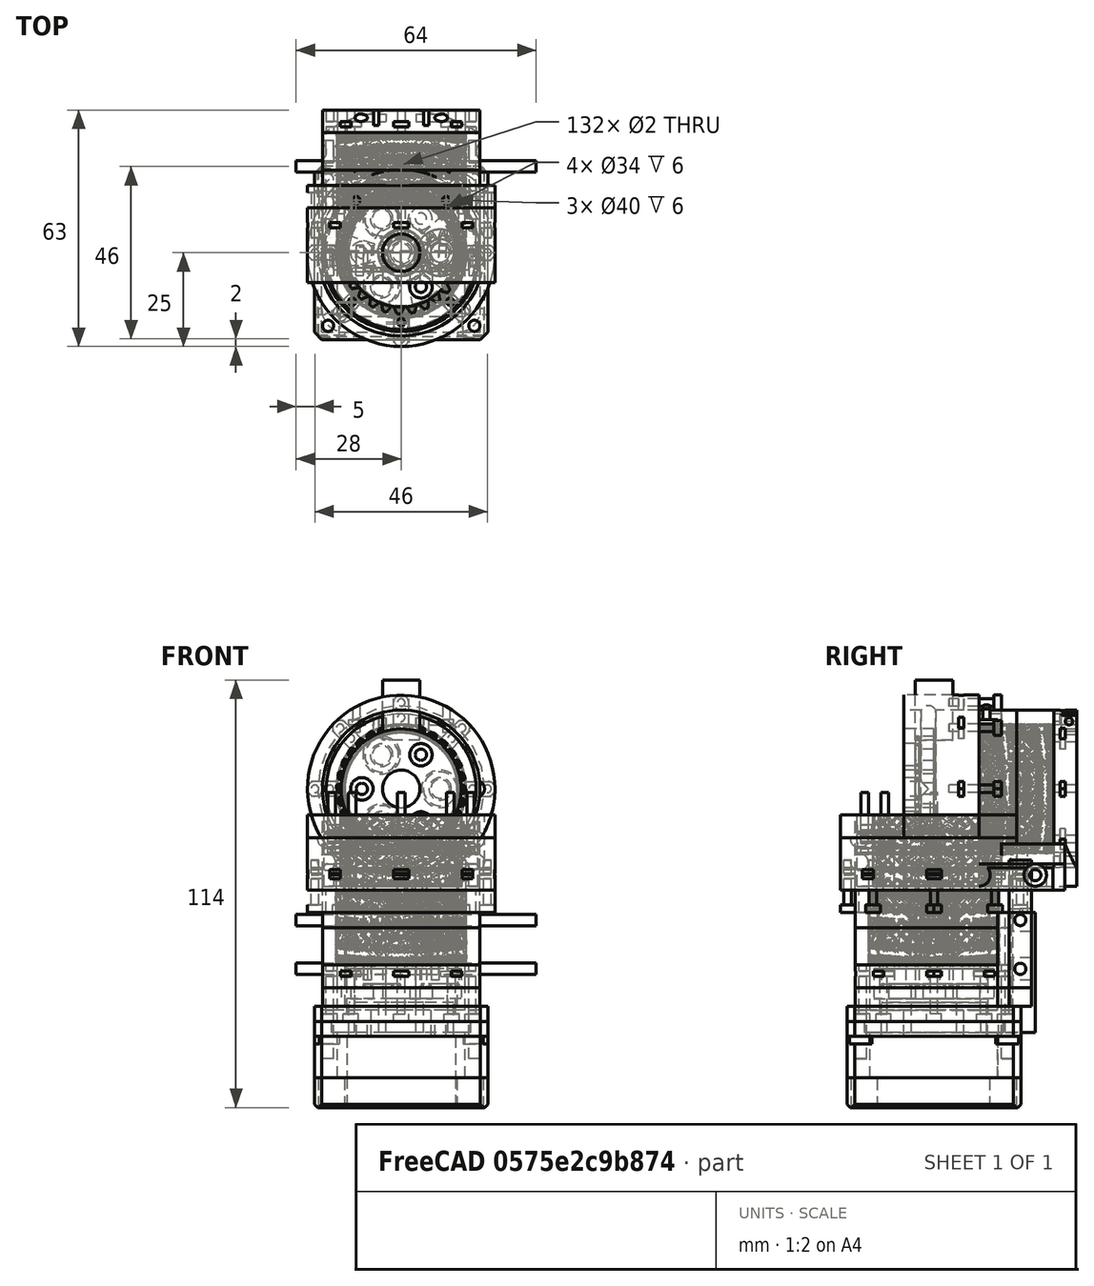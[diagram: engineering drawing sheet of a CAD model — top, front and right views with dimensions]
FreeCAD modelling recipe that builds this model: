
FCSTD DOCUMENT  (FreeCAD 0.19R24276 (Git))
Label: G-mini_gearbox_036
License: All rights reserved
LicenseURL: http://en.wikipedia.org/wiki/All_rights_reserved
objects: Part::Cylinder×349, Part::Box×234, Part::Cut×155, Part::Compound×130, Part::FeaturePython×71, Part::Common×20, Mesh::Feature×13, Part::Torus×6, Part::Chamfer×6
note: 971 computed .brp shape members not serialized (recipe doc carries the construction recipe); baked Part::Feature solids carry a one-line shape summary decoded from their .brp

FEATURE [Part::Torus] Torus003  label="Anuloid003"
  Angle1 = -180
  Angle2 = 180
  Angle3 = 360
  AttacherType = Attacher::AttachEngine3D
  Placement = pos=(0,0,23.5) rot=(0,0,1;0rad)
  Radius1 = 20
  Radius2 = 2.2
FEATURE [Part::Cylinder] Cylinder061  label="Válec061"
  Angle = 360
  AttacherType = Attacher::AttachEngine3D
  Height = 10
  Placement = pos=(20,0,23.5) rot=(0,0,1;0rad)
  Radius = 2.2
FEATURE [Part::Cylinder] Cylinder062  label="Válec062"
  Angle = 360
  AttacherType = Attacher::AttachEngine3D
  Height = 10
  Placement = pos=(0,23,8) rot=(0,0,1;0rad)
  Radius = 1
FEATURE [Part::Cylinder] Cylinder063  label="Válec063"
  Angle = 360
  AttacherType = Attacher::AttachEngine3D
  Height = 10
  Placement = pos=(-16.26,16.26,8) rot=(0,0,1;0.785398rad)
  Radius = 1
FEATURE [Part::Cylinder] Cylinder064  label="Válec064"
  Angle = 360
  AttacherType = Attacher::AttachEngine3D
  Height = 10
  Placement = pos=(-23,0,8) rot=(0,0,1;1.5708rad)
  Radius = 1
FEATURE [Part::Cylinder] Cylinder065  label="Válec065"
  Angle = 360
  AttacherType = Attacher::AttachEngine3D
  Height = 10
  Placement = pos=(-16.26,-16.26,8) rot=(0,0,1;2.35619rad)
  Radius = 1
FEATURE [Part::Cylinder] Cylinder066  label="Válec066"
  Angle = 360
  AttacherType = Attacher::AttachEngine3D
  Height = 10
  Placement = pos=(4e-15,-23,8) rot=(0,0,1;3.14159rad)
  Radius = 1
FEATURE [Part::Cylinder] Cylinder067  label="Válec067"
  Angle = 360
  AttacherType = Attacher::AttachEngine3D
  Height = 10
  Placement = pos=(16.26,-16.26,8) rot=(0,0,1;3.92699rad)
  Radius = 1
FEATURE [Part::Cylinder] Cylinder068  label="Válec068"
  Angle = 360
  AttacherType = Attacher::AttachEngine3D
  Height = 10
  Placement = pos=(23,1.1e-14,8) rot=(0,0,-1;1.5708rad)
  Radius = 1
FEATURE [Part::Cylinder] Cylinder069  label="Válec069"
  Angle = 360
  AttacherType = Attacher::AttachEngine3D
  Height = 10
  Placement = pos=(16.26,16.26,8) rot=(0,0,-1;0.785398rad)
  Radius = 1
FEATURE [Part::Compound] Compound019
  Links = -> [Cylinder062,Cylinder069,Cylinder068,Cylinder066,Cylinder067,Cylinder065,Cylinder063,Cylinder064]
FEATURE [Part::FeaturePython] Tube004  # WARN: FeaturePython — macro-defined, semantics opaque (R4)
  AttacherType = Attacher::AttachEngine3D
  Height = 20
  InnerRadius = 21
  OuterRadius = 25
  Placement = pos=(0,0,10) rot=(0,0,1;0rad)
FEATURE [Part::Cut] Cut018
  Base = -> Tube004
  Tool = -> Torus003
FEATURE [Part::Box] Box016  label="Krychle016"
  AttacherType = Attacher::AttachEngine3D
  Height = 1.4
  Length = 4
  Placement = pos=(-2,21,14) rot=(0,0,1;0rad)
  Width = 4
FEATURE [Part::Box] Box017  label="Krychle017"
  AttacherType = Attacher::AttachEngine3D
  Height = 1.4
  Length = 4
  Placement = pos=(-16.2635,13.435,14) rot=(0,0,1;0.785398rad)
  Width = 4
FEATURE [Part::Box] Box018  label="Krychle018"
  AttacherType = Attacher::AttachEngine3D
  Height = 1.4
  Length = 4
  Placement = pos=(-21,-2,14) rot=(0,0,1;1.5708rad)
  Width = 4
FEATURE [Part::Box] Box019  label="Krychle019"
  AttacherType = Attacher::AttachEngine3D
  Height = 1.4
  Length = 4
  Placement = pos=(-13.435,-16.2635,14) rot=(0,0,1;2.35619rad)
  Width = 4
FEATURE [Part::Box] Box020  label="Krychle020"
  AttacherType = Attacher::AttachEngine3D
  Height = 1.4
  Length = 4
  Placement = pos=(2,-21,14) rot=(0,0,1;3.14159rad)
  Width = 4
FEATURE [Part::Box] Box021  label="Krychle021"
  AttacherType = Attacher::AttachEngine3D
  Height = 1.4
  Length = 4
  Placement = pos=(16.2635,-13.435,14) rot=(0,0,1;3.92699rad)
  Width = 4
FEATURE [Part::Box] Box022  label="Krychle022"
  AttacherType = Attacher::AttachEngine3D
  Height = 1.4
  Length = 4
  Placement = pos=(21,2,14) rot=(0,0,-1;1.5708rad)
  Width = 4
FEATURE [Part::Box] Box023  label="Krychle023"
  AttacherType = Attacher::AttachEngine3D
  Height = 1.4
  Length = 4
  Placement = pos=(13.435,16.2635,14) rot=(0,0,-1;0.785398rad)
  Width = 4
FEATURE [Part::Compound] Compound020
  Links = -> [Box016,Box017,Box018,Box019,Box020,Box021,Box022,Box023]
FEATURE [Part::Cut] Cut019
  Base = -> Cut018
  Tool = -> Compound020
FEATURE [Part::Cut] Cut020
  Base = -> Cut019
  Tool = -> Compound019
FEATURE [Part::Cut] Cut021  label="G-mini_bearing-ring-old"
  Base = -> Cut020
  Placement = pos=(0,22,37) rot=(1,0,0;1.5708rad)
  Tool = -> Cylinder061
FEATURE [Part::Cylinder] Cylinder084  label="Válec084"
  Angle = 360
  AttacherType = Attacher::AttachEngine3D
  Height = 10
  Placement = pos=(0,23,4) rot=(0,0,1;0rad)
  Radius = 1
FEATURE [Part::Box] Box033  label="Krychle033"
  AttacherType = Attacher::AttachEngine3D
  Height = 6
  Length = 4
  Placement = pos=(10,17,5) rot=(0,0,1;0rad)
  Width = 1.4
FEATURE [Part::Box] Box034  label="Krychle034"
  AttacherType = Attacher::AttachEngine3D
  Height = 6
  Length = 4
  Placement = pos=(-14,17,5) rot=(0,0,1;0rad)
  Width = 1.4
FEATURE [Part::Cylinder] Cylinder077  label="Válec077"
  Angle = 360
  AttacherType = Attacher::AttachEngine3D
  Height = 10
  Placement = pos=(12,25,8) rot=(1,0,0;1.5708rad)
  Radius = 1
FEATURE [Part::Cylinder] Cylinder078  label="Válec078"
  Angle = 360
  AttacherType = Attacher::AttachEngine3D
  Height = 10
  Placement = pos=(-12,25,8) rot=(1,0,0;1.5708rad)
  Radius = 1
FEATURE [Part::Cylinder] Cylinder079  label="Válec079"
  Angle = 360
  AttacherType = Attacher::AttachEngine3D
  Height = 10
  Placement = pos=(16.2635,16.2635,4) rot=(0,0,-1;0.785398rad)
  Radius = 1
FEATURE [Part::Cylinder] Cylinder080  label="Válec080"
  Angle = 360
  AttacherType = Attacher::AttachEngine3D
  Height = 10
  Placement = pos=(16.2635,-16.2635,4) rot=(0,0,1;3.92699rad)
  Radius = 1
FEATURE [Part::Cylinder] Cylinder081  label="Válec081"
  Angle = 360
  AttacherType = Attacher::AttachEngine3D
  Height = 10
  Placement = pos=(-16.2635,16.2635,4) rot=(0,0,1;0.785398rad)
  Radius = 1
FEATURE [Part::Compound] Compound026
  Links = -> [Box033,Box034]
FEATURE [Part::FeaturePython] Tube005  # WARN: FeaturePython — macro-defined, semantics opaque (R4)
  AttacherType = Attacher::AttachEngine3D
  Height = 6
  InnerRadius = 20
  OuterRadius = 25
  Placement = pos=(0,0,4) rot=(0,0,1;0rad)
FEATURE [Part::FeaturePython] Tube006  # WARN: FeaturePython — macro-defined, semantics opaque (R4)
  AttacherType = Attacher::AttachEngine3D
  Height = 6
  InnerRadius = 17
  OuterRadius = 21
  Placement = pos=(0,0,-16) rot=(0,0,1;0rad)
FEATURE [Part::Cylinder] Cylinder082  label="Válec082"
  Angle = 360
  AttacherType = Attacher::AttachEngine3D
  Height = 2
  Placement = pos=(-16.2635,-16.2635,4) rot=(0,0,1;2.35619rad)
  Radius = 2
FEATURE [Part::Cylinder] Cylinder083  label="Válec083"
  Angle = 360
  AttacherType = Attacher::AttachEngine3D
  Height = 10
  Placement = pos=(-23,-1e-15,4) rot=(0,0,1;1.5708rad)
  Radius = 1
FEATURE [Part::Cylinder] Cylinder085  label="Válec085"
  Angle = 360
  AttacherType = Attacher::AttachEngine3D
  Height = 10
  Placement = pos=(-16.2635,-16.2635,4) rot=(0,0,1;2.35619rad)
  Radius = 1
FEATURE [Part::Cylinder] Cylinder086  label="Válec086"
  Angle = 360
  AttacherType = Attacher::AttachEngine3D
  Height = 2
  Placement = pos=(0,23,4) rot=(0,0,1;0rad)
  Radius = 2
FEATURE [Part::Cylinder] Cylinder087  label="Válec087"
  Angle = 360
  AttacherType = Attacher::AttachEngine3D
  Height = 10
  Placement = pos=(23,1.1e-14,4) rot=(0,0,-1;1.5708rad)
  Radius = 1
FEATURE [Part::Cylinder] Cylinder088  label="Válec088"
  Angle = 360
  AttacherType = Attacher::AttachEngine3D
  Height = 2
  Placement = pos=(-23,-1e-15,4) rot=(0,0,1;1.5708rad)
  Radius = 2
FEATURE [Part::Cylinder] Cylinder089  label="Válec089"
  Angle = 360
  AttacherType = Attacher::AttachEngine3D
  Height = 10
  Placement = pos=(4e-15,-23,4) rot=(0,0,1;3.14159rad)
  Radius = 1
FEATURE [Part::Compound] Compound027
  Links = -> [Cylinder084,Cylinder081,Cylinder083,Cylinder085,Cylinder089,Cylinder080,Cylinder087,Cylinder079]
FEATURE [Part::Cylinder] Cylinder090  label="Válec090"
  Angle = 360
  AttacherType = Attacher::AttachEngine3D
  Height = 2
  Placement = pos=(16.2635,-16.2635,4) rot=(0,0,1;3.92699rad)
  Radius = 2
FEATURE [Part::Cylinder] Cylinder091  label="Válec091"
  Angle = 360
  AttacherType = Attacher::AttachEngine3D
  Height = 2
  Placement = pos=(23,1.1e-14,4) rot=(0,0,-1;1.5708rad)
  Radius = 2
FEATURE [Part::Cylinder] Cylinder092  label="Válec092"
  Angle = 360
  AttacherType = Attacher::AttachEngine3D
  Height = 2
  Placement = pos=(16.2635,16.2635,4) rot=(0,0,-1;0.785398rad)
  Radius = 2
FEATURE [Part::Cylinder] Cylinder093  label="Válec093"
  Angle = 360
  AttacherType = Attacher::AttachEngine3D
  Height = 2
  Placement = pos=(-16.2635,16.2635,4) rot=(0,0,1;0.785398rad)
  Radius = 2
FEATURE [Part::Cylinder] Cylinder094  label="Válec094"
  Angle = 360
  AttacherType = Attacher::AttachEngine3D
  Height = 2
  Placement = pos=(4e-15,-23,4) rot=(0,0,1;3.14159rad)
  Radius = 2
FEATURE [Part::Compound] Compound028
  Links = -> [Cylinder086,Cylinder093,Cylinder088,Cylinder082,Cylinder094,Cylinder090,Cylinder091,Cylinder092]
FEATURE [Part::Cut] Cut026
  Base = -> Tube005
  Tool = -> Compound028
FEATURE [Part::Cut] Cut027
  Base = -> Cut026
  Tool = -> Compound027
FEATURE [Part::Cut] Cut032
  Base = -> Cut027
  Tool = -> Compound026
FEATURE [Part::Box] Box035  label="Krychle035"
  AttacherType = Attacher::AttachEngine3D
  Height = 1.4
  Length = 4
  Placement = pos=(-2,17,-13) rot=(0,0,1;0rad)
  Width = 4
FEATURE [Part::Box] Box036  label="Krychle036"
  AttacherType = Attacher::AttachEngine3D
  Height = 1.4
  Length = 4
  Placement = pos=(-13.435,10.6066,-13) rot=(0,0,1;0.785398rad)
  Width = 4
FEATURE [Part::Box] Box037  label="Krychle037"
  AttacherType = Attacher::AttachEngine3D
  Height = 1.4
  Length = 4
  Placement = pos=(-10.6066,-13.435,-13) rot=(0,0,1;2.35619rad)
  Width = 4
FEATURE [Part::Box] Box038  label="Krychle038"
  AttacherType = Attacher::AttachEngine3D
  Height = 1.4
  Length = 4
  Placement = pos=(2,-17,-13) rot=(0,0,1;3.14159rad)
  Width = 4
FEATURE [Part::Compound] Compound033
  Links = -> [Cylinder077,Cylinder078]
FEATURE [Part::Cylinder] Cylinder095  label="Válec095"
  Angle = 360
  AttacherType = Attacher::AttachEngine3D
  Height = 10
  Placement = pos=(0,19,-20) rot=(0,0,1;0rad)
  Radius = 1
FEATURE [Part::Box] Box039  label="Krychle039"
  AttacherType = Attacher::AttachEngine3D
  Height = 1.4
  Length = 4
  Placement = pos=(-17,-2,-13) rot=(0,0,1;1.5708rad)
  Width = 4
FEATURE [Part::Box] Box040  label="Krychle040"
  AttacherType = Attacher::AttachEngine3D
  Height = 1.4
  Length = 4
  Placement = pos=(13.435,-10.6066,-13) rot=(0,0,1;3.92699rad)
  Width = 4
FEATURE [Part::Box] Box041  label="Krychle041"
  AttacherType = Attacher::AttachEngine3D
  Height = 1.4
  Length = 4
  Placement = pos=(10.6066,13.435,-13) rot=(0,0,-1;0.785398rad)
  Width = 4
FEATURE [Part::Cylinder] Cylinder096  label="Válec096"
  Angle = 360
  AttacherType = Attacher::AttachEngine3D
  Height = 10
  Placement = pos=(-13.435,13.435,-20) rot=(0,0,1;0.785398rad)
  Radius = 1
FEATURE [Part::Cylinder] Cylinder097  label="Válec097"
  Angle = 360
  AttacherType = Attacher::AttachEngine3D
  Height = 10
  Placement = pos=(-19,-1e-15,-20) rot=(0,0,1;1.5708rad)
  Radius = 1
FEATURE [Part::Cylinder] Cylinder098  label="Válec098"
  Angle = 360
  AttacherType = Attacher::AttachEngine3D
  Height = 10
  Placement = pos=(-13.435,-13.435,-20) rot=(0,0,1;2.35619rad)
  Radius = 1
FEATURE [Part::Cylinder] Cylinder099  label="Válec099"
  Angle = 360
  AttacherType = Attacher::AttachEngine3D
  Height = 10
  Placement = pos=(6e-15,-19,-20) rot=(0,0,1;3.14159rad)
  Radius = 1
FEATURE [Part::Cylinder] Cylinder100  label="Válec100"
  Angle = 360
  AttacherType = Attacher::AttachEngine3D
  Height = 10
  Placement = pos=(13.435,-13.435,-20) rot=(0,0,1;3.92699rad)
  Radius = 1
FEATURE [Part::Box] Box042  label="Krychle042"
  AttacherType = Attacher::AttachEngine3D
  Height = 1.4
  Length = 4
  Placement = pos=(17,2,-13) rot=(0,0,-1;1.5708rad)
  Width = 4
FEATURE [Part::Compound] Compound029
  Links = -> [Box035,Box036,Box039,Box037,Box038,Box040,Box042,Box041]
FEATURE [Part::Cut] Cut028
  Base = -> Tube006
  Tool = -> Compound029
FEATURE [Part::Cylinder] Cylinder101  label="Válec101"
  Angle = 360
  AttacherType = Attacher::AttachEngine3D
  Height = 10
  Placement = pos=(19,8e-15,-20) rot=(0,0,-1;1.5708rad)
  Radius = 1
FEATURE [Part::Cylinder] Cylinder102  label="Válec102"
  Angle = 360
  AttacherType = Attacher::AttachEngine3D
  Height = 10
  Placement = pos=(13.435,13.435,-20) rot=(0,0,-1;0.785398rad)
  Radius = 1
FEATURE [Part::Compound] Compound030
  Links = -> [Cylinder095,Cylinder096,Cylinder097,Cylinder098,Cylinder099,Cylinder100,Cylinder101,Cylinder102]
FEATURE [Part::Cut] Cut029
  Base = -> Cut028
  Tool = -> Compound030
FEATURE [Part::Cylinder] Cylinder103  label="Válec103"
  Angle = 360
  AttacherType = Attacher::AttachEngine3D
  Height = 10
  Radius = 21
FEATURE [Part::Cylinder] Cylinder104  label="Válec104"
  Angle = 360
  AttacherType = Attacher::AttachEngine3D
  Height = 10
  Radius = 21
FEATURE [Part::Box] Box043  label="Krychle043"
  AttacherType = Attacher::AttachEngine3D
  Height = 6
  Length = 4
  Placement = pos=(10,17,5) rot=(0,0,1;0rad)
  Width = 1.4
FEATURE [Part::Box] Box044  label="Krychle044"
  AttacherType = Attacher::AttachEngine3D
  Height = 6
  Length = 4
  Placement = pos=(-14,17,5) rot=(0,0,1;0rad)
  Width = 1.4
FEATURE [Part::Compound] Compound032
  Links = -> [Box043,Box044]
FEATURE [Part::FeaturePython] wormgear040  # WARN: FeaturePython — macro-defined, semantics opaque (R4)
  AttacherType = Attacher::AttachEngine3D
  Placement = pos=(0,0,0) rot=(0,0,1;1.13446rad)
  beta = 36.4444
  clearance = 0.25
  diameter = 32.5
  head = 0
  height = 12
  module = 0.8
  pressure_angle = 20
  reverse_pitch = true
  teeth = 30
  version = 0.0.3
FEATURE [Part::Cut] Cut031
  Base = -> Cylinder103
  Tool = -> wormgear040
FEATURE [Part::Cylinder] Cylinder105  label="Válec105"
  Angle = 360
  AttacherType = Attacher::AttachEngine3D
  Height = 10
  Placement = pos=(-12,25,8) rot=(1,0,0;1.5708rad)
  Radius = 1
FEATURE [Part::Cylinder] Cylinder106  label="Válec106"
  Angle = 360
  AttacherType = Attacher::AttachEngine3D
  Height = 10
  Placement = pos=(12,25,8) rot=(1,0,0;1.5708rad)
  Radius = 1
FEATURE [Part::Compound] Compound034
  Links = -> [Cylinder106,Cylinder105]
FEATURE [Part::Cut] Cut035
  Base = -> Cut032
  Tool = -> Compound034
FEATURE [Part::Box] Box045  label="Krychle045"
  AttacherType = Attacher::AttachEngine3D
  Height = 4
  Length = 1.4
  Placement = pos=(-7.4,15,-16) rot=(0,0,1;0rad)
  Width = 6
FEATURE [Part::Cylinder] Cylinder107  label="Válec107"
  Angle = 360
  AttacherType = Attacher::AttachEngine3D
  Height = 16
  Placement = pos=(4,18,-14) rot=(0,1,0;1.5708rad)
  Radius = 1
FEATURE [Part::Cylinder] Cylinder108  label="Válec108"
  Angle = 360
  AttacherType = Attacher::AttachEngine3D
  Height = 16
  Placement = pos=(-20,18,-14) rot=(0,1,0;1.5708rad)
  Radius = 1
FEATURE [Part::Compound] Compound036
  Links = -> [Cylinder108,Cylinder107]
FEATURE [Part::Box] Box046  label="Krychle046"
  AttacherType = Attacher::AttachEngine3D
  Height = 4
  Length = 1.4
  Placement = pos=(6,15,-16) rot=(0,0,1;0rad)
  Width = 6
FEATURE [Part::Compound] Compound035
  Links = -> [Box045,Box046]
FEATURE [Part::Cut] Cut036
  Base = -> Cut029
  Tool = -> Compound035
FEATURE [Part::Cut] Cut037
  Base = -> Cut036
  Tool = -> Compound036
FEATURE [Part::FeaturePython] wormgear039  # WARN: FeaturePython — macro-defined, semantics opaque (R4)
  AttacherType = Attacher::AttachEngine3D
  Placement = pos=(0,0,0) rot=(0,0,1;1.13796rad)
  beta = 36.4444
  clearance = 0.25
  diameter = 32.5
  head = 0
  height = 12
  module = 0.8
  pressure_angle = 20
  reverse_pitch = false
  teeth = 30
  version = 0.0.3
FEATURE [Part::Cut] Cut030
  Base = -> Cylinder104
  Placement = pos=(0,0,-10) rot=(0,0,1;0rad)
  Tool = -> wormgear039
FEATURE [Part::Compound] Compound031  label="gearovina-mini_okruh001"
  Links = -> [Cut030,Cut031]
FEATURE [Part::Cut] Cut033
  Base = -> Compound031
  Tool = -> Compound032
FEATURE [Part::Cut] Cut034
  Base = -> Cut033
  Tool = -> Compound033
FEATURE [Part::Compound] Compound037  label="G-mini_monoblock-old"
  Links = -> [Cut035,Cut037,Cut034]
  Placement = pos=(0,22,37) rot=(1,0,0;1.5708rad)
FEATURE [Part::Cylinder] Cylinder109  label="Válec109"
  Angle = 360
  AttacherType = Attacher::AttachEngine3D
  Height = 10
  Radius = 21
FEATURE [Part::Cylinder] Cylinder110  label="Válec110"
  Angle = 360
  AttacherType = Attacher::AttachEngine3D
  Height = 10
  Radius = 21
FEATURE [Part::FeaturePython] wormgear041  # WARN: FeaturePython — macro-defined, semantics opaque (R4)
  AttacherType = Attacher::AttachEngine3D
  Placement = pos=(0,0,0) rot=(0,0,1;1.13446rad)
  beta = 42.7094
  clearance = 0.25
  diameter = 32.5
  head = 0
  height = 12
  module = 1
  pressure_angle = 20
  reverse_pitch = true
  teeth = 30
  version = 0.0.3
FEATURE [Part::Cut] Cut038
  Base = -> Cylinder109
  Tool = -> wormgear041
FEATURE [Part::FeaturePython] wormgear042  # WARN: FeaturePython — macro-defined, semantics opaque (R4)
  AttacherType = Attacher::AttachEngine3D
  Placement = pos=(0,0,0) rot=(0,0,1;1.09607rad)
  beta = 42.7094
  clearance = 0.25
  diameter = 32.5
  head = 0
  height = 12
  module = 1
  pressure_angle = 20
  reverse_pitch = false
  teeth = 30
  version = 0.0.3
FEATURE [Part::Cut] Cut039
  Base = -> Cylinder110
  Placement = pos=(0,0,-10) rot=(0,0,1;0rad)
  Tool = -> wormgear042
FEATURE [Part::Compound] Compound038  label="gearovina-mini_okruh002"
  Links = -> [Cut039,Cut038]
FEATURE [Part::FeaturePython] Tube007  # WARN: FeaturePython — macro-defined, semantics opaque (R4)
  AttacherType = Attacher::AttachEngine3D
  Height = 6
  InnerRadius = 17
  OuterRadius = 21
  Placement = pos=(0,0,-16) rot=(0,0,1;0rad)
FEATURE [Part::Box] Box047  label="Krychle047"
  AttacherType = Attacher::AttachEngine3D
  Height = 1.4
  Length = 4
  Placement = pos=(-2,17,-13) rot=(0,0,1;0rad)
  Width = 4
FEATURE [Part::Box] Box048  label="Krychle048"
  AttacherType = Attacher::AttachEngine3D
  Height = 1.4
  Length = 4
  Placement = pos=(-13.435,10.6066,-13) rot=(0,0,1;0.785398rad)
  Width = 4
FEATURE [Part::Box] Box049  label="Krychle049"
  AttacherType = Attacher::AttachEngine3D
  Height = 1.4
  Length = 4
  Placement = pos=(-10.6066,-13.435,-13) rot=(0,0,1;2.35619rad)
  Width = 4
FEATURE [Part::Box] Box050  label="Krychle050"
  AttacherType = Attacher::AttachEngine3D
  Height = 1.4
  Length = 4
  Placement = pos=(2,-17,-13) rot=(0,0,1;3.14159rad)
  Width = 4
FEATURE [Part::Cylinder] Cylinder111  label="Válec111"
  Angle = 360
  AttacherType = Attacher::AttachEngine3D
  Height = 10
  Placement = pos=(0,19,-20) rot=(0,0,1;0rad)
  Radius = 1
FEATURE [Part::Box] Box051  label="Krychle051"
  AttacherType = Attacher::AttachEngine3D
  Height = 1.4
  Length = 4
  Placement = pos=(-17,-2,-13) rot=(0,0,1;1.5708rad)
  Width = 4
FEATURE [Part::Box] Box052  label="Krychle052"
  AttacherType = Attacher::AttachEngine3D
  Height = 1.4
  Length = 4
  Placement = pos=(13.435,-10.6066,-13) rot=(0,0,1;3.92699rad)
  Width = 4
FEATURE [Part::Box] Box053  label="Krychle053"
  AttacherType = Attacher::AttachEngine3D
  Height = 1.4
  Length = 4
  Placement = pos=(10.6066,13.435,-13) rot=(0,0,-1;0.785398rad)
  Width = 4
FEATURE [Part::Cylinder] Cylinder112  label="Válec112"
  Angle = 360
  AttacherType = Attacher::AttachEngine3D
  Height = 10
  Placement = pos=(-13.435,13.435,-20) rot=(0,0,1;0.785398rad)
  Radius = 1
FEATURE [Part::Cylinder] Cylinder113  label="Válec113"
  Angle = 360
  AttacherType = Attacher::AttachEngine3D
  Height = 10
  Placement = pos=(-19,-1e-15,-20) rot=(0,0,1;1.5708rad)
  Radius = 1
FEATURE [Part::Cylinder] Cylinder114  label="Válec114"
  Angle = 360
  AttacherType = Attacher::AttachEngine3D
  Height = 10
  Placement = pos=(-13.435,-13.435,-20) rot=(0,0,1;2.35619rad)
  Radius = 1
FEATURE [Part::Cylinder] Cylinder115  label="Válec115"
  Angle = 360
  AttacherType = Attacher::AttachEngine3D
  Height = 10
  Placement = pos=(6e-15,-19,-20) rot=(0,0,1;3.14159rad)
  Radius = 1
FEATURE [Part::Cylinder] Cylinder116  label="Válec116"
  Angle = 360
  AttacherType = Attacher::AttachEngine3D
  Height = 10
  Placement = pos=(13.435,-13.435,-20) rot=(0,0,1;3.92699rad)
  Radius = 1
FEATURE [Part::Box] Box054  label="Krychle054"
  AttacherType = Attacher::AttachEngine3D
  Height = 1.4
  Length = 4
  Placement = pos=(17,2,-13) rot=(0,0,-1;1.5708rad)
  Width = 4
FEATURE [Part::Compound] Compound039
  Links = -> [Box047,Box048,Box051,Box049,Box050,Box052,Box054,Box053]
FEATURE [Part::Cut] Cut040
  Base = -> Tube007
  Tool = -> Compound039
FEATURE [Part::Cylinder] Cylinder117  label="Válec117"
  Angle = 360
  AttacherType = Attacher::AttachEngine3D
  Height = 10
  Placement = pos=(19,8e-15,-20) rot=(0,0,-1;1.5708rad)
  Radius = 1
FEATURE [Part::Cylinder] Cylinder118  label="Válec118"
  Angle = 360
  AttacherType = Attacher::AttachEngine3D
  Height = 10
  Placement = pos=(13.435,13.435,-20) rot=(0,0,-1;0.785398rad)
  Radius = 1
FEATURE [Part::Compound] Compound040
  Links = -> [Cylinder111,Cylinder112,Cylinder113,Cylinder114,Cylinder115,Cylinder116,Cylinder117,Cylinder118]
FEATURE [Part::Cut] Cut041
  Base = -> Cut040
  Tool = -> Compound040
FEATURE [Part::Cylinder] Cylinder119  label="Válec119"
  Angle = 360
  AttacherType = Attacher::AttachEngine3D
  Height = 10
  Placement = pos=(0,23,4) rot=(0,0,1;0rad)
  Radius = 1
FEATURE [Part::Cylinder] Cylinder120  label="Válec120"
  Angle = 360
  AttacherType = Attacher::AttachEngine3D
  Height = 10
  Placement = pos=(16.2635,16.2635,4) rot=(0,0,-1;0.785398rad)
  Radius = 1
FEATURE [Part::Cylinder] Cylinder121  label="Válec121"
  Angle = 360
  AttacherType = Attacher::AttachEngine3D
  Height = 10
  Placement = pos=(16.2635,-16.2635,4) rot=(0,0,1;3.92699rad)
  Radius = 1
FEATURE [Part::Cylinder] Cylinder122  label="Válec122"
  Angle = 360
  AttacherType = Attacher::AttachEngine3D
  Height = 10
  Placement = pos=(-16.2635,16.2635,4) rot=(0,0,1;0.785398rad)
  Radius = 1
FEATURE [Part::Cylinder] Cylinder123  label="Válec123"
  Angle = 360
  AttacherType = Attacher::AttachEngine3D
  Height = 2
  Placement = pos=(-16.2635,-16.2635,4) rot=(0,0,1;2.35619rad)
  Radius = 2
FEATURE [Part::FeaturePython] Tube008  # WARN: FeaturePython — macro-defined, semantics opaque (R4)
  AttacherType = Attacher::AttachEngine3D
  Height = 6
  InnerRadius = 20
  OuterRadius = 25
  Placement = pos=(0,0,4) rot=(0,0,1;0rad)
FEATURE [Part::Cylinder] Cylinder124  label="Válec124"
  Angle = 360
  AttacherType = Attacher::AttachEngine3D
  Height = 10
  Placement = pos=(-23,-1e-15,4) rot=(0,0,1;1.5708rad)
  Radius = 1
FEATURE [Part::Cylinder] Cylinder125  label="Válec125"
  Angle = 360
  AttacherType = Attacher::AttachEngine3D
  Height = 10
  Placement = pos=(-16.2635,-16.2635,4) rot=(0,0,1;2.35619rad)
  Radius = 1
FEATURE [Part::Cylinder] Cylinder126  label="Válec126"
  Angle = 360
  AttacherType = Attacher::AttachEngine3D
  Height = 2
  Placement = pos=(0,23,4) rot=(0,0,1;0rad)
  Radius = 2
FEATURE [Part::Cylinder] Cylinder127  label="Válec127"
  Angle = 360
  AttacherType = Attacher::AttachEngine3D
  Height = 10
  Placement = pos=(23,1.1e-14,4) rot=(0,0,-1;1.5708rad)
  Radius = 1
FEATURE [Part::Cylinder] Cylinder128  label="Válec128"
  Angle = 360
  AttacherType = Attacher::AttachEngine3D
  Height = 2
  Placement = pos=(-23,-1e-15,4) rot=(0,0,1;1.5708rad)
  Radius = 2
FEATURE [Part::Cylinder] Cylinder129  label="Válec129"
  Angle = 360
  AttacherType = Attacher::AttachEngine3D
  Height = 10
  Placement = pos=(4e-15,-23,4) rot=(0,0,1;3.14159rad)
  Radius = 1
FEATURE [Part::Compound] Compound041
  Links = -> [Cylinder119,Cylinder122,Cylinder124,Cylinder125,Cylinder129,Cylinder121,Cylinder127,Cylinder120]
FEATURE [Part::Cylinder] Cylinder130  label="Válec130"
  Angle = 360
  AttacherType = Attacher::AttachEngine3D
  Height = 2
  Placement = pos=(16.2635,-16.2635,4) rot=(0,0,1;3.92699rad)
  Radius = 2
FEATURE [Part::Cylinder] Cylinder131  label="Válec131"
  Angle = 360
  AttacherType = Attacher::AttachEngine3D
  Height = 2
  Placement = pos=(23,1.1e-14,4) rot=(0,0,-1;1.5708rad)
  Radius = 2
FEATURE [Part::Cylinder] Cylinder132  label="Válec132"
  Angle = 360
  AttacherType = Attacher::AttachEngine3D
  Height = 2
  Placement = pos=(16.2635,16.2635,4) rot=(0,0,-1;0.785398rad)
  Radius = 2
FEATURE [Part::Cylinder] Cylinder133  label="Válec133"
  Angle = 360
  AttacherType = Attacher::AttachEngine3D
  Height = 2
  Placement = pos=(-16.2635,16.2635,4) rot=(0,0,1;0.785398rad)
  Radius = 2
FEATURE [Part::Cylinder] Cylinder134  label="Válec134"
  Angle = 360
  AttacherType = Attacher::AttachEngine3D
  Height = 2
  Placement = pos=(4e-15,-23,4) rot=(0,0,1;3.14159rad)
  Radius = 2
FEATURE [Part::Compound] Compound042
  Links = -> [Cylinder126,Cylinder133,Cylinder128,Cylinder123,Cylinder134,Cylinder130,Cylinder131,Cylinder132]
FEATURE [Part::Cut] Cut043
  Base = -> Tube008
  Tool = -> Compound042
FEATURE [Part::Cut] Cut042
  Base = -> Cut043
  Tool = -> Compound041
FEATURE [Part::Box] Box887  label="Krychle886"
  AttacherType = Attacher::AttachEngine3D
  Height = 7
  Length = 6
  Placement = pos=(15,-8,10) rot=(0,0,1;0rad)
  Width = 44
FEATURE [Part::Box] Box888  label="Krychle887"
  AttacherType = Attacher::AttachEngine3D
  Height = 7
  Length = 6
  Placement = pos=(-21,-8,10) rot=(0,0,1;0rad)
  Width = 44
FEATURE [Part::Cylinder] Cylinder2648  label="Válec2618"
  Angle = 360
  AttacherType = Attacher::AttachEngine3D
  Height = 20
  Radius = 38
FEATURE [Part::Compound] Compound1171
  Links = -> [Box887,Box888]
FEATURE [Part::Common] Common006
  Base = -> Compound1171
  Tool = -> Cylinder2648
FEATURE [Part::Box] Box891  label="Krychle890"
  AttacherType = Attacher::AttachEngine3D
  Height = 18
  Length = 30
  Placement = pos=(-15,-8,11) rot=(0,0,1;0rad)
  Width = 50
FEATURE [Part::Box] Box892  label="Krychle891"
  AttacherType = Attacher::AttachEngine3D
  Height = 6
  Length = 2
  Placement = pos=(-12,-4,10) rot=(0,0,1;0rad)
  Width = 6
FEATURE [Part::FeaturePython] Tube123  # WARN: FeaturePython — macro-defined, semantics opaque (R4)
  AttacherType = Attacher::AttachEngine3D
  Height = 25
  InnerRadius = 2
  OuterRadius = 21
  Placement = pos=(0,43,37) rot=(1,0,0;1.5708rad)
FEATURE [Part::FeaturePython] Tube124  # WARN: FeaturePython — macro-defined, semantics opaque (R4)
  AttacherType = Attacher::AttachEngine3D
  Height = 26
  InnerRadius = 2
  OuterRadius = 25
  Placement = pos=(0,18,37) rot=(1,0,0;1.5708rad)
FEATURE [Part::Cut] Cut977
  Base = -> Box891
  Tool = -> Tube124
FEATURE [Part::Cut] Cut001
  Base = -> Cut977
  Tool = -> Tube123
FEATURE [Part::Compound] Compound
  Links = -> [Cut042,Cut041,Compound038]
  Placement = pos=(0,22,37) rot=(1,0,0;1.5708rad)
FEATURE [Part::Box] Box893  label="Krychle892"
  AttacherType = Attacher::AttachEngine3D
  Height = 6
  Length = 2
  Placement = pos=(10,-4,10) rot=(0,0,1;0rad)
  Width = 6
FEATURE [Part::Box] Box894  label="Krychle893"
  AttacherType = Attacher::AttachEngine3D
  Height = 6
  Length = 2
  Placement = pos=(-12,-4,10) rot=(0,0,1;0rad)
  Width = 6
FEATURE [Part::Box] Box895  label="Krychle894"
  AttacherType = Attacher::AttachEngine3D
  Height = 6
  Length = 2
  Placement = pos=(10,26,10) rot=(0,0,1;0rad)
  Width = 6
FEATURE [Part::Box] Box896  label="Krychle895"
  AttacherType = Attacher::AttachEngine3D
  Height = 6
  Length = 2
  Placement = pos=(-12,26,10) rot=(0,0,1;0rad)
  Width = 6
FEATURE [Part::Box] Box897  label="Krychle896"
  AttacherType = Attacher::AttachEngine3D
  Height = 6
  Length = 2
  Placement = pos=(10,12,10) rot=(0,0,1;0rad)
  Width = 6
FEATURE [Part::Box] Box898  label="Krychle897"
  AttacherType = Attacher::AttachEngine3D
  Height = 6
  Length = 2
  Placement = pos=(-12,12,10) rot=(0,0,1;0rad)
  Width = 6
FEATURE [Part::Compound] Compound1172
  Links = -> [Box893,Box894,Box895,Box896,Box897,Box898]
FEATURE [Part::Box] Box899  label="Krychle898"
  AttacherType = Attacher::AttachEngine3D
  Height = 6
  Length = 2
  Placement = pos=(10,-4,10) rot=(0,0,1;0rad)
  Width = 6
FEATURE [Part::Box] Box900  label="Krychle899"
  AttacherType = Attacher::AttachEngine3D
  Height = 6
  Length = 2
  Placement = pos=(-12,-4,10) rot=(0,0,1;0rad)
  Width = 6
FEATURE [Part::Box] Box901  label="Krychle900"
  AttacherType = Attacher::AttachEngine3D
  Height = 6
  Length = 2
  Placement = pos=(10,26,10) rot=(0,0,1;0rad)
  Width = 6
FEATURE [Part::Box] Box902  label="Krychle901"
  AttacherType = Attacher::AttachEngine3D
  Height = 6
  Length = 2
  Placement = pos=(-12,26,10) rot=(0,0,1;0rad)
  Width = 6
FEATURE [Part::Box] Box903  label="Krychle902"
  AttacherType = Attacher::AttachEngine3D
  Height = 6
  Length = 2
  Placement = pos=(10,11,10) rot=(0,0,1;0rad)
  Width = 6
FEATURE [Part::Box] Box904  label="Krychle903"
  AttacherType = Attacher::AttachEngine3D
  Height = 6
  Length = 2
  Placement = pos=(-12,11,10) rot=(0,0,1;0rad)
  Width = 6
FEATURE [Part::Compound] Compound1173
  Links = -> [Box899,Box900,Box901,Box902,Box903,Box904]
  Placement = pos=(0,-2,1) rot=(0,0,1;0rad)
FEATURE [Part::Cut] Cut
  Base = -> Cut001
  Tool = -> Compound1172
FEATURE [Part::FeaturePython] Tube025  # WARN: FeaturePython — macro-defined, semantics opaque (R4)
  AttacherType = Attacher::AttachEngine3D
  Height = 1
  InnerRadius = 2.5
  OuterRadius = 3
  Placement = pos=(-5.2,-9.00666,54) rot=(0,0,1;4.18879rad)
FEATURE [Part::Cylinder] Cylinder2649  label="Válec2619"
  Angle = 360
  AttacherType = Attacher::AttachEngine3D
  Height = 8
  Placement = pos=(0,0,50) rot=(0,0,1;0rad)
  Radius = 16
FEATURE [Part::Cylinder] Cylinder2650  label="Válec2620"
  Angle = 360
  AttacherType = Attacher::AttachEngine3D
  Height = 16
  Placement = pos=(0,0,50) rot=(0,0,1;0rad)
  Radius = 5
FEATURE [Part::Cylinder] Cylinder2651  label="Válec2621"
  Angle = 360
  AttacherType = Attacher::AttachEngine3D
  Height = 5
  Placement = pos=(10.4,0,50) rot=(0,0,1;0rad)
  Radius = 5
FEATURE [Part::Cylinder] Cylinder135  label="Válec135"
  Angle = 360
  AttacherType = Attacher::AttachEngine3D
  Height = 5
  Placement = pos=(-5.2,-9.00666,50) rot=(0,0,1;4.18879rad)
  Radius = 5
FEATURE [Part::Cylinder] Cylinder138  label="Válec138"
  Angle = 360
  AttacherType = Attacher::AttachEngine3D
  Height = 3
  Placement = pos=(-10.5,3e-15,55) rot=(0,0,1;3.14159rad)
  Radius = 3
FEATURE [Part::Cylinder] Cylinder142  label="Válec142"
  Angle = 360
  AttacherType = Attacher::AttachEngine3D
  Height = 5
  Placement = pos=(-5.2,9.00666,50) rot=(0,0,1;2.0944rad)
  Radius = 5
FEATURE [Part::Box] Box905  label="Krychle904"
  AttacherType = Attacher::AttachEngine3D
  Height = 60
  Length = 40
  Placement = pos=(-20,-20,0) rot=(0,0,1;0rad)
  Width = 20
FEATURE [Part::Box] Box906  label="Krychle905"
  AttacherType = Attacher::AttachEngine3D
  Height = 60
  Length = 20
  Placement = pos=(-19.32,-5.18,0) rot=(0,0,1;0.314159rad)
  Width = 20
FEATURE [Part::Cylinder] Cylinder143  label="Válec143"
  Angle = 360
  AttacherType = Attacher::AttachEngine3D
  Height = 60
  Placement = pos=(0,10.5,0) rot=(0,0,1;0rad)
  Radius = 1.5
FEATURE [Part::Box] Box907  label="Krychle906"
  AttacherType = Attacher::AttachEngine3D
  Height = 60
  Length = 20
  Placement = pos=(0,0,0) rot=(0,0,-1;0.314159rad)
  Width = 20
FEATURE [Part::Cylinder] Cylinder145  label="Válec145"
  Angle = 360
  AttacherType = Attacher::AttachEngine3D
  Height = 20
  Placement = pos=(-10.5,0.00186,40) rot=(0,0,1;3.14159rad)
  Radius = 1.5
FEATURE [Part::Cylinder] Cylinder146  label="Válec146"
  Angle = 360
  AttacherType = Attacher::AttachEngine3D
  Height = 3
  Placement = pos=(5.25,-9.09327,55) rot=(0,0,-1;1.0472rad)
  Radius = 3
FEATURE [Part::Cylinder] Cylinder147  label="Válec147"
  Angle = 360
  AttacherType = Attacher::AttachEngine3D
  Height = 3
  Placement = pos=(5.25,9.09327,55) rot=(0,0,1;1.0472rad)
  Radius = 3
FEATURE [Part::Cylinder] Cylinder148  label="Válec148"
  Angle = 360
  AttacherType = Attacher::AttachEngine3D
  Height = 20
  Placement = pos=(5.24839,-9.0942,40) rot=(0,0,-1;1.0472rad)
  Radius = 1.5
FEATURE [Part::Cylinder] Cylinder149  label="Válec149"
  Angle = 360
  AttacherType = Attacher::AttachEngine3D
  Height = 20
  Placement = pos=(5.25161,9.09234,40) rot=(0,0,1;1.0472rad)
  Radius = 1.5
FEATURE [Part::FeaturePython] Tube026  # WARN: FeaturePython — macro-defined, semantics opaque (R4)
  AttacherType = Attacher::AttachEngine3D
  Height = 1
  InnerRadius = 4.5
  OuterRadius = 5
  Placement = pos=(-5.2,9.00666,54) rot=(0,0,1;2.0944rad)
FEATURE [Part::FeaturePython] Tube027  # WARN: FeaturePython — macro-defined, semantics opaque (R4)
  AttacherType = Attacher::AttachEngine3D
  Height = 1
  InnerRadius = 2.5
  OuterRadius = 3
  Placement = pos=(10.4,0,54) rot=(0,0,1;0rad)
FEATURE [Part::FeaturePython] Tube028  # WARN: FeaturePython — macro-defined, semantics opaque (R4)
  AttacherType = Attacher::AttachEngine3D
  Height = 1
  InnerRadius = 4.5
  OuterRadius = 5
  Placement = pos=(-5.2,-9.00666,54) rot=(0,0,1;4.18879rad)
FEATURE [Part::FeaturePython] Tube029  # WARN: FeaturePython — macro-defined, semantics opaque (R4)
  AttacherType = Attacher::AttachEngine3D
  Height = 1
  InnerRadius = 2.5
  OuterRadius = 3
  Placement = pos=(-5.2,9.00666,54) rot=(0,0,1;2.0944rad)
FEATURE [Part::FeaturePython] Tube030  # WARN: FeaturePython — macro-defined, semantics opaque (R4)
  AttacherType = Attacher::AttachEngine3D
  Height = 1
  InnerRadius = 4.5
  OuterRadius = 5
  Placement = pos=(10.4,0,54) rot=(0,0,1;0rad)
FEATURE [Part::Compound] Compound049
  Links = -> [Tube030,Tube026,Tube028,Tube027,Tube029,Tube025]
FEATURE [Part::Compound] Compound051
  Links = -> [Cylinder2651,Cylinder135,Cylinder142,Cylinder2650]
FEATURE [Part::Cut] Cut050
  Base = -> Cylinder2649
  Tool = -> Compound051
FEATURE [Part::Compound] Compound054
  Links = -> [Cylinder138,Cylinder146,Cylinder147]
FEATURE [Part::Compound] Compound055
  Links = -> [Cylinder145,Cylinder148,Cylinder149]
FEATURE [Part::Cut] Cut057
  Base = -> Cut050
  Tool = -> Compound054
FEATURE [Part::Cut] Cut058
  Base = -> Cut057
  Tool = -> Compound055
FEATURE [Part::FeaturePython] Tube031  # WARN: FeaturePython — macro-defined, semantics opaque (R4)
  AttacherType = Attacher::AttachEngine3D
  Height = 22
  InnerRadius = 7.5
  OuterRadius = 14
  Placement = pos=(0,0,10) rot=(0,0,1;0rad)
FEATURE [Part::Cut] Cut051
  Base = -> Tube031
  Tool = -> Cylinder143
FEATURE [Part::Cut] Cut054
  Base = -> Cut051
  Tool = -> Box906
FEATURE [Part::Cut] Cut052
  Base = -> Cut054
  Tool = -> Box907
FEATURE [Part::Cut] Cut053  label="gearovina-mini_vzperovina001"
  Base = -> Cut052
  Placement = pos=(0,0,-2) rot=(0,0,-1;0.523599rad)
  Tool = -> Box905
FEATURE [Part::Cut] Cut055  label="gearovina-mini_vzperovina002"
  Base = -> Cut052
  Placement = pos=(0,0,-2) rot=(0,0,1;1.5708rad)
  Tool = -> Box905
FEATURE [Part::Cut] Cut056  label="gearovina-mini_vzperovina003"
  Base = -> Cut052
  Placement = pos=(0,0,-2) rot=(0,0,1;3.66519rad)
  Tool = -> Box905
FEATURE [Part::Compound] Compound053
  Links = -> [Cut053,Cut055,Cut056]
  Placement = pos=(0,0,-19) rot=(0,0,1;0rad)
FEATURE [Part::Compound] Compound056
  Links = -> [Cut058,Compound049]
  Placement = pos=(0,50,37) rot=(1,0,0;1.5708rad)
FEATURE [Part::Cylinder] Cylinder2652  label="Válec2622"
  Angle = 360
  AttacherType = Attacher::AttachEngine3D
  Height = 10
  Radius = 21
FEATURE [Part::Cylinder] Cylinder2653  label="Válec2623"
  Angle = 360
  AttacherType = Attacher::AttachEngine3D
  Height = 10
  Radius = 21
FEATURE [Part::Box] Box908  label="Krychle907"
  AttacherType = Attacher::AttachEngine3D
  Height = 1.4
  Length = 4
  Placement = pos=(-2,17,-13) rot=(0,0,1;0rad)
  Width = 4
FEATURE [Part::Box] Box909  label="Krychle908"
  AttacherType = Attacher::AttachEngine3D
  Height = 1.4
  Length = 4
  Placement = pos=(-13.435,10.6066,-13) rot=(0,0,1;0.785398rad)
  Width = 4
FEATURE [Part::FeaturePython] wormgear043  # WARN: FeaturePython — macro-defined, semantics opaque (R4)
  AttacherType = Attacher::AttachEngine3D
  Placement = pos=(0,0,0) rot=(0,0,1;1.13446rad)
  beta = 42.7094
  clearance = 0.25
  diameter = 32.5
  head = 0
  height = 12
  module = 1
  pressure_angle = 20
  reverse_pitch = true
  teeth = 30
  version = 0.0.3
FEATURE [Part::Cut] Cut978
  Base = -> Cylinder2652
  Tool = -> wormgear043
FEATURE [Part::Cylinder] Cylinder2654  label="Válec2624"
  Angle = 360
  AttacherType = Attacher::AttachEngine3D
  Height = 10
  Placement = pos=(-13.435,-13.435,-20) rot=(0,0,1;2.35619rad)
  Radius = 1
FEATURE [Part::Cylinder] Cylinder2655  label="Válec2625"
  Angle = 360
  AttacherType = Attacher::AttachEngine3D
  Height = 10
  Placement = pos=(6e-15,-19,-20) rot=(0,0,1;3.14159rad)
  Radius = 1
FEATURE [Part::Cylinder] Cylinder2656  label="Válec2626"
  Angle = 360
  AttacherType = Attacher::AttachEngine3D
  Height = 10
  Placement = pos=(13.435,-13.435,-20) rot=(0,0,1;3.92699rad)
  Radius = 1
FEATURE [Part::Box] Box910  label="Krychle909"
  AttacherType = Attacher::AttachEngine3D
  Height = 1.4
  Length = 4
  Placement = pos=(17,2,-13) rot=(0,0,-1;1.5708rad)
  Width = 4
FEATURE [Part::Cylinder] Cylinder2657  label="Válec2627"
  Angle = 360
  AttacherType = Attacher::AttachEngine3D
  Height = 10
  Placement = pos=(19,8e-15,-20) rot=(0,0,-1;1.5708rad)
  Radius = 1
FEATURE [Part::Cylinder] Cylinder2658  label="Válec2628"
  Angle = 360
  AttacherType = Attacher::AttachEngine3D
  Height = 10
  Placement = pos=(13.435,13.435,-20) rot=(0,0,-1;0.785398rad)
  Radius = 1
FEATURE [Part::Cylinder] Cylinder2659  label="Válec2629"
  Angle = 360
  AttacherType = Attacher::AttachEngine3D
  Height = 10
  Placement = pos=(0,23,4) rot=(0,0,1;0rad)
  Radius = 1
FEATURE [Part::Cylinder] Cylinder2660  label="Válec2630"
  Angle = 360
  AttacherType = Attacher::AttachEngine3D
  Height = 10
  Placement = pos=(16.2635,16.2635,4) rot=(0,0,-1;0.785398rad)
  Radius = 1
FEATURE [Part::FeaturePython] wormgear044  # WARN: FeaturePython — macro-defined, semantics opaque (R4)
  AttacherType = Attacher::AttachEngine3D
  Placement = pos=(0,0,0) rot=(0,0,1;1.09607rad)
  beta = 42.7094
  clearance = 0.25
  diameter = 32.5
  head = 0
  height = 12
  module = 1
  pressure_angle = 20
  reverse_pitch = false
  teeth = 30
  version = 0.0.3
FEATURE [Part::Cut] Cut979
  Base = -> Cylinder2653
  Placement = pos=(0,0,-10) rot=(0,0,1;0rad)
  Tool = -> wormgear044
FEATURE [Part::Compound] Compound1174  label="gearovina-mini_okruh003"
  Links = -> [Cut979,Cut978]
FEATURE [Part::FeaturePython] Tube125  # WARN: FeaturePython — macro-defined, semantics opaque (R4)
  AttacherType = Attacher::AttachEngine3D
  Height = 6
  InnerRadius = 17
  OuterRadius = 21
  Placement = pos=(0,0,-16) rot=(0,0,1;0rad)
FEATURE [Part::FeaturePython] Tube126  # WARN: FeaturePython — macro-defined, semantics opaque (R4)
  AttacherType = Attacher::AttachEngine3D
  Height = 6
  InnerRadius = 20
  OuterRadius = 25
  Placement = pos=(0,0,4) rot=(0,0,1;0rad)
FEATURE [Part::Box] Box911  label="Krychle910"
  AttacherType = Attacher::AttachEngine3D
  Height = 1.4
  Length = 4
  Placement = pos=(-10.6066,-13.435,-13) rot=(0,0,1;2.35619rad)
  Width = 4
FEATURE [Part::Box] Box912  label="Krychle911"
  AttacherType = Attacher::AttachEngine3D
  Height = 1.4
  Length = 4
  Placement = pos=(2,-17,-13) rot=(0,0,1;3.14159rad)
  Width = 4
FEATURE [Part::Cylinder] Cylinder2661  label="Válec2631"
  Angle = 360
  AttacherType = Attacher::AttachEngine3D
  Height = 10
  Placement = pos=(0,19,-20) rot=(0,0,1;0rad)
  Radius = 1
FEATURE [Part::Box] Box913  label="Krychle912"
  AttacherType = Attacher::AttachEngine3D
  Height = 1.4
  Length = 4
  Placement = pos=(-17,-2,-13) rot=(0,0,1;1.5708rad)
  Width = 4
FEATURE [Part::Box] Box914  label="Krychle913"
  AttacherType = Attacher::AttachEngine3D
  Height = 1.4
  Length = 4
  Placement = pos=(13.435,-10.6066,-13) rot=(0,0,1;3.92699rad)
  Width = 4
FEATURE [Part::Box] Box915  label="Krychle914"
  AttacherType = Attacher::AttachEngine3D
  Height = 1.4
  Length = 4
  Placement = pos=(10.6066,13.435,-13) rot=(0,0,-1;0.785398rad)
  Width = 4
FEATURE [Part::Compound] Compound1175
  Links = -> [Box908,Box909,Box913,Box911,Box912,Box914,Box910,Box915]
FEATURE [Part::Cylinder] Cylinder2662  label="Válec2632"
  Angle = 360
  AttacherType = Attacher::AttachEngine3D
  Height = 10
  Placement = pos=(-13.435,13.435,-20) rot=(0,0,1;0.785398rad)
  Radius = 1
FEATURE [Part::Cylinder] Cylinder2663  label="Válec2633"
  Angle = 360
  AttacherType = Attacher::AttachEngine3D
  Height = 10
  Placement = pos=(-19,-1e-15,-20) rot=(0,0,1;1.5708rad)
  Radius = 1
FEATURE [Part::Compound] Compound1176
  Links = -> [Cylinder2661,Cylinder2662,Cylinder2663,Cylinder2654,Cylinder2655,Cylinder2656,Cylinder2657,Cylinder2658]
FEATURE [Part::Cut] Cut982
  Base = -> Tube125
  Tool = -> Compound1175
FEATURE [Part::Cut] Cut981
  Base = -> Cut982
  Tool = -> Compound1176
FEATURE [Part::Cylinder] Cylinder2664  label="Válec2634"
  Angle = 360
  AttacherType = Attacher::AttachEngine3D
  Height = 10
  Placement = pos=(16.2635,-16.2635,4) rot=(0,0,1;3.92699rad)
  Radius = 1
FEATURE [Part::Cylinder] Cylinder2665  label="Válec2635"
  Angle = 360
  AttacherType = Attacher::AttachEngine3D
  Height = 10
  Placement = pos=(-16.2635,16.2635,4) rot=(0,0,1;0.785398rad)
  Radius = 1
FEATURE [Part::Cylinder] Cylinder2666  label="Válec2636"
  Angle = 360
  AttacherType = Attacher::AttachEngine3D
  Height = 2
  Placement = pos=(-16.2635,-16.2635,4) rot=(0,0,1;2.35619rad)
  Radius = 2
FEATURE [Part::Cylinder] Cylinder2667  label="Válec2637"
  Angle = 360
  AttacherType = Attacher::AttachEngine3D
  Height = 10
  Placement = pos=(-23,-1e-15,4) rot=(0,0,1;1.5708rad)
  Radius = 1
FEATURE [Part::Cylinder] Cylinder2668  label="Válec2638"
  Angle = 360
  AttacherType = Attacher::AttachEngine3D
  Height = 10
  Placement = pos=(-16.2635,-16.2635,4) rot=(0,0,1;2.35619rad)
  Radius = 1
FEATURE [Part::Cylinder] Cylinder2669  label="Válec2639"
  Angle = 360
  AttacherType = Attacher::AttachEngine3D
  Height = 2
  Placement = pos=(0,23,4) rot=(0,0,1;0rad)
  Radius = 2
FEATURE [Part::Cylinder] Cylinder2670  label="Válec2640"
  Angle = 360
  AttacherType = Attacher::AttachEngine3D
  Height = 10
  Placement = pos=(23,1.1e-14,4) rot=(0,0,-1;1.5708rad)
  Radius = 1
FEATURE [Part::Cylinder] Cylinder2671  label="Válec2641"
  Angle = 360
  AttacherType = Attacher::AttachEngine3D
  Height = 2
  Placement = pos=(-23,-1e-15,4) rot=(0,0,1;1.5708rad)
  Radius = 2
FEATURE [Part::Cylinder] Cylinder2672  label="Válec2642"
  Angle = 360
  AttacherType = Attacher::AttachEngine3D
  Height = 10
  Placement = pos=(4e-15,-23,4) rot=(0,0,1;3.14159rad)
  Radius = 1
FEATURE [Part::Compound] Compound1177
  Links = -> [Cylinder2659,Cylinder2665,Cylinder2667,Cylinder2668,Cylinder2672,Cylinder2664,Cylinder2670,Cylinder2660]
FEATURE [Part::Cylinder] Cylinder2673  label="Válec2643"
  Angle = 360
  AttacherType = Attacher::AttachEngine3D
  Height = 2
  Placement = pos=(16.2635,-16.2635,4) rot=(0,0,1;3.92699rad)
  Radius = 2
FEATURE [Part::Cylinder] Cylinder2674  label="Válec2644"
  Angle = 360
  AttacherType = Attacher::AttachEngine3D
  Height = 2
  Placement = pos=(23,1.1e-14,4) rot=(0,0,-1;1.5708rad)
  Radius = 2
FEATURE [Part::Cylinder] Cylinder2675  label="Válec2645"
  Angle = 360
  AttacherType = Attacher::AttachEngine3D
  Height = 2
  Placement = pos=(16.2635,16.2635,4) rot=(0,0,-1;0.785398rad)
  Radius = 2
FEATURE [Part::Cylinder] Cylinder2676  label="Válec2646"
  Angle = 360
  AttacherType = Attacher::AttachEngine3D
  Height = 2
  Placement = pos=(-16.2635,16.2635,4) rot=(0,0,1;0.785398rad)
  Radius = 2
FEATURE [Part::Cylinder] Cylinder2677  label="Válec2647"
  Angle = 360
  AttacherType = Attacher::AttachEngine3D
  Height = 2
  Placement = pos=(4e-15,-23,4) rot=(0,0,1;3.14159rad)
  Radius = 2
FEATURE [Part::Compound] Compound1178
  Links = -> [Cylinder2669,Cylinder2676,Cylinder2671,Cylinder2666,Cylinder2677,Cylinder2673,Cylinder2674,Cylinder2675]
FEATURE [Part::Cut] Cut980
  Base = -> Tube126
  Tool = -> Compound1178
FEATURE [Part::Cut] Cut983
  Base = -> Cut980
  Tool = -> Compound1177
FEATURE [Part::Cylinder] Cylinder2678  label="Válec2648"
  Angle = 360
  AttacherType = Attacher::AttachEngine3D
  Height = 10
  Placement = pos=(20,0,23.5) rot=(0,0,1;0rad)
  Radius = 2.2
FEATURE [Part::Cylinder] Cylinder2679  label="Válec2649"
  Angle = 360
  AttacherType = Attacher::AttachEngine3D
  Height = 10
  Placement = pos=(0,23,8) rot=(0,0,1;0rad)
  Radius = 1
FEATURE [Part::Cylinder] Cylinder2680  label="Válec2650"
  Angle = 360
  AttacherType = Attacher::AttachEngine3D
  Height = 10
  Placement = pos=(-16.26,16.26,8) rot=(0,0,1;0.785398rad)
  Radius = 1
FEATURE [Part::Cylinder] Cylinder2681  label="Válec2651"
  Angle = 360
  AttacherType = Attacher::AttachEngine3D
  Height = 10
  Placement = pos=(-23,0,8) rot=(0,0,1;1.5708rad)
  Radius = 1
FEATURE [Part::Cylinder] Cylinder2682  label="Válec2652"
  Angle = 360
  AttacherType = Attacher::AttachEngine3D
  Height = 10
  Placement = pos=(-16.26,-16.26,8) rot=(0,0,1;2.35619rad)
  Radius = 1
FEATURE [Part::Cylinder] Cylinder2683  label="Válec2653"
  Angle = 360
  AttacherType = Attacher::AttachEngine3D
  Height = 10
  Placement = pos=(4e-15,-23,8) rot=(0,0,1;3.14159rad)
  Radius = 1
FEATURE [Part::Cylinder] Cylinder2684  label="Válec2654"
  Angle = 360
  AttacherType = Attacher::AttachEngine3D
  Height = 10
  Placement = pos=(16.26,-16.26,8) rot=(0,0,1;3.92699rad)
  Radius = 1
FEATURE [Part::Cylinder] Cylinder2685  label="Válec2655"
  Angle = 360
  AttacherType = Attacher::AttachEngine3D
  Height = 10
  Placement = pos=(23,1.1e-14,8) rot=(0,0,-1;1.5708rad)
  Radius = 1
FEATURE [Part::Cylinder] Cylinder2686  label="Válec2656"
  Angle = 360
  AttacherType = Attacher::AttachEngine3D
  Height = 10
  Placement = pos=(16.26,16.26,8) rot=(0,0,-1;0.785398rad)
  Radius = 1
FEATURE [Part::Compound] Compound1179
  Links = -> [Cylinder2679,Cylinder2686,Cylinder2685,Cylinder2683,Cylinder2684,Cylinder2682,Cylinder2680,Cylinder2681]
FEATURE [Part::Box] Box916  label="Krychle915"
  AttacherType = Attacher::AttachEngine3D
  Height = 1.4
  Length = 4
  Placement = pos=(-2,21,14) rot=(0,0,1;0rad)
  Width = 4
FEATURE [Part::FeaturePython] Tube127  # WARN: FeaturePython — macro-defined, semantics opaque (R4)
  AttacherType = Attacher::AttachEngine3D
  Height = 20
  InnerRadius = 21
  OuterRadius = 25
  Placement = pos=(0,0,10) rot=(0,0,1;0rad)
FEATURE [Part::Torus] Torus004  label="Anuloid004"
  Angle1 = -180
  Angle2 = 180
  Angle3 = 360
  AttacherType = Attacher::AttachEngine3D
  Placement = pos=(0,0,23.5) rot=(0,0,1;0rad)
  Radius1 = 20
  Radius2 = 2.2
FEATURE [Part::Cut] Cut987
  Base = -> Tube127
  Tool = -> Torus004
FEATURE [Part::Box] Box917  label="Krychle916"
  AttacherType = Attacher::AttachEngine3D
  Height = 1.4
  Length = 4
  Placement = pos=(-16.2635,13.435,14) rot=(0,0,1;0.785398rad)
  Width = 4
FEATURE [Part::Box] Box918  label="Krychle917"
  AttacherType = Attacher::AttachEngine3D
  Height = 1.4
  Length = 4
  Placement = pos=(-21,-2,14) rot=(0,0,1;1.5708rad)
  Width = 4
FEATURE [Part::Box] Box919  label="Krychle918"
  AttacherType = Attacher::AttachEngine3D
  Height = 1.4
  Length = 4
  Placement = pos=(-13.435,-16.2635,14) rot=(0,0,1;2.35619rad)
  Width = 4
FEATURE [Part::Box] Box920  label="Krychle919"
  AttacherType = Attacher::AttachEngine3D
  Height = 1.4
  Length = 4
  Placement = pos=(2,-21,14) rot=(0,0,1;3.14159rad)
  Width = 4
FEATURE [Part::Box] Box921  label="Krychle920"
  AttacherType = Attacher::AttachEngine3D
  Height = 1.4
  Length = 4
  Placement = pos=(16.2635,-13.435,14) rot=(0,0,1;3.92699rad)
  Width = 4
FEATURE [Part::Box] Box922  label="Krychle921"
  AttacherType = Attacher::AttachEngine3D
  Height = 1.4
  Length = 4
  Placement = pos=(21,2,14) rot=(0,0,-1;1.5708rad)
  Width = 4
FEATURE [Part::Box] Box923  label="Krychle922"
  AttacherType = Attacher::AttachEngine3D
  Height = 1.4
  Length = 4
  Placement = pos=(13.435,16.2635,14) rot=(0,0,-1;0.785398rad)
  Width = 4
FEATURE [Part::Compound] Compound1180
  Links = -> [Box916,Box917,Box918,Box919,Box920,Box921,Box922,Box923]
FEATURE [Part::Cut] Cut986
  Base = -> Cut987
  Tool = -> Compound1180
FEATURE [Part::Cut] Cut985
  Base = -> Cut986
  Tool = -> Compound1179
FEATURE [Part::Cut] Cut984  label="G-mini_bearing-ring001"
  Base = -> Cut985
  Tool = -> Cylinder2678
FEATURE [Part::Cylinder] Cylinder2687  label="Válec2657"
  Angle = 360
  AttacherType = Attacher::AttachEngine3D
  Height = 30
  Radius = 38
FEATURE [Part::Common] Common
  Base = -> Cut
  Tool = -> Cylinder2687
FEATURE [Part::Cylinder] Cylinder  label="Válec"
  Angle = 360
  AttacherType = Attacher::AttachEngine3D
  Height = 64
  Placement = pos=(-26,14,13) rot=(0,1,0;1.5708rad)
  Radius = 1.5
FEATURE [Part::Cylinder] Cylinder2688  label="Válec2658"
  Angle = 360
  AttacherType = Attacher::AttachEngine3D
  Height = 64
  Placement = pos=(-26,-1,13) rot=(0,1,0;1.5708rad)
  Radius = 1.5
FEATURE [Part::Cylinder] Cylinder2689  label="Válec2659"
  Angle = 360
  AttacherType = Attacher::AttachEngine3D
  Height = 64
  Placement = pos=(-26,29,13) rot=(0,1,0;1.5708rad)
  Radius = 1.5
FEATURE [Part::Compound] Compound1181
  Links = -> [Cylinder,Cylinder2688,Cylinder2689]
  Placement = pos=(0,-2,1) rot=(0,0,1;0rad)
FEATURE [Part::Cylinder] Cylinder2690  label="Válec2660"
  Angle = 360
  AttacherType = Attacher::AttachEngine3D
  Height = 3
  Placement = pos=(-26,14,13) rot=(0,1,0;1.5708rad)
  Radius = 3
FEATURE [Part::Cylinder] Cylinder2691  label="Válec2661"
  Angle = 360
  AttacherType = Attacher::AttachEngine3D
  Height = 3
  Placement = pos=(-26,-1,13) rot=(0,1,0;1.5708rad)
  Radius = 3
FEATURE [Part::Cylinder] Cylinder2692  label="Válec2662"
  Angle = 360
  AttacherType = Attacher::AttachEngine3D
  Height = 3
  Placement = pos=(-26,29,13) rot=(0,1,0;1.5708rad)
  Radius = 3
FEATURE [Part::Compound] Compound1182
  Links = -> [Cylinder2690,Cylinder2691,Cylinder2692]
  Placement = pos=(5,-2,1) rot=(0,0,1;0rad)
FEATURE [Part::Cylinder] Cylinder2693  label="Válec2663"
  Angle = 360
  AttacherType = Attacher::AttachEngine3D
  Height = 3
  Placement = pos=(-26,-1,13) rot=(0,1,0;1.5708rad)
  Radius = 3
FEATURE [Part::Cylinder] Cylinder2694  label="Válec2664"
  Angle = 360
  AttacherType = Attacher::AttachEngine3D
  Height = 3
  Placement = pos=(-26,14,13) rot=(0,1,0;1.5708rad)
  Radius = 3
FEATURE [Part::Cylinder] Cylinder2695  label="Válec2665"
  Angle = 360
  AttacherType = Attacher::AttachEngine3D
  Height = 3
  Placement = pos=(-26,29,13) rot=(0,1,0;1.5708rad)
  Radius = 3
FEATURE [Part::Compound] Compound1183
  Links = -> [Cylinder2694,Cylinder2693,Cylinder2695]
  Placement = pos=(44,-2,1) rot=(0,0,1;0rad)
FEATURE [Part::Chamfer] Chamfer
  Base = -> Common006
  Edges = 2 edges r=1: [Edge6,Edge13]
FEATURE [Part::Cut] Cut988
  Base = -> Chamfer
  Tool = -> Compound1183
FEATURE [Part::Cut] Cut989
  Base = -> Cut988
  Tool = -> Compound1182
FEATURE [Part::Cut] Cut990
  Base = -> Cut989
  Tool = -> Compound1181
FEATURE [Part::Torus] Torus  label="Anuloid"
  Angle1 = -180
  Angle2 = 180
  Angle3 = 360
  AttacherType = Attacher::AttachEngine3D
  Placement = pos=(0,0,23.5) rot=(0,0,1;0rad)
  Radius1 = 19.75
  Radius2 = 2.2
FEATURE [Part::FeaturePython] wormgear037  # WARN: FeaturePython — macro-defined, semantics opaque (R4)
  AttacherType = Attacher::AttachEngine3D
  Placement = pos=(0,0,9) rot=(0,0,1;1.17286rad)
  beta = 34.8678
  clearance = 0.25
  diameter = 31
  head = 0
  height = 12
  module = 0.8
  pressure_angle = 20
  reverse_pitch = false
  teeth = 27
  version = 0.0.3
FEATURE [Part::FeaturePython] wormgear038  # WARN: FeaturePython — macro-defined, semantics opaque (R4)
  AttacherType = Attacher::AttachEngine3D
  Placement = pos=(0,0,19) rot=(0,0,1;1.1205rad)
  beta = 34.8678
  clearance = 0.25
  diameter = 31
  head = 0
  height = 12
  module = 0.8
  pressure_angle = 20
  reverse_pitch = true
  teeth = 27
  version = 0.0.3
FEATURE [Part::Cylinder] Cylinder050  label="Válec050"
  Angle = 360
  AttacherType = Attacher::AttachEngine3D
  Height = 9
  Placement = pos=(0,0,11) rot=(0,0,1;0rad)
  Radius = 20.5
FEATURE [Part::Cut] Cut013
  Base = -> Cylinder050
  Tool = -> wormgear037
FEATURE [Part::Cylinder] Cylinder051  label="Válec051"
  Angle = 360
  AttacherType = Attacher::AttachEngine3D
  Height = 10
  Placement = pos=(0,0,20) rot=(0,0,1;0rad)
  Radius = 20.5
FEATURE [Part::Cut] Cut012
  Base = -> Cylinder051
  Tool = -> wormgear038
FEATURE [Part::Box] Box008  label="Krychle008"
  AttacherType = Attacher::AttachEngine3D
  Height = 1.4
  Length = 4
  Placement = pos=(-2,16.5,26) rot=(0,0,1;0rad)
  Width = 4
FEATURE [Part::Cylinder] Cylinder052  label="Válec052"
  Angle = 360
  AttacherType = Attacher::AttachEngine3D
  Height = 10
  Placement = pos=(0,18.5,26) rot=(0,0,1;0rad)
  Radius = 1
FEATURE [Part::Box] Box009  label="Krychle009"
  AttacherType = Attacher::AttachEngine3D
  Height = 1.4
  Length = 4
  Placement = pos=(-13.0815,10.253,26) rot=(0,0,1;0.785398rad)
  Width = 4
FEATURE [Part::Box] Box010  label="Krychle010"
  AttacherType = Attacher::AttachEngine3D
  Height = 1.4
  Length = 4
  Placement = pos=(-16.5,-2,26) rot=(0,0,1;1.5708rad)
  Width = 4
FEATURE [Part::Box] Box011  label="Krychle011"
  AttacherType = Attacher::AttachEngine3D
  Height = 1.4
  Length = 4
  Placement = pos=(-10.253,-13.0815,26) rot=(0,0,1;2.35619rad)
  Width = 4
FEATURE [Part::Box] Box012  label="Krychle012"
  AttacherType = Attacher::AttachEngine3D
  Height = 1.4
  Length = 4
  Placement = pos=(2,-16.5,26) rot=(0,0,1;3.14159rad)
  Width = 4
FEATURE [Part::Box] Box013  label="Krychle013"
  AttacherType = Attacher::AttachEngine3D
  Height = 1.4
  Length = 4
  Placement = pos=(13.0815,-10.253,26) rot=(0,0,1;3.92699rad)
  Width = 4
FEATURE [Part::Box] Box014  label="Krychle014"
  AttacherType = Attacher::AttachEngine3D
  Height = 1.4
  Length = 4
  Placement = pos=(16.5,2,26) rot=(0,0,-1;1.5708rad)
  Width = 4
FEATURE [Part::Box] Box015  label="Krychle015"
  AttacherType = Attacher::AttachEngine3D
  Height = 1.4
  Length = 4
  Placement = pos=(10.253,13.0815,26) rot=(0,0,-1;0.785398rad)
  Width = 4
FEATURE [Part::Compound] Compound016
  Links = -> [Box008,Box009,Box010,Box011,Box012,Box013,Box014,Box015]
FEATURE [Part::Cut] Cut014
  Base = -> Cut012
  Tool = -> Compound016
FEATURE [Part::Cylinder] Cylinder053  label="Válec053"
  Angle = 360
  AttacherType = Attacher::AttachEngine3D
  Height = 10
  Placement = pos=(-13.08,13.08,26) rot=(0,0,1;0.785398rad)
  Radius = 1
FEATURE [Part::Cylinder] Cylinder054  label="Válec054"
  Angle = 360
  AttacherType = Attacher::AttachEngine3D
  Height = 10
  Placement = pos=(-18.5,0,26) rot=(0,0,1;1.5708rad)
  Radius = 1
FEATURE [Part::Cylinder] Cylinder055  label="Válec055"
  Angle = 360
  AttacherType = Attacher::AttachEngine3D
  Height = 10
  Placement = pos=(-13.08,-13.08,26) rot=(0,0,1;2.35619rad)
  Radius = 1
FEATURE [Part::Cylinder] Cylinder056  label="Válec056"
  Angle = 360
  AttacherType = Attacher::AttachEngine3D
  Height = 10
  Placement = pos=(6e-15,-18.5,26) rot=(0,0,1;3.14159rad)
  Radius = 1
FEATURE [Part::Cylinder] Cylinder057  label="Válec057"
  Angle = 360
  AttacherType = Attacher::AttachEngine3D
  Height = 10
  Placement = pos=(13.08,-13.08,26) rot=(0,0,1;3.92699rad)
  Radius = 1
FEATURE [Part::Cylinder] Cylinder058  label="Válec058"
  Angle = 360
  AttacherType = Attacher::AttachEngine3D
  Height = 10
  Placement = pos=(18.5,8e-15,26) rot=(0,0,-1;1.5708rad)
  Radius = 1
FEATURE [Part::Cylinder] Cylinder059  label="Válec059"
  Angle = 360
  AttacherType = Attacher::AttachEngine3D
  Height = 10
  Placement = pos=(13.08,13.08,26) rot=(0,0,-1;0.785398rad)
  Radius = 1
FEATURE [Part::Compound] Compound017
  Links = -> [Cylinder052,Cylinder053,Cylinder054,Cylinder055,Cylinder056,Cylinder057,Cylinder058,Cylinder059]
FEATURE [Part::Cut] Cut015
  Base = -> Cut014
  Tool = -> Compound017
FEATURE [Part::Cut] Cut016
  Base = -> Cut015
  Tool = -> Torus
FEATURE [Part::Cylinder] Cylinder060  label="Válec060"
  Angle = 360
  AttacherType = Attacher::AttachEngine3D
  Height = 10
  Placement = pos=(19,8,23.5) rot=(0,0,1;0.392699rad)
  Radius = 2.2
FEATURE [Part::Cut] Cut017
  Base = -> Cut016
  Tool = -> Cylinder060
FEATURE [Part::Compound] Compound018  label="gearovina-mini_rybovina"
  Links = -> [Cut013,Cut017]
FEATURE [Part::Box] Box924  label="Krychle923"
  AttacherType = Attacher::AttachEngine3D
  Height = 1.4
  Length = 4
  Placement = pos=(-2,16.5,26) rot=(0,0,1;0rad)
  Width = 4
FEATURE [Part::Box] Box925  label="Krychle924"
  AttacherType = Attacher::AttachEngine3D
  Height = 1.4
  Length = 4
  Placement = pos=(-13.0815,10.253,26) rot=(0,0,1;0.785398rad)
  Width = 4
FEATURE [Part::Box] Box926  label="Krychle925"
  AttacherType = Attacher::AttachEngine3D
  Height = 1.4
  Length = 4
  Placement = pos=(-16.5,-2,26) rot=(0,0,1;1.5708rad)
  Width = 4
FEATURE [Part::Box] Box927  label="Krychle926"
  AttacherType = Attacher::AttachEngine3D
  Height = 1.4
  Length = 4
  Placement = pos=(-10.253,-13.0815,26) rot=(0,0,1;2.35619rad)
  Width = 4
FEATURE [Part::Box] Box928  label="Krychle927"
  AttacherType = Attacher::AttachEngine3D
  Height = 1.4
  Length = 4
  Placement = pos=(2,-16.5,26) rot=(0,0,1;3.14159rad)
  Width = 4
FEATURE [Part::Box] Box929  label="Krychle928"
  AttacherType = Attacher::AttachEngine3D
  Height = 1.4
  Length = 4
  Placement = pos=(13.0815,-10.253,26) rot=(0,0,1;3.92699rad)
  Width = 4
FEATURE [Part::Box] Box930  label="Krychle929"
  AttacherType = Attacher::AttachEngine3D
  Height = 1.4
  Length = 4
  Placement = pos=(16.5,2,26) rot=(0,0,-1;1.5708rad)
  Width = 4
FEATURE [Part::Box] Box931  label="Krychle930"
  AttacherType = Attacher::AttachEngine3D
  Height = 1.4
  Length = 4
  Placement = pos=(10.253,13.0815,26) rot=(0,0,-1;0.785398rad)
  Width = 4
FEATURE [Part::Compound] Compound1184
  Links = -> [Box924,Box925,Box926,Box927,Box928,Box929,Box930,Box931]
FEATURE [Part::Cylinder] Cylinder2696  label="Válec2666"
  Angle = 360
  AttacherType = Attacher::AttachEngine3D
  Height = 10
  Placement = pos=(0,18.5,26) rot=(0,0,1;0rad)
  Radius = 1
FEATURE [Part::Cylinder] Cylinder2697  label="Válec2667"
  Angle = 360
  AttacherType = Attacher::AttachEngine3D
  Height = 10
  Placement = pos=(-13.08,13.08,26) rot=(0,0,1;0.785398rad)
  Radius = 1
FEATURE [Part::Cylinder] Cylinder2698  label="Válec2668"
  Angle = 360
  AttacherType = Attacher::AttachEngine3D
  Height = 10
  Placement = pos=(-18.5,0,26) rot=(0,0,1;1.5708rad)
  Radius = 1
FEATURE [Part::Cylinder] Cylinder2699  label="Válec2669"
  Angle = 360
  AttacherType = Attacher::AttachEngine3D
  Height = 10
  Placement = pos=(-13.08,-13.08,26) rot=(0,0,1;2.35619rad)
  Radius = 1
FEATURE [Part::Cylinder] Cylinder2700  label="Válec2670"
  Angle = 360
  AttacherType = Attacher::AttachEngine3D
  Height = 10
  Placement = pos=(6e-15,-18.5,26) rot=(0,0,1;3.14159rad)
  Radius = 1
FEATURE [Part::Cylinder] Cylinder2701  label="Válec2671"
  Angle = 360
  AttacherType = Attacher::AttachEngine3D
  Height = 10
  Placement = pos=(13.08,-13.08,26) rot=(0,0,1;3.92699rad)
  Radius = 1
FEATURE [Part::Cylinder] Cylinder2702  label="Válec2672"
  Angle = 360
  AttacherType = Attacher::AttachEngine3D
  Height = 10
  Placement = pos=(18.5,8e-15,26) rot=(0,0,-1;1.5708rad)
  Radius = 1
FEATURE [Part::Cylinder] Cylinder2703  label="Válec2673"
  Angle = 360
  AttacherType = Attacher::AttachEngine3D
  Height = 10
  Placement = pos=(13.08,13.08,26) rot=(0,0,-1;0.785398rad)
  Radius = 1
FEATURE [Part::Compound] Compound1185
  Links = -> [Cylinder2696,Cylinder2697,Cylinder2698,Cylinder2699,Cylinder2700,Cylinder2701,Cylinder2702,Cylinder2703]
FEATURE [Part::FeaturePython] Tube128  # WARN: FeaturePython — macro-defined, semantics opaque (R4)
  AttacherType = Attacher::AttachEngine3D
  Height = 1
  InnerRadius = 2.5
  OuterRadius = 3
  Placement = pos=(-5.2,-9.00666,54) rot=(0,0,1;4.18879rad)
FEATURE [Part::Cylinder] Cylinder2704  label="Válec2674"
  Angle = 360
  AttacherType = Attacher::AttachEngine3D
  Height = 14
  Placement = pos=(0,0,50) rot=(0,0,1;0rad)
  Radius = 20.5
FEATURE [Part::Cylinder] Cylinder2706  label="Válec2676"
  Angle = 360
  AttacherType = Attacher::AttachEngine3D
  Height = 5
  Placement = pos=(10.4,0,50) rot=(0,0,1;0rad)
  Radius = 5
FEATURE [Part::Cylinder] Cylinder2707  label="Válec2677"
  Angle = 360
  AttacherType = Attacher::AttachEngine3D
  Height = 5
  Placement = pos=(-5.2,-9.00666,50) rot=(0,0,1;4.18879rad)
  Radius = 5
FEATURE [Part::Cylinder] Cylinder2708  label="Válec2678"
  Angle = 360
  AttacherType = Attacher::AttachEngine3D
  Height = 3
  Placement = pos=(-10.5,3e-15,55) rot=(0,0,1;3.14159rad)
  Radius = 3
FEATURE [Part::Cylinder] Cylinder2709  label="Válec2679"
  Angle = 360
  AttacherType = Attacher::AttachEngine3D
  Height = 5
  Placement = pos=(-5.2,9.00666,50) rot=(0,0,1;2.0944rad)
  Radius = 5
FEATURE [Part::Compound] Compound1187
  Links = -> [Cylinder2706,Cylinder2707,Cylinder2709]
FEATURE [Part::Cut] Cut991
  Base = -> Cylinder2704
  Tool = -> Compound1187
FEATURE [Part::Cylinder] Cylinder2710  label="Válec2680"
  Angle = 360
  AttacherType = Attacher::AttachEngine3D
  Height = 20
  Placement = pos=(-10.5,0.00186,40) rot=(0,0,1;3.14159rad)
  Radius = 1.5
FEATURE [Part::Cylinder] Cylinder2711  label="Válec2681"
  Angle = 360
  AttacherType = Attacher::AttachEngine3D
  Height = 3
  Placement = pos=(5.25,-9.09327,55) rot=(0,0,-1;1.0472rad)
  Radius = 3
FEATURE [Part::Cylinder] Cylinder2712  label="Válec2682"
  Angle = 360
  AttacherType = Attacher::AttachEngine3D
  Height = 3
  Placement = pos=(5.25,9.09327,55) rot=(0,0,1;1.0472rad)
  Radius = 3
FEATURE [Part::Cylinder] Cylinder2713  label="Válec2683"
  Angle = 360
  AttacherType = Attacher::AttachEngine3D
  Height = 20
  Placement = pos=(5.24839,-9.0942,40) rot=(0,0,-1;1.0472rad)
  Radius = 1.5
FEATURE [Part::Cylinder] Cylinder2714  label="Válec2684"
  Angle = 360
  AttacherType = Attacher::AttachEngine3D
  Height = 20
  Placement = pos=(5.25161,9.09234,40) rot=(0,0,1;1.0472rad)
  Radius = 1.5
FEATURE [Part::FeaturePython] Tube129  # WARN: FeaturePython — macro-defined, semantics opaque (R4)
  AttacherType = Attacher::AttachEngine3D
  Height = 1
  InnerRadius = 4.5
  OuterRadius = 5
  Placement = pos=(-5.2,9.00666,54) rot=(0,0,1;2.0944rad)
FEATURE [Part::FeaturePython] Tube130  # WARN: FeaturePython — macro-defined, semantics opaque (R4)
  AttacherType = Attacher::AttachEngine3D
  Height = 1
  InnerRadius = 2.5
  OuterRadius = 3
  Placement = pos=(10.4,0,54) rot=(0,0,1;0rad)
FEATURE [Part::FeaturePython] Tube131  # WARN: FeaturePython — macro-defined, semantics opaque (R4)
  AttacherType = Attacher::AttachEngine3D
  Height = 1
  InnerRadius = 4.5
  OuterRadius = 5
  Placement = pos=(-5.2,-9.00666,54) rot=(0,0,1;4.18879rad)
FEATURE [Part::FeaturePython] Tube132  # WARN: FeaturePython — macro-defined, semantics opaque (R4)
  AttacherType = Attacher::AttachEngine3D
  Height = 1
  InnerRadius = 2.5
  OuterRadius = 3
  Placement = pos=(-5.2,9.00666,54) rot=(0,0,1;2.0944rad)
FEATURE [Part::FeaturePython] Tube133  # WARN: FeaturePython — macro-defined, semantics opaque (R4)
  AttacherType = Attacher::AttachEngine3D
  Height = 1
  InnerRadius = 4.5
  OuterRadius = 5
  Placement = pos=(10.4,0,54) rot=(0,0,1;0rad)
FEATURE [Part::Compound] Compound1186
  Links = -> [Tube133,Tube129,Tube131,Tube130,Tube132,Tube128]
FEATURE [Part::Compound] Compound1188
  Links = -> [Cylinder2708,Cylinder2711,Cylinder2712]
  Placement = pos=(0,0,6) rot=(0,0,1;0rad)
FEATURE [Part::Cut] Cut992
  Base = -> Cut991
  Tool = -> Compound1188
FEATURE [Part::Compound] Compound1189
  Links = -> [Cylinder2710,Cylinder2713,Cylinder2714]
  Placement = pos=(0,0,4) rot=(0,0,1;0rad)
FEATURE [Part::Cut] Cut993
  Base = -> Cut992
  Tool = -> Compound1189
FEATURE [Part::Compound] Compound1190
  Links = -> [Cut993,Compound1186]
  Placement = pos=(0,0,-39) rot=(1,0,0;0rad)
FEATURE [Part::Cylinder] Cylinder2715  label="Válec2685"
  Angle = 360
  AttacherType = Attacher::AttachEngine3D
  Height = 10
  Placement = pos=(20,0,17.5) rot=(0,0,1;0rad)
  Radius = 2.2
FEATURE [Part::Cylinder] Cylinder2716  label="Válec2686"
  Angle = 360
  AttacherType = Attacher::AttachEngine3D
  Height = 20
  Placement = pos=(0,23,8) rot=(0,0,1;0rad)
  Radius = 1
FEATURE [Part::Cylinder] Cylinder2717  label="Válec2687"
  Angle = 360
  AttacherType = Attacher::AttachEngine3D
  Height = 20
  Placement = pos=(-16.26,16.26,8) rot=(0,0,1;0.785398rad)
  Radius = 1
FEATURE [Part::Cylinder] Cylinder2718  label="Válec2688"
  Angle = 360
  AttacherType = Attacher::AttachEngine3D
  Height = 20
  Placement = pos=(-23,0,8) rot=(0,0,1;1.5708rad)
  Radius = 1
FEATURE [Part::Cylinder] Cylinder2719  label="Válec2689"
  Angle = 360
  AttacherType = Attacher::AttachEngine3D
  Height = 20
  Placement = pos=(-16.26,-16.26,8) rot=(0,0,1;2.35619rad)
  Radius = 1
FEATURE [Part::Cylinder] Cylinder2720  label="Válec2690"
  Angle = 360
  AttacherType = Attacher::AttachEngine3D
  Height = 20
  Placement = pos=(4e-15,-23,8) rot=(0,0,1;3.14159rad)
  Radius = 1
FEATURE [Part::Cylinder] Cylinder2721  label="Válec2691"
  Angle = 360
  AttacherType = Attacher::AttachEngine3D
  Height = 20
  Placement = pos=(16.26,-16.26,8) rot=(0,0,1;3.92699rad)
  Radius = 1
FEATURE [Part::Cylinder] Cylinder2722  label="Válec2692"
  Angle = 360
  AttacherType = Attacher::AttachEngine3D
  Height = 20
  Placement = pos=(23,1.1e-14,8) rot=(0,0,-1;1.5708rad)
  Radius = 1
FEATURE [Part::Cylinder] Cylinder2723  label="Válec2693"
  Angle = 360
  AttacherType = Attacher::AttachEngine3D
  Height = 20
  Placement = pos=(16.26,16.26,8) rot=(0,0,-1;0.785398rad)
  Radius = 1
FEATURE [Part::Compound] Compound1191
  Links = -> [Cylinder2716,Cylinder2723,Cylinder2722,Cylinder2720,Cylinder2721,Cylinder2719,Cylinder2717,Cylinder2718]
  Placement = pos=(0,0,-12) rot=(0,0,1;0rad)
FEATURE [Part::Box] Box932  label="Krychle931"
  AttacherType = Attacher::AttachEngine3D
  Height = 1.4
  Length = 4
  Placement = pos=(-2,21,14) rot=(0,0,1;0rad)
  Width = 4
FEATURE [Part::FeaturePython] Tube134  # WARN: FeaturePython — macro-defined, semantics opaque (R4)
  AttacherType = Attacher::AttachEngine3D
  Height = 14
  InnerRadius = 21
  OuterRadius = 25
  Placement = pos=(0,0,10) rot=(0,0,1;0rad)
FEATURE [Part::Torus] Torus005  label="Anuloid005"
  Angle1 = -180
  Angle2 = 180
  Angle3 = 360
  AttacherType = Attacher::AttachEngine3D
  Placement = pos=(0,0,17.5) rot=(0,0,1;0rad)
  Radius1 = 20
  Radius2 = 2.2
FEATURE [Part::Cut] Cut996
  Base = -> Tube134
  Tool = -> Torus005
FEATURE [Part::Box] Box933  label="Krychle932"
  AttacherType = Attacher::AttachEngine3D
  Height = 1.4
  Length = 4
  Placement = pos=(-16.2635,13.435,14) rot=(0,0,1;0.785398rad)
  Width = 4
FEATURE [Part::Box] Box934  label="Krychle933"
  AttacherType = Attacher::AttachEngine3D
  Height = 1.4
  Length = 4
  Placement = pos=(-21,-2,14) rot=(0,0,1;1.5708rad)
  Width = 4
FEATURE [Part::Box] Box935  label="Krychle934"
  AttacherType = Attacher::AttachEngine3D
  Height = 1.4
  Length = 4
  Placement = pos=(-13.435,-16.2635,14) rot=(0,0,1;2.35619rad)
  Width = 4
FEATURE [Part::Box] Box936  label="Krychle935"
  AttacherType = Attacher::AttachEngine3D
  Height = 1.4
  Length = 4
  Placement = pos=(2,-21,14) rot=(0,0,1;3.14159rad)
  Width = 4
FEATURE [Part::Box] Box937  label="Krychle936"
  AttacherType = Attacher::AttachEngine3D
  Height = 1.4
  Length = 4
  Placement = pos=(16.2635,-13.435,14) rot=(0,0,1;3.92699rad)
  Width = 4
FEATURE [Part::Box] Box938  label="Krychle937"
  AttacherType = Attacher::AttachEngine3D
  Height = 1.4
  Length = 4
  Placement = pos=(21,2,14) rot=(0,0,-1;1.5708rad)
  Width = 4
FEATURE [Part::Box] Box939  label="Krychle938"
  AttacherType = Attacher::AttachEngine3D
  Height = 1.4
  Length = 4
  Placement = pos=(13.435,16.2635,14) rot=(0,0,-1;0.785398rad)
  Width = 4
FEATURE [Part::Compound] Compound1192
  Links = -> [Box932,Box933,Box934,Box935,Box936,Box937,Box938,Box939]
  Placement = pos=(0,0,-1) rot=(0,0,1;0rad)
FEATURE [Part::Cut] Cut995
  Base = -> Cut996
  Tool = -> Compound1192
FEATURE [Part::Cut] Cut994
  Base = -> Cut995
  Tool = -> Compound1191
FEATURE [Part::Cut] Cut997
  Base = -> Cut994
  Tool = -> Cylinder2715
FEATURE [Part::Cylinder] Cylinder2724  label="Válec2694"
  Angle = 360
  AttacherType = Attacher::AttachEngine3D
  Height = 10
  Radius = 21
FEATURE [Part::Cylinder] Cylinder2725  label="Válec2695"
  Angle = 360
  AttacherType = Attacher::AttachEngine3D
  Height = 10
  Radius = 21
FEATURE [Part::Box] Box940  label="Krychle939"
  AttacherType = Attacher::AttachEngine3D
  Height = 1.4
  Length = 4
  Placement = pos=(-2,17,-13) rot=(0,0,1;0rad)
  Width = 4
FEATURE [Part::FeaturePython] wormgear045  # WARN: FeaturePython — macro-defined, semantics opaque (R4)
  AttacherType = Attacher::AttachEngine3D
  Placement = pos=(0,0,0) rot=(0,0,1;1.13446rad)
  beta = 47.925
  clearance = 0.25
  diameter = 32.5
  head = 0
  height = 12
  module = 1.2
  pressure_angle = 20
  reverse_pitch = true
  teeth = 30
  version = 0.0.3
FEATURE [Part::Cut] Cut998
  Base = -> Cylinder2724
  Tool = -> wormgear045
FEATURE [Part::FeaturePython] wormgear046  # WARN: FeaturePython — macro-defined, semantics opaque (R4)
  AttacherType = Attacher::AttachEngine3D
  Placement = pos=(0,0,0) rot=(0,0,1;0.997805rad)
  beta = 47.925
  clearance = 0.25
  diameter = 32.5
  head = 0
  height = 12
  module = 1.2
  pressure_angle = 20
  reverse_pitch = false
  teeth = 30
  version = 0.0.3
FEATURE [Part::Cut] Cut999
  Base = -> Cylinder2725
  Placement = pos=(0,0,-10) rot=(0,0,1;0rad)
  Tool = -> wormgear046
FEATURE [Part::Compound] Compound1193  label="gearovina-mini_okruh004"
  Links = -> [Cut999,Cut998]
FEATURE [Part::FeaturePython] Tube135  # WARN: FeaturePython — macro-defined, semantics opaque (R4)
  AttacherType = Attacher::AttachEngine3D
  Height = 6
  InnerRadius = 17
  OuterRadius = 21
  Placement = pos=(0,0,-16) rot=(0,0,1;0rad)
FEATURE [Part::Box] Box941  label="Krychle940"
  AttacherType = Attacher::AttachEngine3D
  Height = 1.4
  Length = 4
  Placement = pos=(-13.435,10.6066,-13) rot=(0,0,1;0.785398rad)
  Width = 4
FEATURE [Part::Box] Box942  label="Krychle941"
  AttacherType = Attacher::AttachEngine3D
  Height = 1.4
  Length = 4
  Placement = pos=(-10.6066,-13.435,-13) rot=(0,0,1;2.35619rad)
  Width = 4
FEATURE [Part::Box] Box943  label="Krychle942"
  AttacherType = Attacher::AttachEngine3D
  Height = 1.4
  Length = 4
  Placement = pos=(2,-17,-13) rot=(0,0,1;3.14159rad)
  Width = 4
FEATURE [Part::Cylinder] Cylinder2726  label="Válec2696"
  Angle = 360
  AttacherType = Attacher::AttachEngine3D
  Height = 10
  Placement = pos=(0,19,-20) rot=(0,0,1;0rad)
  Radius = 1
FEATURE [Part::Box] Box944  label="Krychle943"
  AttacherType = Attacher::AttachEngine3D
  Height = 1.4
  Length = 4
  Placement = pos=(-17,-2,-13) rot=(0,0,1;1.5708rad)
  Width = 4
FEATURE [Part::Box] Box945  label="Krychle944"
  AttacherType = Attacher::AttachEngine3D
  Height = 1.4
  Length = 4
  Placement = pos=(13.435,-10.6066,-13) rot=(0,0,1;3.92699rad)
  Width = 4
FEATURE [Part::Box] Box946  label="Krychle945"
  AttacherType = Attacher::AttachEngine3D
  Height = 1.4
  Length = 4
  Placement = pos=(10.6066,13.435,-13) rot=(0,0,-1;0.785398rad)
  Width = 4
FEATURE [Part::Cylinder] Cylinder2727  label="Válec2697"
  Angle = 360
  AttacherType = Attacher::AttachEngine3D
  Height = 10
  Placement = pos=(-13.435,13.435,-20) rot=(0,0,1;0.785398rad)
  Radius = 1
FEATURE [Part::Cylinder] Cylinder2728  label="Válec2698"
  Angle = 360
  AttacherType = Attacher::AttachEngine3D
  Height = 10
  Placement = pos=(-19,-1e-15,-20) rot=(0,0,1;1.5708rad)
  Radius = 1
FEATURE [Part::Cylinder] Cylinder2729  label="Válec2699"
  Angle = 360
  AttacherType = Attacher::AttachEngine3D
  Height = 10
  Placement = pos=(-13.435,-13.435,-20) rot=(0,0,1;2.35619rad)
  Radius = 1
FEATURE [Part::Cylinder] Cylinder2730  label="Válec2700"
  Angle = 360
  AttacherType = Attacher::AttachEngine3D
  Height = 10
  Placement = pos=(6e-15,-19,-20) rot=(0,0,1;3.14159rad)
  Radius = 1
FEATURE [Part::Cylinder] Cylinder2731  label="Válec2701"
  Angle = 360
  AttacherType = Attacher::AttachEngine3D
  Height = 10
  Placement = pos=(13.435,-13.435,-20) rot=(0,0,1;3.92699rad)
  Radius = 1
FEATURE [Part::Box] Box947  label="Krychle946"
  AttacherType = Attacher::AttachEngine3D
  Height = 1.4
  Length = 4
  Placement = pos=(17,2,-13) rot=(0,0,-1;1.5708rad)
  Width = 4
FEATURE [Part::Compound] Compound1194
  Links = -> [Box940,Box941,Box944,Box942,Box943,Box945,Box947,Box946]
FEATURE [Part::Cut] Cut1000
  Base = -> Tube135
  Tool = -> Compound1194
FEATURE [Part::Cylinder] Cylinder2732  label="Válec2702"
  Angle = 360
  AttacherType = Attacher::AttachEngine3D
  Height = 10
  Placement = pos=(19,8e-15,-20) rot=(0,0,-1;1.5708rad)
  Radius = 1
FEATURE [Part::Cylinder] Cylinder2733  label="Válec2703"
  Angle = 360
  AttacherType = Attacher::AttachEngine3D
  Height = 10
  Placement = pos=(13.435,13.435,-20) rot=(0,0,-1;0.785398rad)
  Radius = 1
FEATURE [Part::Compound] Compound1195
  Links = -> [Cylinder2726,Cylinder2727,Cylinder2728,Cylinder2729,Cylinder2730,Cylinder2731,Cylinder2732,Cylinder2733]
FEATURE [Part::Cut] Cut1001
  Base = -> Cut1000
  Tool = -> Compound1195
FEATURE [Part::Cylinder] Cylinder2734  label="Válec2704"
  Angle = 360
  AttacherType = Attacher::AttachEngine3D
  Height = 10
  Placement = pos=(0,23,4) rot=(0,0,1;0rad)
  Radius = 1
FEATURE [Part::Cylinder] Cylinder2735  label="Válec2705"
  Angle = 360
  AttacherType = Attacher::AttachEngine3D
  Height = 10
  Placement = pos=(16.2635,16.2635,4) rot=(0,0,-1;0.785398rad)
  Radius = 1
FEATURE [Part::Cylinder] Cylinder2736  label="Válec2706"
  Angle = 360
  AttacherType = Attacher::AttachEngine3D
  Height = 10
  Placement = pos=(16.2635,-16.2635,4) rot=(0,0,1;3.92699rad)
  Radius = 1
FEATURE [Part::Cylinder] Cylinder2737  label="Válec2707"
  Angle = 360
  AttacherType = Attacher::AttachEngine3D
  Height = 10
  Placement = pos=(-16.2635,16.2635,4) rot=(0,0,1;0.785398rad)
  Radius = 1
FEATURE [Part::Cylinder] Cylinder2738  label="Válec2708"
  Angle = 360
  AttacherType = Attacher::AttachEngine3D
  Height = 2
  Placement = pos=(-16.2635,-16.2635,4) rot=(0,0,1;2.35619rad)
  Radius = 2
FEATURE [Part::FeaturePython] Tube136  # WARN: FeaturePython — macro-defined, semantics opaque (R4)
  AttacherType = Attacher::AttachEngine3D
  Height = 6
  InnerRadius = 20
  OuterRadius = 25
  Placement = pos=(0,0,4) rot=(0,0,1;0rad)
FEATURE [Part::Cylinder] Cylinder2739  label="Válec2709"
  Angle = 360
  AttacherType = Attacher::AttachEngine3D
  Height = 10
  Placement = pos=(-23,-1e-15,4) rot=(0,0,1;1.5708rad)
  Radius = 1
FEATURE [Part::Cylinder] Cylinder2740  label="Válec2710"
  Angle = 360
  AttacherType = Attacher::AttachEngine3D
  Height = 10
  Placement = pos=(-16.2635,-16.2635,4) rot=(0,0,1;2.35619rad)
  Radius = 1
FEATURE [Part::Cylinder] Cylinder2741  label="Válec2711"
  Angle = 360
  AttacherType = Attacher::AttachEngine3D
  Height = 2
  Placement = pos=(0,23,4) rot=(0,0,1;0rad)
  Radius = 2
FEATURE [Part::Cylinder] Cylinder2742  label="Válec2712"
  Angle = 360
  AttacherType = Attacher::AttachEngine3D
  Height = 10
  Placement = pos=(23,1.1e-14,4) rot=(0,0,-1;1.5708rad)
  Radius = 1
FEATURE [Part::Cylinder] Cylinder2743  label="Válec2713"
  Angle = 360
  AttacherType = Attacher::AttachEngine3D
  Height = 2
  Placement = pos=(-23,-1e-15,4) rot=(0,0,1;1.5708rad)
  Radius = 2
FEATURE [Part::Cylinder] Cylinder2744  label="Válec2714"
  Angle = 360
  AttacherType = Attacher::AttachEngine3D
  Height = 10
  Placement = pos=(4e-15,-23,4) rot=(0,0,1;3.14159rad)
  Radius = 1
FEATURE [Part::Compound] Compound1196
  Links = -> [Cylinder2734,Cylinder2737,Cylinder2739,Cylinder2740,Cylinder2744,Cylinder2736,Cylinder2742,Cylinder2735]
FEATURE [Part::Cylinder] Cylinder2745  label="Válec2715"
  Angle = 360
  AttacherType = Attacher::AttachEngine3D
  Height = 2
  Placement = pos=(16.2635,-16.2635,4) rot=(0,0,1;3.92699rad)
  Radius = 2
FEATURE [Part::Cylinder] Cylinder2746  label="Válec2716"
  Angle = 360
  AttacherType = Attacher::AttachEngine3D
  Height = 2
  Placement = pos=(23,1.1e-14,4) rot=(0,0,-1;1.5708rad)
  Radius = 2
FEATURE [Part::Cylinder] Cylinder2747  label="Válec2717"
  Angle = 360
  AttacherType = Attacher::AttachEngine3D
  Height = 2
  Placement = pos=(16.2635,16.2635,4) rot=(0,0,-1;0.785398rad)
  Radius = 2
FEATURE [Part::Cylinder] Cylinder2748  label="Válec2718"
  Angle = 360
  AttacherType = Attacher::AttachEngine3D
  Height = 2
  Placement = pos=(-16.2635,16.2635,4) rot=(0,0,1;0.785398rad)
  Radius = 2
FEATURE [Part::Cylinder] Cylinder2749  label="Válec2719"
  Angle = 360
  AttacherType = Attacher::AttachEngine3D
  Height = 2
  Placement = pos=(4e-15,-23,4) rot=(0,0,1;3.14159rad)
  Radius = 2
FEATURE [Part::Compound] Compound1197
  Links = -> [Cylinder2741,Cylinder2748,Cylinder2743,Cylinder2738,Cylinder2749,Cylinder2745,Cylinder2746,Cylinder2747]
FEATURE [Part::Cut] Cut1003
  Base = -> Tube136
  Tool = -> Compound1197
FEATURE [Part::Cut] Cut1002
  Base = -> Cut1003
  Tool = -> Compound1196
FEATURE [Part::Torus] Torus006  label="Anuloid006"
  Angle1 = -180
  Angle2 = 180
  Angle3 = 360
  AttacherType = Attacher::AttachEngine3D
  Placement = pos=(0,0,17.5) rot=(0,0,1;0rad)
  Radius1 = 19.75
  Radius2 = 2.2
FEATURE [Part::Box] Box948  label="Krychle947"
  AttacherType = Attacher::AttachEngine3D
  Height = 1.4
  Length = 4
  Placement = pos=(-2,15.5,26) rot=(0,0,1;0rad)
  Width = 5
FEATURE [Part::Box] Box949  label="Krychle948"
  AttacherType = Attacher::AttachEngine3D
  Height = 1.4
  Length = 4
  Placement = pos=(-13.0815,10.253,26) rot=(0,0,1;0.785398rad)
  Width = 4
FEATURE [Part::Box] Box950  label="Krychle949"
  AttacherType = Attacher::AttachEngine3D
  Height = 1.4
  Length = 4
  Placement = pos=(-16.5,-2,26) rot=(0,0,1;1.5708rad)
  Width = 4
FEATURE [Part::Box] Box951  label="Krychle950"
  AttacherType = Attacher::AttachEngine3D
  Height = 1.4
  Length = 4
  Placement = pos=(-10.253,-13.0815,26) rot=(0,0,1;2.35619rad)
  Width = 4
FEATURE [Part::Box] Box952  label="Krychle951"
  AttacherType = Attacher::AttachEngine3D
  Height = 1.4
  Length = 4
  Placement = pos=(2,-16.5,26) rot=(0,0,1;3.14159rad)
  Width = 4
FEATURE [Part::Box] Box953  label="Krychle952"
  AttacherType = Attacher::AttachEngine3D
  Height = 1.4
  Length = 4
  Placement = pos=(13.0815,-10.253,26) rot=(0,0,1;3.92699rad)
  Width = 4
FEATURE [Part::Box] Box954  label="Krychle953"
  AttacherType = Attacher::AttachEngine3D
  Height = 1.4
  Length = 4
  Placement = pos=(16.5,2,26) rot=(0,0,-1;1.5708rad)
  Width = 4
FEATURE [Part::Box] Box955  label="Krychle954"
  AttacherType = Attacher::AttachEngine3D
  Height = 1.4
  Length = 4
  Placement = pos=(10.253,13.0815,26) rot=(0,0,-1;0.785398rad)
  Width = 4
FEATURE [Part::Compound] Compound1199
  Links = -> [Box948,Box949,Box950,Box951,Box952,Box953,Box954,Box955]
  Placement = pos=(0,0,-3) rot=(0,0,1;0rad)
FEATURE [Part::Cylinder] Cylinder2750  label="Válec2720"
  Angle = 360
  AttacherType = Attacher::AttachEngine3D
  Height = 10
  Placement = pos=(0,18.5,26) rot=(0,0,1;0rad)
  Radius = 1
FEATURE [Part::Cylinder] Cylinder2751  label="Válec2721"
  Angle = 360
  AttacherType = Attacher::AttachEngine3D
  Height = 10
  Placement = pos=(-13.08,13.08,26) rot=(0,0,1;0.785398rad)
  Radius = 1
FEATURE [Part::Cylinder] Cylinder2752  label="Válec2722"
  Angle = 360
  AttacherType = Attacher::AttachEngine3D
  Height = 10
  Placement = pos=(-18.5,0,26) rot=(0,0,1;1.5708rad)
  Radius = 1
FEATURE [Part::Cylinder] Cylinder2753  label="Válec2723"
  Angle = 360
  AttacherType = Attacher::AttachEngine3D
  Height = 10
  Placement = pos=(-13.08,-13.08,26) rot=(0,0,1;2.35619rad)
  Radius = 1
FEATURE [Part::Cylinder] Cylinder2754  label="Válec2724"
  Angle = 360
  AttacherType = Attacher::AttachEngine3D
  Height = 10
  Placement = pos=(6e-15,-18.5,26) rot=(0,0,1;3.14159rad)
  Radius = 1
FEATURE [Part::Cylinder] Cylinder2755  label="Válec2725"
  Angle = 360
  AttacherType = Attacher::AttachEngine3D
  Height = 10
  Placement = pos=(13.08,-13.08,26) rot=(0,0,1;3.92699rad)
  Radius = 1
FEATURE [Part::Cylinder] Cylinder2756  label="Válec2726"
  Angle = 360
  AttacherType = Attacher::AttachEngine3D
  Height = 10
  Placement = pos=(18.5,8e-15,26) rot=(0,0,-1;1.5708rad)
  Radius = 1
FEATURE [Part::Cylinder] Cylinder2757  label="Válec2727"
  Angle = 360
  AttacherType = Attacher::AttachEngine3D
  Height = 10
  Placement = pos=(13.08,13.08,26) rot=(0,0,-1;0.785398rad)
  Radius = 1
FEATURE [Part::Compound] Compound1200
  Links = -> [Cylinder2750,Cylinder2751,Cylinder2752,Cylinder2753,Cylinder2754,Cylinder2755,Cylinder2756,Cylinder2757]
  Placement = pos=(0,0,-6) rot=(0,0,1;0rad)
FEATURE [Part::Cut] Cut1004
  Base = -> Compound1190
  Tool = -> Torus006
FEATURE [Part::Cylinder] Cylinder2758  label="Válec2728"
  Angle = 360
  AttacherType = Attacher::AttachEngine3D
  Height = 10
  Placement = pos=(19,8,17.5) rot=(0,0,1;0.392699rad)
  Radius = 2.2
FEATURE [Part::Cut] Cut1005
  Base = -> Cut1004
  Tool = -> Cylinder2758
FEATURE [Part::Box] Box956  label="Krychle955"
  AttacherType = Attacher::AttachEngine3D
  Height = 1.4
  Length = 4
  Placement = pos=(-2,15.5,26) rot=(0,0,1;0rad)
  Width = 5
FEATURE [Part::Box] Box957  label="Krychle956"
  AttacherType = Attacher::AttachEngine3D
  Height = 1.4
  Length = 4
  Placement = pos=(-12.3744,9.54594,26) rot=(0,0,1;0.785398rad)
  Width = 5
FEATURE [Part::Box] Box958  label="Krychle957"
  AttacherType = Attacher::AttachEngine3D
  Height = 1.4
  Length = 4
  Placement = pos=(-15.5,-2,26) rot=(0,0,1;1.5708rad)
  Width = 5
FEATURE [Part::Box] Box959  label="Krychle958"
  AttacherType = Attacher::AttachEngine3D
  Height = 1.4
  Length = 4
  Placement = pos=(-9.54594,-12.3744,26) rot=(0,0,1;2.35619rad)
  Width = 5
FEATURE [Part::Box] Box960  label="Krychle959"
  AttacherType = Attacher::AttachEngine3D
  Height = 1.4
  Length = 4
  Placement = pos=(2,-15.5,26) rot=(0,0,1;3.14159rad)
  Width = 5
FEATURE [Part::Box] Box961  label="Krychle960"
  AttacherType = Attacher::AttachEngine3D
  Height = 1.4
  Length = 4
  Placement = pos=(12.3744,-9.54594,26) rot=(0,0,1;3.92699rad)
  Width = 5
FEATURE [Part::Box] Box962  label="Krychle961"
  AttacherType = Attacher::AttachEngine3D
  Height = 1.4
  Length = 4
  Placement = pos=(15.5,2,26) rot=(0,0,-1;1.5708rad)
  Width = 5
FEATURE [Part::Box] Box963  label="Krychle962"
  AttacherType = Attacher::AttachEngine3D
  Height = 1.4
  Length = 4
  Placement = pos=(9.54594,12.3744,26) rot=(0,0,-1;0.785398rad)
  Width = 5
FEATURE [Part::Box] Box964  label="Krychle963"
  AttacherType = Attacher::AttachEngine3D
  Height = 1.4
  Length = 4
  Placement = pos=(-2,15.5,26) rot=(0,0,1;0rad)
  Width = 5
FEATURE [Part::Compound] Compound1201
  Links = -> [Box956,Box957,Box958,Box959,Box960,Box961,Box962,Box963]
  Placement = pos=(0,0,-5) rot=(0,0,1;0rad)
FEATURE [Part::Cut] Cut1006
  Base = -> Cut1005
  Tool = -> Compound1200
FEATURE [Part::Cut] Cut1007  label="G-mini_quikovina-old"
  Base = -> Cut1006
  Tool = -> Compound1201
FEATURE [Part::Cylinder] Cylinder2759  label="Válec2729"
  Angle = 360
  AttacherType = Attacher::AttachEngine3D
  Height = 16
  Placement = pos=(0,0,50) rot=(0,0,1;0rad)
  Radius = 5
FEATURE [Part::Cylinder] Cylinder2760  label="Válec2730"
  Angle = 360
  AttacherType = Attacher::AttachEngine3D
  Height = 8
  Placement = pos=(0,0,50) rot=(0,0,1;0rad)
  Radius = 16
FEATURE [Part::Cylinder] Cylinder2761  label="Válec2731"
  Angle = 360
  AttacherType = Attacher::AttachEngine3D
  Height = 16
  Placement = pos=(0,0,50) rot=(0,0,1;0rad)
  Radius = 5
FEATURE [Part::FeaturePython] Tube137  # WARN: FeaturePython — macro-defined, semantics opaque (R4)
  AttacherType = Attacher::AttachEngine3D
  Height = 1
  InnerRadius = 2.5
  OuterRadius = 3
  Placement = pos=(-5.2,-9.00666,54) rot=(0,0,1;4.18879rad)
FEATURE [Part::FeaturePython] Tube138  # WARN: FeaturePython — macro-defined, semantics opaque (R4)
  AttacherType = Attacher::AttachEngine3D
  Height = 1
  InnerRadius = 4.5
  OuterRadius = 5
  Placement = pos=(-5.2,9.00666,54) rot=(0,0,1;2.0944rad)
FEATURE [Part::FeaturePython] Tube139  # WARN: FeaturePython — macro-defined, semantics opaque (R4)
  AttacherType = Attacher::AttachEngine3D
  Height = 1
  InnerRadius = 2.5
  OuterRadius = 3
  Placement = pos=(10.4,0,54) rot=(0,0,1;0rad)
FEATURE [Part::FeaturePython] Tube140  # WARN: FeaturePython — macro-defined, semantics opaque (R4)
  AttacherType = Attacher::AttachEngine3D
  Height = 1
  InnerRadius = 4.5
  OuterRadius = 5
  Placement = pos=(-5.2,-9.00666,54) rot=(0,0,1;4.18879rad)
FEATURE [Part::FeaturePython] Tube141  # WARN: FeaturePython — macro-defined, semantics opaque (R4)
  AttacherType = Attacher::AttachEngine3D
  Height = 1
  InnerRadius = 2.5
  OuterRadius = 3
  Placement = pos=(-5.2,9.00666,54) rot=(0,0,1;2.0944rad)
FEATURE [Part::FeaturePython] Tube142  # WARN: FeaturePython — macro-defined, semantics opaque (R4)
  AttacherType = Attacher::AttachEngine3D
  Height = 1
  InnerRadius = 4.5
  OuterRadius = 5
  Placement = pos=(10.4,0,54) rot=(0,0,1;0rad)
FEATURE [Part::Compound] Compound1202
  Links = -> [Tube142,Tube138,Tube140,Tube139,Tube141,Tube137]
FEATURE [Part::Cylinder] Cylinder2762  label="Válec2732"
  Angle = 360
  AttacherType = Attacher::AttachEngine3D
  Height = 5
  Placement = pos=(10.4,0,50) rot=(0,0,1;0rad)
  Radius = 5
FEATURE [Part::Cylinder] Cylinder2763  label="Válec2733"
  Angle = 360
  AttacherType = Attacher::AttachEngine3D
  Height = 5
  Placement = pos=(-5.2,-9.00666,50) rot=(0,0,1;4.18879rad)
  Radius = 5
FEATURE [Part::Cylinder] Cylinder2764  label="Válec2734"
  Angle = 360
  AttacherType = Attacher::AttachEngine3D
  Height = 3
  Placement = pos=(-10.5,3e-15,55) rot=(0,0,1;3.14159rad)
  Radius = 3
FEATURE [Part::Cylinder] Cylinder2765  label="Válec2735"
  Angle = 360
  AttacherType = Attacher::AttachEngine3D
  Height = 5
  Placement = pos=(-5.2,9.00666,50) rot=(0,0,1;2.0944rad)
  Radius = 5
FEATURE [Part::Compound] Compound1203
  Links = -> [Cylinder2762,Cylinder2763,Cylinder2765,Cylinder2761]
FEATURE [Part::Cut] Cut1008
  Base = -> Cylinder2760
  Tool = -> Compound1203
FEATURE [Part::Cylinder] Cylinder2766  label="Válec2736"
  Angle = 360
  AttacherType = Attacher::AttachEngine3D
  Height = 20
  Placement = pos=(-10.5,0.00186,40) rot=(0,0,1;3.14159rad)
  Radius = 1.5
FEATURE [Part::Cylinder] Cylinder2767  label="Válec2737"
  Angle = 360
  AttacherType = Attacher::AttachEngine3D
  Height = 3
  Placement = pos=(5.25,-9.09327,55) rot=(0,0,-1;1.0472rad)
  Radius = 3
FEATURE [Part::Cylinder] Cylinder2768  label="Válec2738"
  Angle = 360
  AttacherType = Attacher::AttachEngine3D
  Height = 3
  Placement = pos=(5.25,9.09327,55) rot=(0,0,1;1.0472rad)
  Radius = 3
FEATURE [Part::Compound] Compound1204
  Links = -> [Cylinder2764,Cylinder2767,Cylinder2768]
FEATURE [Part::Cylinder] Cylinder2769  label="Válec2739"
  Angle = 360
  AttacherType = Attacher::AttachEngine3D
  Height = 20
  Placement = pos=(5.24839,-9.0942,40) rot=(0,0,-1;1.0472rad)
  Radius = 1.5
FEATURE [Part::Cylinder] Cylinder2770  label="Válec2740"
  Angle = 360
  AttacherType = Attacher::AttachEngine3D
  Height = 20
  Placement = pos=(5.25161,9.09234,40) rot=(0,0,1;1.0472rad)
  Radius = 1.5
FEATURE [Part::Compound] Compound1205
  Links = -> [Cylinder2766,Cylinder2769,Cylinder2770]
FEATURE [Part::Cut] Cut1009
  Base = -> Cut1008
  Tool = -> Compound1204
FEATURE [Part::Cut] Cut1010
  Base = -> Cut1009
  Tool = -> Compound1205
FEATURE [Part::Compound] Compound1206
  Links = -> [Cut1010,Compound1202]
  Placement = pos=(0,0,-39) rot=(0,0,1;0rad)
FEATURE [Part::Compound] Compound1207  label="G-mini_pikovina"
  Links = -> [Compound053,Compound1206]
  Placement = pos=(0,0,0) rot=(1,0,0;3.14159rad)
FEATURE [Part::FeaturePython] Tube  label="ZKL-6001"  # WARN: FeaturePython — macro-defined, semantics opaque (R4)
  AttacherType = Attacher::AttachEngine3D
  Height = 8
  InnerRadius = 6
  OuterRadius = 14
  Placement = pos=(0,0,-28) rot=(0,0,1;0rad)
FEATURE [Part::FeaturePython] Tube143  # WARN: FeaturePython — macro-defined, semantics opaque (R4)
  AttacherType = Attacher::AttachEngine3D
  Height = 64
  InnerRadius = 2
  OuterRadius = 21
  Placement = pos=(0,61,37) rot=(1,0,0;1.5708rad)
FEATURE [Part::FeaturePython] Tube144  # WARN: FeaturePython — macro-defined, semantics opaque (R4)
  AttacherType = Attacher::AttachEngine3D
  Height = 26
  InnerRadius = 2
  OuterRadius = 25
  Placement = pos=(0,-3,37) rot=(1,0,0;1.5708rad)
FEATURE [Part::Box] Box974  label="Krychle973"
  AttacherType = Attacher::AttachEngine3D
  Height = 18
  Length = 30
  Placement = pos=(-15,-17,11) rot=(0,0,1;0rad)
  Width = 8
FEATURE [Part::Box] Box975  label="Krychle974"
  AttacherType = Attacher::AttachEngine3D
  Height = 6
  Length = 2
  Placement = pos=(-12,-4,10) rot=(0,0,1;0rad)
  Width = 6
FEATURE [Part::Box] Box976  label="Krychle975"
  AttacherType = Attacher::AttachEngine3D
  Height = 6
  Length = 2
  Placement = pos=(10,26,10) rot=(0,0,1;0rad)
  Width = 6
FEATURE [Part::Box] Box977  label="Krychle976"
  AttacherType = Attacher::AttachEngine3D
  Height = 6
  Length = 2
  Placement = pos=(-12,26,10) rot=(0,0,1;0rad)
  Width = 6
FEATURE [Part::Box] Box978  label="Krychle977"
  AttacherType = Attacher::AttachEngine3D
  Height = 6
  Length = 2
  Placement = pos=(10,12,10) rot=(0,0,1;0rad)
  Width = 6
FEATURE [Part::Box] Box979  label="Krychle978"
  AttacherType = Attacher::AttachEngine3D
  Height = 6
  Length = 2
  Placement = pos=(-12,12,10) rot=(0,0,1;0rad)
  Width = 6
FEATURE [Part::Cylinder] Cylinder2791  label="Válec2761"
  Angle = 360
  AttacherType = Attacher::AttachEngine3D
  Height = 30
  Radius = 38
FEATURE [Part::Box] Box980  label="Krychle979"
  AttacherType = Attacher::AttachEngine3D
  Height = 18
  Length = 30
  Placement = pos=(-15,-17,11) rot=(0,0,1;0rad)
  Width = 64
FEATURE [Part::Cut] Cut1049
  Base = -> Box980
  Tool = -> Tube144
FEATURE [Part::Cut] Cut1050
  Base = -> Cut1049
  Tool = -> Tube143
FEATURE [Part::Box] Box981  label="Krychle980"
  AttacherType = Attacher::AttachEngine3D
  Height = 6
  Length = 2
  Placement = pos=(10,-4,10) rot=(0,0,1;0rad)
  Width = 6
FEATURE [Part::Compound] Compound1243
  Links = -> [Box981,Box975,Box976,Box977,Box978,Box979]
FEATURE [Part::Cut] Cut1051
  Base = -> Cut1050
  Tool = -> Compound1243
FEATURE [Part::Common] Common007
  Base = -> Cut1051
  Tool = -> Cylinder2791
FEATURE [Part::Common] Common008
  Base = -> Box974
  Tool = -> Common007
FEATURE [Part::Cylinder] Cylinder2792  label="Válec2762"
  Angle = 360
  AttacherType = Attacher::AttachEngine3D
  Height = 64
  Placement = pos=(-26,-13,14) rot=(0,1,0;1.5708rad)
  Radius = 1.5
FEATURE [Part::Cut] Cut1052
  Base = -> Common008
  Placement = pos=(0,37,27) rot=(1,0,0;1.5708rad)
  Tool = -> Cylinder2792
FEATURE [Part::Cylinder] Cylinder2793  label="Válec2763"
  Angle = 360
  AttacherType = Attacher::AttachEngine3D
  Height = 24
  Placement = pos=(-28,23,14) rot=(0,1,0;1.5708rad)
  Radius = 1.5
FEATURE [Part::Cylinder] Cylinder2794  label="Válec2764"
  Angle = 360
  AttacherType = Attacher::AttachEngine3D
  Height = 24
  Placement = pos=(4,23,14) rot=(0,1,0;1.5708rad)
  Radius = 1.5
FEATURE [Part::Box] Box  label="Krychle"
  AttacherType = Attacher::AttachEngine3D
  Height = 6
  Length = 2
  Placement = pos=(10,20,11) rot=(0,0,1;0rad)
  Width = 6
FEATURE [Part::Box] Box982  label="Krychle981"
  AttacherType = Attacher::AttachEngine3D
  Height = 6
  Length = 2
  Placement = pos=(-12,20,11) rot=(0,0,1;0rad)
  Width = 6
FEATURE [Part::Compound] Compound1244
  Links = -> [Box,Box982]
FEATURE [Part::Compound] Compound1245
  Links = -> [Cylinder2793,Cylinder2794]
FEATURE [Part::Cylinder] Cylinder2795  label="Válec2765"
  Angle = 360
  AttacherType = Attacher::AttachEngine3D
  Height = 24
  Placement = pos=(-28,23,14) rot=(0,1,0;1.5708rad)
  Radius = 1.5
FEATURE [Part::Cylinder] Cylinder2796  label="Válec2766"
  Angle = 360
  AttacherType = Attacher::AttachEngine3D
  Height = 24
  Placement = pos=(4,23,14) rot=(0,1,0;1.5708rad)
  Radius = 1.5
FEATURE [Part::Box] Box983  label="Krychle982"
  AttacherType = Attacher::AttachEngine3D
  Height = 6
  Length = 2
  Placement = pos=(10,20,11) rot=(0,0,1;0rad)
  Width = 6
FEATURE [Part::Box] Box984  label="Krychle983"
  AttacherType = Attacher::AttachEngine3D
  Height = 6
  Length = 2
  Placement = pos=(-12,20,11) rot=(0,0,1;0rad)
  Width = 6
FEATURE [Part::Compound] Compound1246
  Links = -> [Cylinder2795,Cylinder2796]
FEATURE [Part::Compound] Compound1247
  Links = -> [Box983,Box984]
FEATURE [Part::Cut] Cut1053
  Base = -> Cut1052
  Tool = -> Compound1244
FEATURE [Part::Cut] Cut1054
  Base = -> Cut1053
  Tool = -> Compound1245
FEATURE [Part::Cut] Cut1055
  Base = -> Cut997
  Tool = -> Compound1246
FEATURE [Part::Cut] Cut1056
  Base = -> Cut1055
  Tool = -> Compound1247
FEATURE [Part::Compound] Compound1248  label="G-mini_bearing-ring"
  Links = -> [Cut1054,Cut1056]
FEATURE [Mesh::Feature] Mesh  label="G-mini_bearing-ring (Meshed)"
FEATURE [Part::FeaturePython] Tube145  # WARN: FeaturePython — macro-defined, semantics opaque (R4)
  AttacherType = Attacher::AttachEngine3D
  Height = 26
  InnerRadius = 2
  OuterRadius = 25
  Placement = pos=(0,-3,37) rot=(1,0,0;1.5708rad)
FEATURE [Part::FeaturePython] Tube146  # WARN: FeaturePython — macro-defined, semantics opaque (R4)
  AttacherType = Attacher::AttachEngine3D
  Height = 64
  InnerRadius = 2
  OuterRadius = 21
  Placement = pos=(0,61,37) rot=(1,0,0;1.5708rad)
FEATURE [Part::Box] Box985  label="Krychle984"
  AttacherType = Attacher::AttachEngine3D
  Height = 6
  Length = 2
  Placement = pos=(10,26,10) rot=(0,0,1;0rad)
  Width = 6
FEATURE [Part::Box] Box986  label="Krychle985"
  AttacherType = Attacher::AttachEngine3D
  Height = 6
  Length = 2
  Placement = pos=(-12,26,10) rot=(0,0,1;0rad)
  Width = 6
FEATURE [Part::Box] Box987  label="Krychle986"
  AttacherType = Attacher::AttachEngine3D
  Height = 6
  Length = 2
  Placement = pos=(8,9,11) rot=(0,0,1;0rad)
  Width = 6
FEATURE [Part::Box] Box988  label="Krychle987"
  AttacherType = Attacher::AttachEngine3D
  Height = 6
  Length = 2
  Placement = pos=(-10,9,10) rot=(0,0,1;0rad)
  Width = 6
FEATURE [Part::Cylinder] Cylinder2797  label="Válec2767"
  Angle = 360
  AttacherType = Attacher::AttachEngine3D
  Height = 30
  Radius = 38
FEATURE [Part::Box] Box989  label="Krychle988"
  AttacherType = Attacher::AttachEngine3D
  Height = 18
  Length = 30
  Placement = pos=(-15,-17,11) rot=(0,0,1;0rad)
  Width = 64
FEATURE [Part::Cut] Cut1057
  Base = -> Box989
  Tool = -> Tube145
FEATURE [Part::Cut] Cut1058
  Base = -> Cut1057
  Tool = -> Tube146
FEATURE [Part::Box] Box990  label="Krychle989"
  AttacherType = Attacher::AttachEngine3D
  Height = 6
  Length = 2
  Placement = pos=(8,-4,10) rot=(0,0,1;0rad)
  Width = 6
FEATURE [Part::Cylinder] Cylinder2798  label="Válec2768"
  Angle = 360
  AttacherType = Attacher::AttachEngine3D
  Height = 64
  Placement = pos=(-26,12,14) rot=(0,1,0;1.5708rad)
  Radius = 1.5
FEATURE [Part::Cylinder] Cylinder2799  label="Válec2769"
  Angle = 360
  AttacherType = Attacher::AttachEngine3D
  Height = 64
  Placement = pos=(-26,-1,14) rot=(0,1,0;1.5708rad)
  Radius = 1.5
FEATURE [Part::Box] Box991  label="Krychle990"
  AttacherType = Attacher::AttachEngine3D
  Height = 18
  Length = 30
  Placement = pos=(-15,-9,11) rot=(0,0,1;0rad)
  Width = 26
FEATURE [Part::Box] Box992  label="Krychle991"
  AttacherType = Attacher::AttachEngine3D
  Height = 6
  Length = 2
  Placement = pos=(-10,-4,10) rot=(0,0,1;0rad)
  Width = 6
FEATURE [Part::Compound] Compound1249
  Links = -> [Box990,Box992,Box985,Box986,Box987,Box988]
FEATURE [Part::Cut] Cut1059
  Base = -> Cut1058
  Tool = -> Compound1249
FEATURE [Part::Common] Common009
  Base = -> Cut1059
  Tool = -> Cylinder2797
FEATURE [Part::Common] Common010
  Base = -> Box991
  Tool = -> Common009
FEATURE [Part::Compound] Compound1250
  Links = -> [Cylinder2799,Cylinder2798]
FEATURE [Part::Cut] Cut1060
  Base = -> Common010
  Placement = pos=(0,37,1) rot=(0,0.707107,-0.707107;3.14159rad)
  Tool = -> Compound1250
FEATURE [Part::Box] Box993  label="Krychle992"
  AttacherType = Attacher::AttachEngine3D
  Height = 6
  Length = 2
  Placement = pos=(8,20,-1) rot=(0,0,1;0rad)
  Width = 6
FEATURE [Part::Box] Box994  label="Krychle993"
  AttacherType = Attacher::AttachEngine3D
  Height = 6
  Length = 2
  Placement = pos=(-10,20,-1) rot=(0,0,1;0rad)
  Width = 6
FEATURE [Part::Box] Box995  label="Krychle994"
  AttacherType = Attacher::AttachEngine3D
  Height = 6
  Length = 2
  Placement = pos=(8,20,-14) rot=(0,0,1;0rad)
  Width = 6
FEATURE [Part::Box] Box996  label="Krychle995"
  AttacherType = Attacher::AttachEngine3D
  Height = 6
  Length = 2
  Placement = pos=(-10,20,-14) rot=(0,0,1;0rad)
  Width = 6
FEATURE [Part::Compound] Compound1251
  Links = -> [Box993,Box994,Box995,Box996]
FEATURE [Part::Cylinder] Cylinder2800  label="Válec2770"
  Angle = 360
  AttacherType = Attacher::AttachEngine3D
  Height = 64
  Placement = pos=(-28,23,2) rot=(0,1,0;1.5708rad)
  Radius = 1.5
FEATURE [Part::Cylinder] Cylinder2801  label="Válec2771"
  Angle = 360
  AttacherType = Attacher::AttachEngine3D
  Height = 64
  Placement = pos=(-28,23,-11) rot=(0,1,0;1.5708rad)
  Radius = 1.5
FEATURE [Part::Compound] Compound1252
  Links = -> [Cylinder2800,Cylinder2801]
FEATURE [Part::Cut] Cut1061
  Base = -> Cut1002
  Tool = -> Compound1251
FEATURE [Part::Box] Box997  label="Krychle996"
  AttacherType = Attacher::AttachEngine3D
  Height = 6
  Length = 2
  Placement = pos=(8,20,-1) rot=(0,0,1;0rad)
  Width = 6
FEATURE [Part::Box] Box998  label="Krychle997"
  AttacherType = Attacher::AttachEngine3D
  Height = 6
  Length = 2
  Placement = pos=(-10,20,-1) rot=(0,0,1;0rad)
  Width = 6
FEATURE [Part::Box] Box999  label="Krychle998"
  AttacherType = Attacher::AttachEngine3D
  Height = 6
  Length = 2
  Placement = pos=(8,20,-14) rot=(0,0,1;0rad)
  Width = 6
FEATURE [Part::Box] Box1000  label="Krychle999"
  AttacherType = Attacher::AttachEngine3D
  Height = 6
  Length = 2
  Placement = pos=(-10,20,-14) rot=(0,0,1;0rad)
  Width = 6
FEATURE [Part::Compound] Compound1253
  Links = -> [Box997,Box998,Box999,Box1000]
FEATURE [Part::Box] Box1001  label="Krychle1000"
  AttacherType = Attacher::AttachEngine3D
  Height = 6
  Length = 2
  Placement = pos=(8,20,-1) rot=(0,0,1;0rad)
  Width = 6
FEATURE [Part::Box] Box1002  label="Krychle1001"
  AttacherType = Attacher::AttachEngine3D
  Height = 6
  Length = 2
  Placement = pos=(-10,20,-1) rot=(0,0,1;0rad)
  Width = 6
FEATURE [Part::Box] Box1003  label="Krychle1002"
  AttacherType = Attacher::AttachEngine3D
  Height = 6
  Length = 2
  Placement = pos=(8,20,-14) rot=(0,0,1;0rad)
  Width = 6
FEATURE [Part::Box] Box1004  label="Krychle1003"
  AttacherType = Attacher::AttachEngine3D
  Height = 6
  Length = 2
  Placement = pos=(-10,20,-14) rot=(0,0,1;0rad)
  Width = 6
FEATURE [Part::Compound] Compound1254
  Links = -> [Box1001,Box1002,Box1003,Box1004]
FEATURE [Part::Cut] Cut1062
  Base = -> Compound1193
  Tool = -> Compound1253
FEATURE [Part::Cut] Cut1063
  Base = -> Cut1001
  Tool = -> Compound1254
FEATURE [Part::Compound] Compound1255
  Links = -> [Cut1061,Cut1062,Cut1063]
FEATURE [Part::Box] Box1005  label="Krychle1004"
  AttacherType = Attacher::AttachEngine3D
  Height = 20
  Length = 8
  Placement = pos=(-4,-22,-16) rot=(0,0,1;0rad)
  Width = 64
FEATURE [Part::Cylinder] Cylinder2802  label="Válec2772"
  Angle = 360
  AttacherType = Attacher::AttachEngine3D
  Height = 32
  Placement = pos=(0,23,-28) rot=(0,0,1;0rad)
  Radius = 4
FEATURE [Part::Cylinder] Cylinder2803  label="Válec2773"
  Angle = 360
  AttacherType = Attacher::AttachEngine3D
  Height = 32
  Placement = pos=(16.2635,16.2635,-28) rot=(0,0,-1;0.785398rad)
  Radius = 4
FEATURE [Part::Cylinder] Cylinder2804  label="Válec2774"
  Angle = 360
  AttacherType = Attacher::AttachEngine3D
  Height = 32
  Placement = pos=(-16.2635,16.2635,-28) rot=(0,0,1;0.785398rad)
  Radius = 4
FEATURE [Part::Compound] Compound1256
  Links = -> [Cylinder2803,Cylinder2804]
FEATURE [Part::Cut] Cut1064
  Base = -> Cut1060
  Tool = -> Compound1256
FEATURE [Part::Cut] Cut1065
  Base = -> Cut1064
  Tool = -> Box1005
FEATURE [Part::Box] Box1006  label="Krychle1005"
  AttacherType = Attacher::AttachEngine3D
  Height = 20
  Length = 30
  Placement = pos=(-15,-17,-16) rot=(0,0,1;0rad)
  Width = 64
FEATURE [Part::Box] Box1007  label="Krychle1006"
  AttacherType = Attacher::AttachEngine3D
  Height = 6
  Length = 30
  Placement = pos=(-15,-17,4) rot=(0,0,1;0rad)
  Width = 64
FEATURE [Part::Box] Box1008  label="Krychle1007"
  AttacherType = Attacher::AttachEngine3D
  Height = 6
  Length = 2
  Placement = pos=(10,26,10) rot=(0,0,1;0rad)
  Width = 6
FEATURE [Part::FeaturePython] Tube147  # WARN: FeaturePython — macro-defined, semantics opaque (R4)
  AttacherType = Attacher::AttachEngine3D
  Height = 26
  InnerRadius = 2
  OuterRadius = 25
  Placement = pos=(0,-3,37) rot=(1,0,0;1.5708rad)
FEATURE [Part::FeaturePython] Tube148  # WARN: FeaturePython — macro-defined, semantics opaque (R4)
  AttacherType = Attacher::AttachEngine3D
  Height = 64
  InnerRadius = 2
  OuterRadius = 21
  Placement = pos=(0,61,37) rot=(1,0,0;1.5708rad)
FEATURE [Part::Box] Box1009  label="Krychle1008"
  AttacherType = Attacher::AttachEngine3D
  Height = 6
  Length = 2
  Placement = pos=(-12,26,10) rot=(0,0,1;0rad)
  Width = 6
FEATURE [Part::Box] Box1010  label="Krychle1009"
  AttacherType = Attacher::AttachEngine3D
  Height = 6
  Length = 2
  Placement = pos=(8,9,11) rot=(0,0,1;0rad)
  Width = 6
FEATURE [Part::Box] Box1011  label="Krychle1010"
  AttacherType = Attacher::AttachEngine3D
  Height = 6
  Length = 2
  Placement = pos=(-10,9,10) rot=(0,0,1;0rad)
  Width = 6
FEATURE [Part::Cylinder] Cylinder2805  label="Válec2775"
  Angle = 360
  AttacherType = Attacher::AttachEngine3D
  Height = 30
  Radius = 38
FEATURE [Part::Box] Box1012  label="Krychle1011"
  AttacherType = Attacher::AttachEngine3D
  Height = 18
  Length = 30
  Placement = pos=(-15,-17,11) rot=(0,0,1;0rad)
  Width = 64
FEATURE [Part::Cut] Cut1066
  Base = -> Box1012
  Tool = -> Tube147
FEATURE [Part::Cut] Cut1067
  Base = -> Cut1066
  Tool = -> Tube148
FEATURE [Part::Box] Box1013  label="Krychle1012"
  AttacherType = Attacher::AttachEngine3D
  Height = 6
  Length = 2
  Placement = pos=(8,-4,10) rot=(0,0,1;0rad)
  Width = 6
FEATURE [Part::Cylinder] Cylinder2806  label="Válec2776"
  Angle = 360
  AttacherType = Attacher::AttachEngine3D
  Height = 64
  Placement = pos=(-26,12,14) rot=(0,1,0;1.5708rad)
  Radius = 1.5
FEATURE [Part::Cylinder] Cylinder2807  label="Válec2777"
  Angle = 360
  AttacherType = Attacher::AttachEngine3D
  Height = 64
  Placement = pos=(-26,-1,14) rot=(0,1,0;1.5708rad)
  Radius = 1.5
FEATURE [Part::Compound] Compound1257
  Links = -> [Cylinder2807,Cylinder2806]
FEATURE [Part::Box] Box1014  label="Krychle1013"
  AttacherType = Attacher::AttachEngine3D
  Height = 18
  Length = 30
  Placement = pos=(-15,-9,11) rot=(0,0,1;0rad)
  Width = 26
FEATURE [Part::Box] Box1015  label="Krychle1014"
  AttacherType = Attacher::AttachEngine3D
  Height = 6
  Length = 2
  Placement = pos=(-10,-4,10) rot=(0,0,1;0rad)
  Width = 6
FEATURE [Part::Compound] Compound1258
  Links = -> [Box1013,Box1015,Box1008,Box1009,Box1010,Box1011]
FEATURE [Part::Cut] Cut1068
  Base = -> Cut1067
  Tool = -> Compound1258
FEATURE [Part::Common] Common011
  Base = -> Cut1068
  Tool = -> Cylinder2805
FEATURE [Part::Common] Common012
  Base = -> Box1014
  Tool = -> Common011
FEATURE [Part::Cylinder] Cylinder2808  label="Válec2778"
  Angle = 360
  AttacherType = Attacher::AttachEngine3D
  Height = 32
  Placement = pos=(16.2635,16.2635,-28) rot=(0,0,-1;0.785398rad)
  Radius = 4
FEATURE [Part::Cylinder] Cylinder2809  label="Válec2779"
  Angle = 360
  AttacherType = Attacher::AttachEngine3D
  Height = 32
  Placement = pos=(-16.2635,16.2635,-28) rot=(0,0,1;0.785398rad)
  Radius = 4
FEATURE [Part::Cut] Cut1069
  Base = -> Common012
  Placement = pos=(0,37,1) rot=(0,0.707107,-0.707107;3.14159rad)
  Tool = -> Compound1257
FEATURE [Part::Compound] Compound1259
  Links = -> [Cylinder2808,Cylinder2809]
FEATURE [Part::Cut] Cut1070
  Base = -> Cut1069
  Tool = -> Compound1259
FEATURE [Part::Box] Box1016  label="Krychle1015"
  AttacherType = Attacher::AttachEngine3D
  Height = 20
  Length = 8
  Placement = pos=(-4,-22,-16) rot=(0,0,1;0rad)
  Width = 64
FEATURE [Part::Cut] Cut1071
  Base = -> Cut1070
  Tool = -> Box1016
FEATURE [Part::Common] Common013
  Base = -> Cut1065
  Tool = -> Box1006
FEATURE [Part::Common] Common014
  Base = -> Box1007
  Tool = -> Cut1071
FEATURE [Part::Compound] Compound1260
  Links = -> [Common013,Common014]
FEATURE [Part::Compound] Compound1261  label="G-mini_monoblock-m1.2"
  Links = -> [Compound1255,Compound1260]
FEATURE [Part::Box] Box1017  label="Krychle1016"
  AttacherType = Attacher::AttachEngine3D
  Height = 6
  Length = 2
  Placement = pos=(10,26,10) rot=(0,0,1;0rad)
  Width = 6
FEATURE [Part::FeaturePython] Tube149  # WARN: FeaturePython — macro-defined, semantics opaque (R4)
  AttacherType = Attacher::AttachEngine3D
  Height = 26
  InnerRadius = 2
  OuterRadius = 25
  Placement = pos=(0,-3,37) rot=(1,0,0;1.5708rad)
FEATURE [Part::FeaturePython] Tube150  # WARN: FeaturePython — macro-defined, semantics opaque (R4)
  AttacherType = Attacher::AttachEngine3D
  Height = 64
  InnerRadius = 2
  OuterRadius = 21
  Placement = pos=(0,61,37) rot=(1,0,0;1.5708rad)
FEATURE [Part::Box] Box1018  label="Krychle1017"
  AttacherType = Attacher::AttachEngine3D
  Height = 6
  Length = 2
  Placement = pos=(-12,26,10) rot=(0,0,1;0rad)
  Width = 6
FEATURE [Part::Box] Box1019  label="Krychle1018"
  AttacherType = Attacher::AttachEngine3D
  Height = 6
  Length = 2
  Placement = pos=(8,9,11) rot=(0,0,1;0rad)
  Width = 6
FEATURE [Part::Box] Box1020  label="Krychle1019"
  AttacherType = Attacher::AttachEngine3D
  Height = 6
  Length = 2
  Placement = pos=(-10,9,10) rot=(0,0,1;0rad)
  Width = 6
FEATURE [Part::Cylinder] Cylinder2810  label="Válec2780"
  Angle = 360
  AttacherType = Attacher::AttachEngine3D
  Height = 30
  Radius = 38
FEATURE [Part::Box] Box1021  label="Krychle1020"
  AttacherType = Attacher::AttachEngine3D
  Height = 18
  Length = 30
  Placement = pos=(-15,-17,11) rot=(0,0,1;0rad)
  Width = 64
FEATURE [Part::Cut] Cut1072
  Base = -> Box1021
  Tool = -> Tube149
FEATURE [Part::Cut] Cut1073
  Base = -> Cut1072
  Tool = -> Tube150
FEATURE [Part::Box] Box1022  label="Krychle1021"
  AttacherType = Attacher::AttachEngine3D
  Height = 6
  Length = 2
  Placement = pos=(8,-4,10) rot=(0,0,1;0rad)
  Width = 6
FEATURE [Part::Cylinder] Cylinder2811  label="Válec2781"
  Angle = 360
  AttacherType = Attacher::AttachEngine3D
  Height = 64
  Placement = pos=(-26,12,14) rot=(0,1,0;1.5708rad)
  Radius = 1.5
FEATURE [Part::Cylinder] Cylinder2812  label="Válec2782"
  Angle = 360
  AttacherType = Attacher::AttachEngine3D
  Height = 64
  Placement = pos=(-26,-1,14) rot=(0,1,0;1.5708rad)
  Radius = 1.5
FEATURE [Part::Compound] Compound1262
  Links = -> [Cylinder2812,Cylinder2811]
FEATURE [Part::Box] Box1023  label="Krychle1022"
  AttacherType = Attacher::AttachEngine3D
  Height = 18
  Length = 30
  Placement = pos=(-15,-9,11) rot=(0,0,1;0rad)
  Width = 26
FEATURE [Part::Box] Box1024  label="Krychle1023"
  AttacherType = Attacher::AttachEngine3D
  Height = 6
  Length = 2
  Placement = pos=(-10,-4,10) rot=(0,0,1;0rad)
  Width = 6
FEATURE [Part::Compound] Compound1263
  Links = -> [Box1022,Box1024,Box1017,Box1018,Box1019,Box1020]
FEATURE [Part::Cut] Cut1074
  Base = -> Cut1073
  Tool = -> Compound1263
FEATURE [Part::Common] Common015
  Base = -> Cut1074
  Tool = -> Cylinder2810
FEATURE [Part::Common] Common016
  Base = -> Box1023
  Tool = -> Common015
FEATURE [Part::Box] Box1025  label="Krychle1024"
  AttacherType = Attacher::AttachEngine3D
  Height = 20
  Length = 30
  Placement = pos=(-15,-17,-16) rot=(0,0,1;0rad)
  Width = 64
FEATURE [Part::Cylinder] Cylinder2813  label="Válec2783"
  Angle = 360
  AttacherType = Attacher::AttachEngine3D
  Height = 32
  Placement = pos=(16.2635,16.2635,-28) rot=(0,0,-1;0.785398rad)
  Radius = 4
FEATURE [Part::Cylinder] Cylinder2814  label="Válec2784"
  Angle = 360
  AttacherType = Attacher::AttachEngine3D
  Height = 32
  Placement = pos=(-16.2635,16.2635,-28) rot=(0,0,1;0.785398rad)
  Radius = 4
FEATURE [Part::Cut] Cut1075
  Base = -> Common016
  Placement = pos=(0,37,1) rot=(0,0.707107,-0.707107;3.14159rad)
  Tool = -> Compound1262
FEATURE [Part::Compound] Compound1264
  Links = -> [Cylinder2813,Cylinder2814]
FEATURE [Part::Cut] Cut1076
  Base = -> Cut1075
  Tool = -> Compound1264
FEATURE [Part::Box] Box1026  label="Krychle1025"
  AttacherType = Attacher::AttachEngine3D
  Height = 20
  Length = 8
  Placement = pos=(-4,-22,-16) rot=(0,0,1;0rad)
  Width = 64
FEATURE [Part::Cut] Cut1077
  Base = -> Cut1076
  Tool = -> Box1026
FEATURE [Part::Common] Common017
  Base = -> Cut1077
  Placement = pos=(0,0,-15) rot=(0,0,1;0rad)
  Tool = -> Box1025
FEATURE [Part::Box] Box1027  label="Krychle1026"
  AttacherType = Attacher::AttachEngine3D
  Height = 5
  Length = 30
  Placement = pos=(-15,-17,-22) rot=(0,0,1;0rad)
  Width = 64
FEATURE [Part::Common] Common018
  Base = -> Common017
  Placement = pos=(0,0,1) rot=(0,0,1;0rad)
  Tool = -> Box1027
FEATURE [Part::Box] Box055  label="Krychle055"
  AttacherType = Attacher::AttachEngine3D
  Height = 4
  Length = 46.3
  Placement = pos=(-23.15,-23.15,-25) rot=(0,0,1;0rad)
  Width = 46.3
FEATURE [Part::Cylinder] Cylinder168  label="Válec168"
  Angle = 360
  AttacherType = Attacher::AttachEngine3D
  Height = 10
  Placement = pos=(-13.44,13.44,-24) rot=(0,0,1;0.785398rad)
  Radius = 1
FEATURE [Part::Cylinder] Cylinder169  label="Válec169"
  Angle = 360
  AttacherType = Attacher::AttachEngine3D
  Height = 10
  Placement = pos=(-19,0,-24) rot=(0,0,1;1.5708rad)
  Radius = 1
FEATURE [Part::Cylinder] Cylinder170  label="Válec170"
  Angle = 360
  AttacherType = Attacher::AttachEngine3D
  Height = 10
  Placement = pos=(0,19,-24) rot=(0,0,1;0rad)
  Radius = 1
FEATURE [Part::Cylinder] Cylinder171  label="Válec171"
  Angle = 360
  AttacherType = Attacher::AttachEngine3D
  Height = 10
  Placement = pos=(-13.44,-13.44,-24) rot=(0,0,1;2.35619rad)
  Radius = 1
FEATURE [Part::Cylinder] Cylinder172  label="Válec172"
  Angle = 360
  AttacherType = Attacher::AttachEngine3D
  Height = 10
  Placement = pos=(6e-15,-19,-24) rot=(0,0,1;3.14159rad)
  Radius = 1
FEATURE [Part::Cylinder] Cylinder173  label="Válec173"
  Angle = 360
  AttacherType = Attacher::AttachEngine3D
  Height = 10
  Placement = pos=(13.44,-13.44,-24) rot=(0,0,1;3.92699rad)
  Radius = 1
FEATURE [Part::Cylinder] Cylinder174  label="Válec174"
  Angle = 360
  AttacherType = Attacher::AttachEngine3D
  Height = 10
  Placement = pos=(19,8e-15,-24) rot=(0,0,-1;1.5708rad)
  Radius = 1
FEATURE [Part::Cylinder] Cylinder175  label="Válec175"
  Angle = 360
  AttacherType = Attacher::AttachEngine3D
  Height = 10
  Placement = pos=(13.44,13.44,-24) rot=(0,0,-1;0.785398rad)
  Radius = 1
FEATURE [Part::Cylinder] Cylinder176  label="Válec176"
  Angle = 360
  AttacherType = Attacher::AttachEngine3D
  Height = 2
  Placement = pos=(-19,0,-22) rot=(0,0,1;1.5708rad)
  Radius = 2
FEATURE [Part::Cylinder] Cylinder177  label="Válec177"
  Angle = 360
  AttacherType = Attacher::AttachEngine3D
  Height = 2
  Placement = pos=(6e-15,-19,-22) rot=(0,0,1;3.14159rad)
  Radius = 2
FEATURE [Part::Cylinder] Cylinder178  label="Válec178"
  Angle = 360
  AttacherType = Attacher::AttachEngine3D
  Height = 2
  Placement = pos=(0,19,-22) rot=(0,0,1;0rad)
  Radius = 2
FEATURE [Part::Cylinder] Cylinder179  label="Válec179"
  Angle = 360
  AttacherType = Attacher::AttachEngine3D
  Height = 2
  Placement = pos=(-13.44,13.44,-22) rot=(0,0,1;0.785398rad)
  Radius = 2
FEATURE [Part::Cylinder] Cylinder180  label="Válec180"
  Angle = 360
  AttacherType = Attacher::AttachEngine3D
  Height = 2
  Placement = pos=(-13.44,-13.44,-22) rot=(0,0,1;2.35619rad)
  Radius = 2
FEATURE [Part::Cylinder] Cylinder181  label="Válec181"
  Angle = 360
  AttacherType = Attacher::AttachEngine3D
  Height = 2
  Placement = pos=(19,8e-15,-22) rot=(0,0,-1;1.5708rad)
  Radius = 2
FEATURE [Part::Cylinder] Cylinder182  label="Válec182"
  Angle = 360
  AttacherType = Attacher::AttachEngine3D
  Height = 2
  Placement = pos=(13.44,-13.44,-22) rot=(0,0,1;3.92699rad)
  Radius = 2
FEATURE [Part::FeaturePython] Tube032  # WARN: FeaturePython — macro-defined, semantics opaque (R4)
  AttacherType = Attacher::AttachEngine3D
  Height = 6
  InnerRadius = 17
  OuterRadius = 21
  Placement = pos=(0,0,-22) rot=(0,0,1;0rad)
FEATURE [Part::Cylinder] Cylinder183  label="Válec183"
  Angle = 360
  AttacherType = Attacher::AttachEngine3D
  Height = 2
  Placement = pos=(13.44,13.44,-22) rot=(0,0,-1;0.785398rad)
  Radius = 2
FEATURE [Part::Cylinder] Cylinder184  label="Válec184"
  Angle = 360
  AttacherType = Attacher::AttachEngine3D
  Height = 10
  Placement = pos=(-19,0,-24) rot=(0,0,1;1.5708rad)
  Radius = 1
FEATURE [Part::Cylinder] Cylinder185  label="Válec185"
  Angle = 360
  AttacherType = Attacher::AttachEngine3D
  Height = 10
  Placement = pos=(6e-15,-19,-24) rot=(0,0,1;3.14159rad)
  Radius = 1
FEATURE [Part::Cylinder] Cylinder186  label="Válec186"
  Angle = 360
  AttacherType = Attacher::AttachEngine3D
  Height = 10
  Placement = pos=(0,19,-24) rot=(0,0,1;0rad)
  Radius = 1
FEATURE [Part::Cylinder] Cylinder187  label="Válec187"
  Angle = 360
  AttacherType = Attacher::AttachEngine3D
  Height = 10
  Placement = pos=(-13.44,13.44,-24) rot=(0,0,1;0.785398rad)
  Radius = 1
FEATURE [Part::Cylinder] Cylinder188  label="Válec188"
  Angle = 360
  AttacherType = Attacher::AttachEngine3D
  Height = 10
  Placement = pos=(-13.44,-13.44,-24) rot=(0,0,1;2.35619rad)
  Radius = 1
FEATURE [Part::Cylinder] Cylinder189  label="Válec189"
  Angle = 360
  AttacherType = Attacher::AttachEngine3D
  Height = 10
  Placement = pos=(19,8e-15,-24) rot=(0,0,-1;1.5708rad)
  Radius = 1
FEATURE [Part::Cylinder] Cylinder190  label="Válec190"
  Angle = 360
  AttacherType = Attacher::AttachEngine3D
  Height = 10
  Placement = pos=(13.44,-13.44,-24) rot=(0,0,1;3.92699rad)
  Radius = 1
FEATURE [Part::Cylinder] Cylinder191  label="Válec191"
  Angle = 360
  AttacherType = Attacher::AttachEngine3D
  Height = 10
  Placement = pos=(13.44,13.44,-24) rot=(0,0,-1;0.785398rad)
  Radius = 1
FEATURE [Part::Cylinder] Cylinder192  label="Válec192"
  Angle = 360
  AttacherType = Attacher::AttachEngine3D
  Height = 50
  Placement = pos=(0,0,-29) rot=(0,0,1;0rad)
  Radius = 8
FEATURE [Part::Cylinder] Cylinder193  label="Válec193"
  Angle = 360
  AttacherType = Attacher::AttachEngine3D
  Height = 3
  Placement = pos=(-19,-19,-24) rot=(0,0,1;0rad)
  Radius = 3
FEATURE [Part::Cylinder] Cylinder194  label="Válec194"
  Angle = 360
  AttacherType = Attacher::AttachEngine3D
  Height = 10
  Placement = pos=(-19.5,-19.5,-28) rot=(0,0,1;0rad)
  Radius = 1.5
FEATURE [Part::Cylinder] Cylinder195  label="Válec195"
  Angle = 360
  AttacherType = Attacher::AttachEngine3D
  Height = 10
  Placement = pos=(-19.5,19.5,-28) rot=(0,0,1;0rad)
  Radius = 1.5
FEATURE [Part::Cylinder] Cylinder196  label="Válec196"
  Angle = 360
  AttacherType = Attacher::AttachEngine3D
  Height = 10
  Placement = pos=(19.5,-19.5,-28) rot=(0,0,1;0rad)
  Radius = 1.5
FEATURE [Part::Cylinder] Cylinder197  label="Válec197"
  Angle = 360
  AttacherType = Attacher::AttachEngine3D
  Height = 10
  Placement = pos=(19.5,19.5,-28) rot=(0,0,1;0rad)
  Radius = 1.5
FEATURE [Part::Cylinder] Cylinder198  label="Válec198"
  Angle = 360
  AttacherType = Attacher::AttachEngine3D
  Height = 3
  Placement = pos=(19,-19,-24) rot=(0,0,1;0rad)
  Radius = 3
FEATURE [Part::Cylinder] Cylinder199  label="Válec199"
  Angle = 360
  AttacherType = Attacher::AttachEngine3D
  Height = 3
  Placement = pos=(-19,19,-24) rot=(0,0,1;0rad)
  Radius = 3
FEATURE [Part::Cylinder] Cylinder200  label="Válec200"
  Angle = 360
  AttacherType = Attacher::AttachEngine3D
  Height = 3
  Placement = pos=(19,19,-24) rot=(0,0,1;0rad)
  Radius = 3
FEATURE [Part::Compound] Compound062
  Links = -> [Cylinder170,Cylinder168,Cylinder169,Cylinder171,Cylinder172,Cylinder173,Cylinder174,Cylinder175]
FEATURE [Part::Compound] Compound063
  Links = -> [Cylinder178,Cylinder179,Cylinder176,Cylinder180,Cylinder177,Cylinder182,Cylinder181,Cylinder183]
  Placement = pos=(0,0,-3) rot=(0,0,1;0rad)
FEATURE [Part::Cut] Cut062
  Base = -> Box055
  Tool = -> Compound063
FEATURE [Part::Cut] Cut064
  Base = -> Cut062
  Tool = -> Compound062
FEATURE [Part::Cut] Cut065
  Base = -> Cut064
  Tool = -> Cylinder192
FEATURE [Part::Compound] Compound066
  Links = -> [Cylinder186,Cylinder187,Cylinder184,Cylinder188,Cylinder185,Cylinder190,Cylinder189,Cylinder191]
FEATURE [Part::Cut] Cut063
  Base = -> Tube032
  Tool = -> Compound066
FEATURE [Part::Compound] Compound067
  Links = -> [Cylinder194,Cylinder195,Cylinder196,Cylinder197]
FEATURE [Part::Cut] Cut066
  Base = -> Cut065
  Tool = -> Compound067
FEATURE [Part::Compound] Compound068
  Links = -> [Cylinder193,Cylinder198,Cylinder199,Cylinder200]
  Placement = pos=(0,0,4) rot=(0,0,1;0rad)
FEATURE [Part::Cut] Cut067
  Base = -> Cut066
  Tool = -> Compound068
FEATURE [Part::Compound] Compound069
  Links = -> [Cut067,Cut063]
FEATURE [Part::Chamfer] Chamfer145
  Base = -> Compound069
  Edges = 2 edges r=2: [Edge1,Edge3]
FEATURE [Part::Chamfer] Chamfer001  label="G-mini_moto-holder-A1"
  Base = -> Chamfer145
  Edges = 2 edges r=2: [Edge43,Edge44]
FEATURE [Part::Compound] Compound1265  label="G-mini_moto-holder-A"
  Links = -> [Common018,Chamfer001]
FEATURE [Part::Box] Box081  label="Krychle081"
  AttacherType = Attacher::AttachEngine3D
  Height = 2
  Length = 8
  Placement = pos=(-24.5,-22.5,-55) rot=(0,0,1;0rad)
  Width = 6
FEATURE [Part::Box] Box082  label="Krychle082"
  AttacherType = Attacher::AttachEngine3D
  Height = 2
  Length = 8
  Placement = pos=(16.5,-22.5,-55) rot=(0,0,1;0rad)
  Width = 6
FEATURE [Part::Box] Box083  label="Krychle083"
  AttacherType = Attacher::AttachEngine3D
  Height = 2
  Length = 8
  Placement = pos=(-24.5,16.5,-55) rot=(0,0,1;0rad)
  Width = 6
FEATURE [Part::Box] Box084  label="Krychle084"
  AttacherType = Attacher::AttachEngine3D
  Height = 2
  Length = 8
  Placement = pos=(16.5,16.5,-55) rot=(0,0,1;0rad)
  Width = 6
FEATURE [Part::Cylinder] Cylinder294  label="Válec294"
  Angle = 360
  AttacherType = Attacher::AttachEngine3D
  Height = 20
  Placement = pos=(-10.48,15.75,-50) rot=(0,0,1;0rad)
  Radius = 1.5
FEATURE [Part::Cylinder] Cylinder295  label="Válec295"
  Angle = 360
  AttacherType = Attacher::AttachEngine3D
  Height = 20
  Placement = pos=(10.48,15.75,-50) rot=(0,0,1;0rad)
  Radius = 1.5
FEATURE [Part::Box] Box085  label="Krychle085"
  AttacherType = Attacher::AttachEngine3D
  Height = 11
  Length = 34
  Placement = pos=(-17,-17,-73) rot=(0,0,1;0rad)
  Width = 34
FEATURE [Part::Box] Box086  label="Krychle086"
  AttacherType = Attacher::AttachEngine3D
  Height = 11
  Length = 46.3
  Placement = pos=(-23.15,-23.15,-73) rot=(0,0,1;0rad)
  Width = 46.3
FEATURE [Part::Cylinder] Cylinder296  label="Válec296"
  Angle = 360
  AttacherType = Attacher::AttachEngine3D
  Height = 3
  Placement = pos=(15.5,-15.5,-54) rot=(0,0,1;0rad)
  Radius = 3
FEATURE [Part::Cylinder] Cylinder297  label="Válec297"
  Angle = 360
  AttacherType = Attacher::AttachEngine3D
  Height = 20
  Placement = pos=(15.5,-15.5,-68) rot=(0,0,1;0rad)
  Radius = 1.5
FEATURE [Part::Compound] Compound088
  Links = -> [Box084,Box083,Box082,Box081]
  Placement = pos=(0,0,-2) rot=(0,0,1;0rad)
FEATURE [Part::Cut] Cut087
  Base = -> Box086
  Placement = pos=(0,0,7) rot=(0,0,1;0rad)
  Tool = -> Box085
FEATURE [Part::Compound] Compound094
  Links = -> [Cylinder294,Cylinder295]
  Placement = pos=(0,0,-10) rot=(0,0,1;0rad)
FEATURE [Part::Box] Box087  label="Krychle087"
  AttacherType = Attacher::AttachEngine3D
  Height = 8
  Length = 42.3
  Placement = pos=(-21.15,-21.15,-70) rot=(0,0,1;0rad)
  Width = 42.3
FEATURE [Part::Cylinder] Cylinder298  label="Válec298"
  Angle = 360
  AttacherType = Attacher::AttachEngine3D
  Height = 3
  Placement = pos=(15.5,15.5,-54) rot=(0,0,1;0rad)
  Radius = 3
FEATURE [Part::Cylinder] Cylinder299  label="Válec299"
  Angle = 360
  AttacherType = Attacher::AttachEngine3D
  Height = 20
  Placement = pos=(15.5,-15.5,-68) rot=(0,0,1;0rad)
  Radius = 1.5
FEATURE [Part::Cylinder] Cylinder300  label="Válec300"
  Angle = 360
  AttacherType = Attacher::AttachEngine3D
  Height = 3
  Placement = pos=(-15.5,15.5,-54) rot=(0,0,1;0rad)
  Radius = 3
FEATURE [Part::Box] Box088  label="Krychle088"
  AttacherType = Attacher::AttachEngine3D
  Height = 2
  Length = 8
  Placement = pos=(-24.5,-22.5,-55) rot=(0,0,1;0rad)
  Width = 6
FEATURE [Part::Box] Box089  label="Krychle089"
  AttacherType = Attacher::AttachEngine3D
  Height = 4
  Length = 46.3
  Placement = pos=(-23.15,-23.15,-25) rot=(0,0,1;0rad)
  Width = 46.3
FEATURE [Part::Cylinder] Cylinder301  label="Válec301"
  Angle = 360
  AttacherType = Attacher::AttachEngine3D
  Height = 20
  Placement = pos=(15.5,15.5,-68) rot=(0,0,1;0rad)
  Radius = 1.5
FEATURE [Part::Cylinder] Cylinder302  label="Válec302"
  Angle = 360
  AttacherType = Attacher::AttachEngine3D
  Height = 20
  Placement = pos=(-15.5,-15.5,-68) rot=(0,0,1;0rad)
  Radius = 1.5
FEATURE [Part::Box] Box090  label="Krychle090"
  AttacherType = Attacher::AttachEngine3D
  Height = 2
  Length = 8
  Placement = pos=(16.5,-22.5,-55) rot=(0,0,1;0rad)
  Width = 6
FEATURE [Part::Box] Box091  label="Krychle091"
  AttacherType = Attacher::AttachEngine3D
  Height = 2
  Length = 8
  Placement = pos=(-24.5,16.5,-55) rot=(0,0,1;0rad)
  Width = 6
FEATURE [Part::Box] Box092  label="Krychle092"
  AttacherType = Attacher::AttachEngine3D
  Height = 8
  Length = 46.3
  Placement = pos=(-23.15,-23.15,-70) rot=(0,0,1;0rad)
  Width = 46.3
FEATURE [Part::Cylinder] Cylinder303  label="Válec303"
  Angle = 360
  AttacherType = Attacher::AttachEngine3D
  Height = 20
  Placement = pos=(-15.5,15.5,-68) rot=(0,0,1;0rad)
  Radius = 1.5
FEATURE [Part::Compound] Compound090
  Links = -> [Cylinder301,Cylinder303,Cylinder299,Cylinder302]
FEATURE [Part::Box] Box093  label="Krychle093"
  AttacherType = Attacher::AttachEngine3D
  Height = 20
  Length = 29
  Placement = pos=(-14.5,0,-75) rot=(0,0,1;0rad)
  Width = 45.5
FEATURE [Part::Cylinder] Cylinder304  label="Válec304"
  Angle = 360
  AttacherType = Attacher::AttachEngine3D
  Height = 3
  Placement = pos=(-15.5,-15.5,-54) rot=(0,0,1;0rad)
  Radius = 3
FEATURE [Part::Cylinder] Cylinder305  label="Válec305"
  Angle = 360
  AttacherType = Attacher::AttachEngine3D
  Height = 10
  Placement = pos=(19.5,-19.5,-28) rot=(0,0,1;0rad)
  Radius = 1.5
FEATURE [Part::Cylinder] Cylinder306  label="Válec306"
  Angle = 360
  AttacherType = Attacher::AttachEngine3D
  Height = 20
  Placement = pos=(15.5,15.5,-68) rot=(0,0,1;0rad)
  Radius = 1.5
FEATURE [Part::Cylinder] Cylinder307  label="Válec307"
  Angle = 360
  AttacherType = Attacher::AttachEngine3D
  Height = 10
  Placement = pos=(-19.5,19.5,-28) rot=(0,0,1;0rad)
  Radius = 1.5
FEATURE [Part::Box] Box094  label="Krychle094"
  AttacherType = Attacher::AttachEngine3D
  Height = 2
  Length = 8
  Placement = pos=(16.5,16.5,-55) rot=(0,0,1;0rad)
  Width = 6
FEATURE [Part::Compound] Compound092
  Links = -> [Box094,Box091,Box090,Box088]
  Placement = pos=(0,0,10) rot=(0,0,1;0rad)
FEATURE [Part::Cylinder] Cylinder308  label="Válec308"
  Angle = 360
  AttacherType = Attacher::AttachEngine3D
  Height = 20
  Placement = pos=(-15.5,-15.5,-68) rot=(0,0,1;0rad)
  Radius = 1.5
FEATURE [Part::Box] Box095  label="Krychle095"
  AttacherType = Attacher::AttachEngine3D
  Height = 20
  Length = 29
  Placement = pos=(-14.5,0,-75) rot=(0,0,1;0rad)
  Width = 45.5
FEATURE [Part::Cylinder] Cylinder309  label="Válec309"
  Angle = 360
  AttacherType = Attacher::AttachEngine3D
  Height = 20
  Placement = pos=(-15.5,15.5,-68) rot=(0,0,1;0rad)
  Radius = 1.5
FEATURE [Part::Compound] Compound095
  Links = -> [Cylinder306,Cylinder309,Cylinder297,Cylinder308]
FEATURE [Part::Cylinder] Cylinder310  label="Válec310"
  Angle = 360
  AttacherType = Attacher::AttachEngine3D
  Height = 50
  Placement = pos=(0,0,-29) rot=(0,0,1;0rad)
  Radius = 8
FEATURE [Part::Cut] Cut090
  Base = -> Box089
  Tool = -> Cylinder310
FEATURE [Part::Cylinder] Cylinder311  label="Válec311"
  Angle = 360
  AttacherType = Attacher::AttachEngine3D
  Height = 10
  Placement = pos=(19.5,19.5,-28) rot=(0,0,1;0rad)
  Radius = 1.5
FEATURE [Part::Cylinder] Cylinder312  label="Válec312"
  Angle = 360
  AttacherType = Attacher::AttachEngine3D
  Height = 10
  Placement = pos=(-19.5,-19.5,-28) rot=(0,0,1;0rad)
  Radius = 1.5
FEATURE [Part::Compound] Compound091
  Links = -> [Cylinder312,Cylinder307,Cylinder305,Cylinder311]
FEATURE [Part::Cut] Cut089
  Base = -> Cut090
  Tool = -> Compound091
FEATURE [Part::Compound] Compound093
  Links = -> [Cut089]
  Placement = pos=(0,0,-30) rot=(0,0,1;0rad)
FEATURE [Part::Cylinder] Cylinder313  label="Válec313"
  Angle = 360
  AttacherType = Attacher::AttachEngine3D
  Height = 20
  Placement = pos=(19.5,19.5,-28) rot=(0,0,1;0rad)
  Radius = 1.5
FEATURE [Part::Cylinder] Cylinder314  label="Válec314"
  Angle = 360
  AttacherType = Attacher::AttachEngine3D
  Height = 20
  Placement = pos=(-19.5,-19.5,-28) rot=(0,0,1;0rad)
  Radius = 1.5
FEATURE [Part::Cylinder] Cylinder315  label="Válec315"
  Angle = 360
  AttacherType = Attacher::AttachEngine3D
  Height = 20
  Placement = pos=(-19.5,19.5,-28) rot=(0,0,1;0rad)
  Radius = 1.5
FEATURE [Part::Cylinder] Cylinder316  label="Válec316"
  Angle = 360
  AttacherType = Attacher::AttachEngine3D
  Height = 20
  Placement = pos=(19.5,-19.5,-28) rot=(0,0,1;0rad)
  Radius = 1.5
FEATURE [Part::Box] Box096  label="Krychle096"
  AttacherType = Attacher::AttachEngine3D
  Height = 8
  Length = 7
  Placement = pos=(-22,15,-74) rot=(0,0,1;0rad)
  Width = 7
FEATURE [Part::Cylinder] Cylinder317  label="Válec317"
  Angle = 360
  AttacherType = Attacher::AttachEngine3D
  Height = 8
  Placement = pos=(-15.15,15.15,-74) rot=(0,0,1;0rad)
  Radius = 6
FEATURE [Part::Cut] Cut092
  Base = -> Compound093
  Tool = -> Compound092
FEATURE [Part::Cut] Cut093
  Base = -> Box092
  Placement = pos=(0,0,-4) rot=(0,0,1;0rad)
  Tool = -> Box087
FEATURE [Part::Cut] Cut088
  Base = -> Cut093
  Tool = -> Box095
FEATURE [Part::Cut] Cut094
  Base = -> Cut087
  Tool = -> Compound090
FEATURE [Part::Cut] Cut095
  Base = -> Cut094
  Tool = -> Box093
FEATURE [Part::Compound] Compound097
  Links = -> [Cylinder304,Cylinder296,Cylinder300,Cylinder298]
FEATURE [Part::Compound] Compound098
  Links = -> [Cylinder314,Cylinder315,Cylinder316,Cylinder313]
  Placement = pos=(0,0,-33) rot=(0,0,1;0rad)
FEATURE [Part::Cut] Cut096
  Base = -> Cut092
  Tool = -> Compound094
FEATURE [Part::Cut] Cut091
  Base = -> Cut096
  Tool = -> Compound095
FEATURE [Part::Cut] Cut097
  Base = -> Cut091
  Tool = -> Compound097
FEATURE [Part::Cut] Cut098
  Base = -> Cut095
  Tool = -> Compound088
FEATURE [Part::Cut] Cut099
  Base = -> Cut098
  Tool = -> Compound098
FEATURE [Part::Cut] Cut100
  Base = -> Box096
  Tool = -> Cylinder317
FEATURE [Part::Cut] Cut101
  Base = -> Box096
  Placement = pos=(0,0,0) rot=(0,0,1;1.5708rad)
  Tool = -> Cylinder317
FEATURE [Part::Cut] Cut102
  Base = -> Box096
  Placement = pos=(0,0,0) rot=(0,0,1;3.14159rad)
  Tool = -> Cylinder317
FEATURE [Part::Cut] Cut103
  Base = -> Box096
  Placement = pos=(0,0,0) rot=(0,0,-1;1.5708rad)
  Tool = -> Cylinder317
FEATURE [Part::Compound] Compound100
  Links = -> [Cut100,Cut101,Cut102,Cut103]
FEATURE [Part::Compound] Compound101
  Links = -> [Cut088,Cut097,Cut099,Compound100]
FEATURE [Part::Chamfer] Chamfer006
  Base = -> Compound101
  Edges = 9 edges r=2: [Edge1,Edge6,Edge29,Edge37,Edge42,Edge58,Edge105,Edge162,Edge181]
FEATURE [Part::Chamfer] Chamfer007
  Base = -> Chamfer006
  Edges = 3 edges r=2: [Edge4,Edge49,Edge115]
FEATURE [Part::Chamfer] Chamfer008  label="G-mini_moto-holder-B1"
  Base = -> Chamfer007
  Edges = 5 edges r=0.9: [Edge3,Edge24,Edge25,Edge27,Edge29]
  Placement = pos=(0,0,26) rot=(1,0,0;0rad)
FEATURE [Part::Cylinder] Cylinder2815  label="Válec2785"
  Angle = 360
  AttacherType = Attacher::AttachEngine3D
  Height = 10
  Radius = 21
FEATURE [Part::Cylinder] Cylinder2816  label="Válec2786"
  Angle = 360
  AttacherType = Attacher::AttachEngine3D
  Height = 10
  Radius = 21
FEATURE [Part::Box] Box1028  label="Krychle1027"
  AttacherType = Attacher::AttachEngine3D
  Height = 1.4
  Length = 4
  Placement = pos=(-2,17,-13) rot=(0,0,1;0rad)
  Width = 4
FEATURE [Part::Box] Box1029  label="Krychle1028"
  AttacherType = Attacher::AttachEngine3D
  Height = 1.4
  Length = 4
  Placement = pos=(-13.435,10.6066,-13) rot=(0,0,1;0.785398rad)
  Width = 4
FEATURE [Part::Box] Box1030  label="Krychle1029"
  AttacherType = Attacher::AttachEngine3D
  Height = 1.4
  Length = 4
  Placement = pos=(-10.6066,-13.435,-13) rot=(0,0,1;2.35619rad)
  Width = 4
FEATURE [Part::Box] Box1031  label="Krychle1030"
  AttacherType = Attacher::AttachEngine3D
  Height = 1.4
  Length = 4
  Placement = pos=(2,-17,-13) rot=(0,0,1;3.14159rad)
  Width = 4
FEATURE [Part::Cylinder] Cylinder2817  label="Válec2787"
  Angle = 360
  AttacherType = Attacher::AttachEngine3D
  Height = 10
  Placement = pos=(0,19,-20) rot=(0,0,1;0rad)
  Radius = 1
FEATURE [Part::Box] Box1032  label="Krychle1031"
  AttacherType = Attacher::AttachEngine3D
  Height = 1.4
  Length = 4
  Placement = pos=(-17,-2,-13) rot=(0,0,1;1.5708rad)
  Width = 4
FEATURE [Part::Box] Box1033  label="Krychle1032"
  AttacherType = Attacher::AttachEngine3D
  Height = 1.4
  Length = 4
  Placement = pos=(13.435,-10.6066,-13) rot=(0,0,1;3.92699rad)
  Width = 4
FEATURE [Part::Box] Box1034  label="Krychle1033"
  AttacherType = Attacher::AttachEngine3D
  Height = 1.4
  Length = 4
  Placement = pos=(10.6066,13.435,-13) rot=(0,0,-1;0.785398rad)
  Width = 4
FEATURE [Part::Cylinder] Cylinder2818  label="Válec2788"
  Angle = 360
  AttacherType = Attacher::AttachEngine3D
  Height = 10
  Placement = pos=(-13.435,13.435,-20) rot=(0,0,1;0.785398rad)
  Radius = 1
FEATURE [Part::Cylinder] Cylinder2819  label="Válec2789"
  Angle = 360
  AttacherType = Attacher::AttachEngine3D
  Height = 10
  Placement = pos=(-19,-1e-15,-20) rot=(0,0,1;1.5708rad)
  Radius = 1
FEATURE [Part::Cylinder] Cylinder2820  label="Válec2790"
  Angle = 360
  AttacherType = Attacher::AttachEngine3D
  Height = 10
  Placement = pos=(-13.435,-13.435,-20) rot=(0,0,1;2.35619rad)
  Radius = 1
FEATURE [Part::Cylinder] Cylinder2821  label="Válec2791"
  Angle = 360
  AttacherType = Attacher::AttachEngine3D
  Height = 10
  Placement = pos=(6e-15,-19,-20) rot=(0,0,1;3.14159rad)
  Radius = 1
FEATURE [Part::FeaturePython] wormgear047  # WARN: FeaturePython — macro-defined, semantics opaque (R4)
  AttacherType = Attacher::AttachEngine3D
  Placement = pos=(0,0,0) rot=(0,0,1;1.13446rad)
  beta = 42.7094
  clearance = 0.25
  diameter = 32.5
  head = 0
  height = 12
  module = 1
  pressure_angle = 20
  reverse_pitch = true
  teeth = 30
  version = 0.0.3
FEATURE [Part::Cut] Cut1078
  Base = -> Cylinder2815
  Tool = -> wormgear047
FEATURE [Part::FeaturePython] wormgear048  # WARN: FeaturePython — macro-defined, semantics opaque (R4)
  AttacherType = Attacher::AttachEngine3D
  Placement = pos=(0,0,0) rot=(0,0,1;1.09607rad)
  beta = 42.7094
  clearance = 0.25
  diameter = 32.5
  head = 0
  height = 12
  module = 1
  pressure_angle = 20
  reverse_pitch = false
  teeth = 30
  version = 0.0.3
FEATURE [Part::Cut] Cut1079
  Base = -> Cylinder2816
  Placement = pos=(0,0,-10) rot=(0,0,1;0rad)
  Tool = -> wormgear048
FEATURE [Part::Compound] Compound1266  label="gearovina-mini_okruh005"
  Links = -> [Cut1079,Cut1078]
FEATURE [Part::FeaturePython] Tube151  # WARN: FeaturePython — macro-defined, semantics opaque (R4)
  AttacherType = Attacher::AttachEngine3D
  Height = 6
  InnerRadius = 17
  OuterRadius = 21
  Placement = pos=(0,0,-16) rot=(0,0,1;0rad)
FEATURE [Part::Cylinder] Cylinder2822  label="Válec2792"
  Angle = 360
  AttacherType = Attacher::AttachEngine3D
  Height = 10
  Placement = pos=(13.435,-13.435,-20) rot=(0,0,1;3.92699rad)
  Radius = 1
FEATURE [Part::Box] Box1035  label="Krychle1034"
  AttacherType = Attacher::AttachEngine3D
  Height = 1.4
  Length = 4
  Placement = pos=(17,2,-13) rot=(0,0,-1;1.5708rad)
  Width = 4
FEATURE [Part::Compound] Compound1267
  Links = -> [Box1028,Box1029,Box1032,Box1030,Box1031,Box1033,Box1035,Box1034]
FEATURE [Part::Cut] Cut1080
  Base = -> Tube151
  Tool = -> Compound1267
FEATURE [Part::Cylinder] Cylinder2823  label="Válec2793"
  Angle = 360
  AttacherType = Attacher::AttachEngine3D
  Height = 10
  Placement = pos=(19,8e-15,-20) rot=(0,0,-1;1.5708rad)
  Radius = 1
FEATURE [Part::Cylinder] Cylinder2824  label="Válec2794"
  Angle = 360
  AttacherType = Attacher::AttachEngine3D
  Height = 10
  Placement = pos=(13.435,13.435,-20) rot=(0,0,-1;0.785398rad)
  Radius = 1
FEATURE [Part::Compound] Compound1268
  Links = -> [Cylinder2817,Cylinder2818,Cylinder2819,Cylinder2820,Cylinder2821,Cylinder2822,Cylinder2823,Cylinder2824]
FEATURE [Part::Cut] Cut1081
  Base = -> Cut1080
  Tool = -> Compound1268
FEATURE [Part::Cylinder] Cylinder2825  label="Válec2795"
  Angle = 360
  AttacherType = Attacher::AttachEngine3D
  Height = 10
  Placement = pos=(0,23,4) rot=(0,0,1;0rad)
  Radius = 1
FEATURE [Part::Cylinder] Cylinder2826  label="Válec2796"
  Angle = 360
  AttacherType = Attacher::AttachEngine3D
  Height = 10
  Placement = pos=(16.2635,16.2635,4) rot=(0,0,-1;0.785398rad)
  Radius = 1
FEATURE [Part::Cylinder] Cylinder2827  label="Válec2797"
  Angle = 360
  AttacherType = Attacher::AttachEngine3D
  Height = 10
  Placement = pos=(16.2635,-16.2635,4) rot=(0,0,1;3.92699rad)
  Radius = 1
FEATURE [Part::Cylinder] Cylinder2828  label="Válec2798"
  Angle = 360
  AttacherType = Attacher::AttachEngine3D
  Height = 10
  Placement = pos=(-16.2635,16.2635,4) rot=(0,0,1;0.785398rad)
  Radius = 1
FEATURE [Part::Cylinder] Cylinder2829  label="Válec2799"
  Angle = 360
  AttacherType = Attacher::AttachEngine3D
  Height = 2
  Placement = pos=(-16.2635,-16.2635,4) rot=(0,0,1;2.35619rad)
  Radius = 2
FEATURE [Part::Cylinder] Cylinder2830  label="Válec2800"
  Angle = 360
  AttacherType = Attacher::AttachEngine3D
  Height = 10
  Placement = pos=(-23,-1e-15,4) rot=(0,0,1;1.5708rad)
  Radius = 1
FEATURE [Part::Cylinder] Cylinder2831  label="Válec2801"
  Angle = 360
  AttacherType = Attacher::AttachEngine3D
  Height = 10
  Placement = pos=(-16.2635,-16.2635,4) rot=(0,0,1;2.35619rad)
  Radius = 1
FEATURE [Part::Cylinder] Cylinder2832  label="Válec2802"
  Angle = 360
  AttacherType = Attacher::AttachEngine3D
  Height = 2
  Placement = pos=(0,23,4) rot=(0,0,1;0rad)
  Radius = 2
FEATURE [Part::Cylinder] Cylinder2833  label="Válec2803"
  Angle = 360
  AttacherType = Attacher::AttachEngine3D
  Height = 10
  Placement = pos=(23,1.1e-14,4) rot=(0,0,-1;1.5708rad)
  Radius = 1
FEATURE [Part::Cylinder] Cylinder2834  label="Válec2804"
  Angle = 360
  AttacherType = Attacher::AttachEngine3D
  Height = 2
  Placement = pos=(-23,-1e-15,4) rot=(0,0,1;1.5708rad)
  Radius = 2
FEATURE [Part::Cylinder] Cylinder2835  label="Válec2805"
  Angle = 360
  AttacherType = Attacher::AttachEngine3D
  Height = 10
  Placement = pos=(4e-15,-23,4) rot=(0,0,1;3.14159rad)
  Radius = 1
FEATURE [Part::Compound] Compound1269
  Links = -> [Cylinder2825,Cylinder2828,Cylinder2830,Cylinder2831,Cylinder2835,Cylinder2827,Cylinder2833,Cylinder2826]
FEATURE [Part::Cylinder] Cylinder2836  label="Válec2806"
  Angle = 360
  AttacherType = Attacher::AttachEngine3D
  Height = 2
  Placement = pos=(16.2635,-16.2635,4) rot=(0,0,1;3.92699rad)
  Radius = 2
FEATURE [Part::Cylinder] Cylinder2837  label="Válec2807"
  Angle = 360
  AttacherType = Attacher::AttachEngine3D
  Height = 2
  Placement = pos=(23,1.1e-14,4) rot=(0,0,-1;1.5708rad)
  Radius = 2
FEATURE [Part::Cylinder] Cylinder2838  label="Válec2808"
  Angle = 360
  AttacherType = Attacher::AttachEngine3D
  Height = 2
  Placement = pos=(16.2635,16.2635,4) rot=(0,0,-1;0.785398rad)
  Radius = 2
FEATURE [Part::Cylinder] Cylinder2839  label="Válec2809"
  Angle = 360
  AttacherType = Attacher::AttachEngine3D
  Height = 2
  Placement = pos=(-16.2635,16.2635,4) rot=(0,0,1;0.785398rad)
  Radius = 2
FEATURE [Part::Cylinder] Cylinder2840  label="Válec2810"
  Angle = 360
  AttacherType = Attacher::AttachEngine3D
  Height = 2
  Placement = pos=(4e-15,-23,4) rot=(0,0,1;3.14159rad)
  Radius = 2
FEATURE [Part::Compound] Compound1270
  Links = -> [Cylinder2832,Cylinder2839,Cylinder2834,Cylinder2829,Cylinder2840,Cylinder2836,Cylinder2837,Cylinder2838]
FEATURE [Part::FeaturePython] Tube152  # WARN: FeaturePython — macro-defined, semantics opaque (R4)
  AttacherType = Attacher::AttachEngine3D
  Height = 6
  InnerRadius = 20
  OuterRadius = 25
  Placement = pos=(0,0,4) rot=(0,0,1;0rad)
FEATURE [Part::Cut] Cut1083
  Base = -> Tube152
  Tool = -> Compound1270
FEATURE [Part::Cut] Cut1082
  Base = -> Cut1083
  Tool = -> Compound1269
FEATURE [Part::Box] Box1036  label="Krychle1035"
  AttacherType = Attacher::AttachEngine3D
  Height = 6
  Length = 2
  Placement = pos=(10,26,11) rot=(0,0,1;0rad)
  Width = 6
FEATURE [Part::Box] Box1037  label="Krychle1036"
  AttacherType = Attacher::AttachEngine3D
  Height = 6
  Length = 2
  Placement = pos=(-12,26,11) rot=(0,0,1;0rad)
  Width = 6
FEATURE [Part::Box] Box1038  label="Krychle1037"
  AttacherType = Attacher::AttachEngine3D
  Height = 6
  Length = 2
  Placement = pos=(8,9,11) rot=(0,0,1;0rad)
  Width = 6
FEATURE [Part::Box] Box1039  label="Krychle1038"
  AttacherType = Attacher::AttachEngine3D
  Height = 6
  Length = 2
  Placement = pos=(-10,9,11) rot=(0,0,1;0rad)
  Width = 6
FEATURE [Part::Cylinder] Cylinder2841  label="Válec2811"
  Angle = 360
  AttacherType = Attacher::AttachEngine3D
  Height = 30
  Radius = 38
FEATURE [Part::Box] Box1040  label="Krychle1039"
  AttacherType = Attacher::AttachEngine3D
  Height = 18
  Length = 30
  Placement = pos=(-15,-17,11) rot=(0,0,1;0rad)
  Width = 64
FEATURE [Part::Box] Box1041  label="Krychle1040"
  AttacherType = Attacher::AttachEngine3D
  Height = 6
  Length = 2
  Placement = pos=(8,-4,11) rot=(0,0,1;0rad)
  Width = 6
FEATURE [Part::Cylinder] Cylinder2842  label="Válec2812"
  Angle = 360
  AttacherType = Attacher::AttachEngine3D
  Height = 64
  Placement = pos=(-26,12,14) rot=(0,1,0;1.5708rad)
  Radius = 1.5
FEATURE [Part::Cylinder] Cylinder2843  label="Válec2813"
  Angle = 360
  AttacherType = Attacher::AttachEngine3D
  Height = 64
  Placement = pos=(-26,-1,14) rot=(0,1,0;1.5708rad)
  Radius = 1.5
FEATURE [Part::Box] Box1042  label="Krychle1041"
  AttacherType = Attacher::AttachEngine3D
  Height = 18
  Length = 30
  Placement = pos=(-15,-9,11) rot=(0,0,1;0rad)
  Width = 26
FEATURE [Part::Box] Box1043  label="Krychle1042"
  AttacherType = Attacher::AttachEngine3D
  Height = 6
  Length = 2
  Placement = pos=(-10,-4,11) rot=(0,0,1;0rad)
  Width = 6
FEATURE [Part::Box] Box1044  label="Krychle1043"
  AttacherType = Attacher::AttachEngine3D
  Height = 6
  Length = 2
  Placement = pos=(8,20,-1) rot=(0,0,1;0rad)
  Width = 6
FEATURE [Part::Box] Box1045  label="Krychle1044"
  AttacherType = Attacher::AttachEngine3D
  Height = 6
  Length = 2
  Placement = pos=(-10,20,-1) rot=(0,0,1;0rad)
  Width = 6
FEATURE [Part::Box] Box1046  label="Krychle1045"
  AttacherType = Attacher::AttachEngine3D
  Height = 6
  Length = 2
  Placement = pos=(8,20,-14) rot=(0,0,1;0rad)
  Width = 6
FEATURE [Part::Box] Box1047  label="Krychle1046"
  AttacherType = Attacher::AttachEngine3D
  Height = 6
  Length = 2
  Placement = pos=(-10,20,-14) rot=(0,0,1;0rad)
  Width = 6
FEATURE [Part::Box] Box1048  label="Krychle1047"
  AttacherType = Attacher::AttachEngine3D
  Height = 6
  Length = 2
  Placement = pos=(8,20,-1) rot=(0,0,1;0rad)
  Width = 6
FEATURE [Part::Box] Box1049  label="Krychle1048"
  AttacherType = Attacher::AttachEngine3D
  Height = 6
  Length = 2
  Placement = pos=(-10,20,-1) rot=(0,0,1;0rad)
  Width = 6
FEATURE [Part::Box] Box1050  label="Krychle1049"
  AttacherType = Attacher::AttachEngine3D
  Height = 6
  Length = 2
  Placement = pos=(8,20,-14) rot=(0,0,1;0rad)
  Width = 6
FEATURE [Part::Box] Box1051  label="Krychle1050"
  AttacherType = Attacher::AttachEngine3D
  Height = 6
  Length = 2
  Placement = pos=(-10,20,-14) rot=(0,0,1;0rad)
  Width = 6
FEATURE [Part::Box] Box1052  label="Krychle1051"
  AttacherType = Attacher::AttachEngine3D
  Height = 6
  Length = 2
  Placement = pos=(8,20,-1) rot=(0,0,1;0rad)
  Width = 6
FEATURE [Part::Box] Box1053  label="Krychle1052"
  AttacherType = Attacher::AttachEngine3D
  Height = 6
  Length = 2
  Placement = pos=(-10,20,-1) rot=(0,0,1;0rad)
  Width = 6
FEATURE [Part::Compound] Compound1271
  Links = -> [Box1041,Box1043,Box1036,Box1037,Box1038,Box1039]
FEATURE [Part::FeaturePython] Tube153  # WARN: FeaturePython — macro-defined, semantics opaque (R4)
  AttacherType = Attacher::AttachEngine3D
  Height = 26
  InnerRadius = 2
  OuterRadius = 25
  Placement = pos=(0,-3,37) rot=(1,0,0;1.5708rad)
FEATURE [Part::FeaturePython] Tube154  # WARN: FeaturePython — macro-defined, semantics opaque (R4)
  AttacherType = Attacher::AttachEngine3D
  Height = 64
  InnerRadius = 2
  OuterRadius = 21
  Placement = pos=(0,61,37) rot=(1,0,0;1.5708rad)
FEATURE [Part::Cut] Cut1084
  Base = -> Box1040
  Tool = -> Tube153
FEATURE [Part::Cut] Cut1085
  Base = -> Cut1084
  Tool = -> Tube154
FEATURE [Part::Cut] Cut1086
  Base = -> Cut1085
  Tool = -> Compound1271
FEATURE [Part::Common] Common019
  Base = -> Cut1086
  Tool = -> Cylinder2841
FEATURE [Part::Common] Common020
  Base = -> Box1042
  Tool = -> Common019
FEATURE [Part::Compound] Compound1272
  Links = -> [Cylinder2843,Cylinder2842]
FEATURE [Part::Cut] Cut1087
  Base = -> Common020
  Placement = pos=(0,37,1) rot=(0,0.707107,-0.707107;3.14159rad)
  Tool = -> Compound1272
FEATURE [Part::Compound] Compound1273
  Links = -> [Box1044,Box1045,Box1046,Box1047]
FEATURE [Part::Compound] Compound1274
  Links = -> [Box1048,Box1049,Box1050,Box1051]
FEATURE [Part::Cut] Cut1088
  Base = -> Cut1082
  Tool = -> Compound1273
FEATURE [Part::Cut] Cut1089
  Base = -> Compound1266
  Tool = -> Compound1274
FEATURE [Part::FeaturePython] Tube155  # WARN: FeaturePython — macro-defined, semantics opaque (R4)
  AttacherType = Attacher::AttachEngine3D
  Height = 26
  InnerRadius = 2
  OuterRadius = 25
  Placement = pos=(0,-3,37) rot=(1,0,0;1.5708rad)
FEATURE [Part::FeaturePython] Tube156  # WARN: FeaturePython — macro-defined, semantics opaque (R4)
  AttacherType = Attacher::AttachEngine3D
  Height = 64
  InnerRadius = 2
  OuterRadius = 21
  Placement = pos=(0,61,37) rot=(1,0,0;1.5708rad)
FEATURE [Part::Box] Box1054  label="Krychle1053"
  AttacherType = Attacher::AttachEngine3D
  Height = 6
  Length = 2
  Placement = pos=(8,20,-14) rot=(0,0,1;0rad)
  Width = 6
FEATURE [Part::Box] Box1055  label="Krychle1054"
  AttacherType = Attacher::AttachEngine3D
  Height = 6
  Length = 2
  Placement = pos=(-10,20,-14) rot=(0,0,1;0rad)
  Width = 6
FEATURE [Part::Compound] Compound1275
  Links = -> [Box1052,Box1053,Box1054,Box1055]
FEATURE [Part::Cut] Cut1090
  Base = -> Cut1081
  Tool = -> Compound1275
FEATURE [Part::Compound] Compound1276
  Links = -> [Cut1088,Cut1089,Cut1090]
FEATURE [Part::Box] Box1056  label="Krychle1055"
  AttacherType = Attacher::AttachEngine3D
  Height = 20
  Length = 8
  Placement = pos=(-4,-22,-16) rot=(0,0,1;0rad)
  Width = 64
FEATURE [Part::Cylinder] Cylinder2844  label="Válec2814"
  Angle = 360
  AttacherType = Attacher::AttachEngine3D
  Height = 32
  Placement = pos=(16.2635,16.2635,-28) rot=(0,0,-1;0.785398rad)
  Radius = 4
FEATURE [Part::Cylinder] Cylinder2845  label="Válec2815"
  Angle = 360
  AttacherType = Attacher::AttachEngine3D
  Height = 32
  Placement = pos=(-16.2635,16.2635,-28) rot=(0,0,1;0.785398rad)
  Radius = 4
FEATURE [Part::Compound] Compound1277
  Links = -> [Cylinder2844,Cylinder2845]
FEATURE [Part::Cut] Cut1091
  Base = -> Cut1087
  Tool = -> Compound1277
FEATURE [Part::Cut] Cut1092
  Base = -> Cut1091
  Tool = -> Box1056
FEATURE [Part::Box] Box1057  label="Krychle1056"
  AttacherType = Attacher::AttachEngine3D
  Height = 20
  Length = 30
  Placement = pos=(-15,-17,-16) rot=(0,0,1;0rad)
  Width = 64
FEATURE [Part::Box] Box1058  label="Krychle1057"
  AttacherType = Attacher::AttachEngine3D
  Height = 6
  Length = 30
  Placement = pos=(-15,-17,4) rot=(0,0,1;0rad)
  Width = 64
FEATURE [Part::Box] Box1059  label="Krychle1058"
  AttacherType = Attacher::AttachEngine3D
  Height = 6
  Length = 2
  Placement = pos=(10,26,10) rot=(0,0,1;0rad)
  Width = 6
FEATURE [Part::Box] Box1060  label="Krychle1059"
  AttacherType = Attacher::AttachEngine3D
  Height = 6
  Length = 2
  Placement = pos=(-12,26,10) rot=(0,0,1;0rad)
  Width = 6
FEATURE [Part::Box] Box1061  label="Krychle1060"
  AttacherType = Attacher::AttachEngine3D
  Height = 6
  Length = 2
  Placement = pos=(8,9,11) rot=(0,0,1;0rad)
  Width = 6
FEATURE [Part::Box] Box1062  label="Krychle1061"
  AttacherType = Attacher::AttachEngine3D
  Height = 6
  Length = 2
  Placement = pos=(-10,9,10) rot=(0,0,1;0rad)
  Width = 6
FEATURE [Part::Cylinder] Cylinder2846  label="Válec2816"
  Angle = 360
  AttacherType = Attacher::AttachEngine3D
  Height = 30
  Radius = 38
FEATURE [Part::Box] Box1063  label="Krychle1062"
  AttacherType = Attacher::AttachEngine3D
  Height = 18
  Length = 30
  Placement = pos=(-15,-17,11) rot=(0,0,1;0rad)
  Width = 64
FEATURE [Part::Box] Box1064  label="Krychle1063"
  AttacherType = Attacher::AttachEngine3D
  Height = 6
  Length = 2
  Placement = pos=(8,-4,10) rot=(0,0,1;0rad)
  Width = 6
FEATURE [Part::Cylinder] Cylinder2847  label="Válec2817"
  Angle = 360
  AttacherType = Attacher::AttachEngine3D
  Height = 64
  Placement = pos=(-26,12,14) rot=(0,1,0;1.5708rad)
  Radius = 1.5
FEATURE [Part::Cylinder] Cylinder2848  label="Válec2818"
  Angle = 360
  AttacherType = Attacher::AttachEngine3D
  Height = 64
  Placement = pos=(-26,-1,14) rot=(0,1,0;1.5708rad)
  Radius = 1.5
FEATURE [Part::Compound] Compound1278
  Links = -> [Cylinder2848,Cylinder2847]
FEATURE [Part::Box] Box1065  label="Krychle1064"
  AttacherType = Attacher::AttachEngine3D
  Height = 18
  Length = 30
  Placement = pos=(-15,-9,11) rot=(0,0,1;0rad)
  Width = 26
FEATURE [Part::Box] Box1066  label="Krychle1065"
  AttacherType = Attacher::AttachEngine3D
  Height = 6
  Length = 2
  Placement = pos=(-10,-4,10) rot=(0,0,1;0rad)
  Width = 6
FEATURE [Part::Compound] Compound1279
  Links = -> [Box1064,Box1066,Box1059,Box1060,Box1061,Box1062]
FEATURE [Part::Cylinder] Cylinder2849  label="Válec2819"
  Angle = 360
  AttacherType = Attacher::AttachEngine3D
  Height = 32
  Placement = pos=(16.2635,16.2635,-28) rot=(0,0,-1;0.785398rad)
  Radius = 4
FEATURE [Part::Cylinder] Cylinder2850  label="Válec2820"
  Angle = 360
  AttacherType = Attacher::AttachEngine3D
  Height = 32
  Placement = pos=(-16.2635,16.2635,-28) rot=(0,0,1;0.785398rad)
  Radius = 4
FEATURE [Part::Compound] Compound1280
  Links = -> [Cylinder2849,Cylinder2850]
FEATURE [Part::Box] Box1067  label="Krychle1066"
  AttacherType = Attacher::AttachEngine3D
  Height = 20
  Length = 8
  Placement = pos=(-4,-22,-16) rot=(0,0,1;0rad)
  Width = 64
FEATURE [Part::Cut] Cut1093
  Base = -> Box1063
  Tool = -> Tube155
FEATURE [Part::Cut] Cut1094
  Base = -> Cut1093
  Tool = -> Tube156
FEATURE [Part::Cut] Cut1095
  Base = -> Cut1094
  Tool = -> Compound1279
FEATURE [Part::Common] Common021
  Base = -> Cut1095
  Tool = -> Cylinder2846
FEATURE [Part::Common] Common022
  Base = -> Box1065
  Tool = -> Common021
FEATURE [Part::Cut] Cut1096
  Base = -> Common022
  Placement = pos=(0,37,1) rot=(0,0.707107,-0.707107;3.14159rad)
  Tool = -> Compound1278
FEATURE [Part::Cut] Cut1097
  Base = -> Cut1096
  Tool = -> Compound1280
FEATURE [Part::Cut] Cut1098
  Base = -> Cut1097
  Tool = -> Box1067
FEATURE [Part::Common] Common023
  Base = -> Cut1092
  Tool = -> Box1057
FEATURE [Part::Common] Common024
  Base = -> Box1058
  Tool = -> Cut1098
FEATURE [Part::Compound] Compound1281
  Links = -> [Common023,Common024]
FEATURE [Part::Compound] Compound1282  label="G-mini_monoblock"
  Links = -> [Compound1276,Compound1281]
FEATURE [Part::FeaturePython] wormgear036  # WARN: FeaturePython — macro-defined, semantics opaque (R4)
  AttacherType = Attacher::AttachEngine3D
  Placement = pos=(0,0,0) rot=(0,0,1;1.11876rad)
  beta = 43.4518
  clearance = 0.1
  diameter = 9.5
  head = 0.5
  height = 10
  module = 1
  pressure_angle = 20
  reverse_pitch = true
  teeth = 9
  version = 0.0.3
FEATURE [Part::FeaturePython] wormgear049  # WARN: FeaturePython — macro-defined, semantics opaque (R4)
  AttacherType = Attacher::AttachEngine3D
  Placement = pos=(0,0,-10) rot=(0,0,1;0.991347rad)
  beta = 43.4518
  clearance = 0.1
  diameter = 9.5
  head = 0.5
  height = 10
  module = 1
  pressure_angle = 20
  reverse_pitch = false
  teeth = 9
  version = 0.0.3
FEATURE [Part::Cylinder] Cylinder028  label="Válec028"
  Angle = 360
  AttacherType = Attacher::AttachEngine3D
  Height = 60
  Placement = pos=(0,0,-20) rot=(0,0,1;0rad)
  Radius = 2.55
FEATURE [Part::Cut] Cut009
  Base = -> wormgear036
  Tool = -> Cylinder028
FEATURE [Part::Cylinder] Cylinder029  label="Válec029"
  Angle = 360
  AttacherType = Attacher::AttachEngine3D
  Height = 60
  Placement = pos=(0,0,-20) rot=(0,0,1;0rad)
  Radius = 2.55
FEATURE [Part::Cut] Cut008
  Base = -> wormgear049
  Tool = -> Cylinder029
FEATURE [Part::Compound] Compound1283  label="G-mini_outer-gear"
  Links = -> [Cut009,Cut008]
  Placement = pos=(10.4,0,0) rot=(0,0,1;0.593412rad)
FEATURE [Part::FeaturePython] wormgear050  # WARN: FeaturePython — macro-defined, semantics opaque (R4)
  AttacherType = Attacher::AttachEngine3D
  Placement = pos=(0,0,0) rot=(0,0,1;0.193732rad)
  beta = 43.4518
  clearance = 0.1
  diameter = 9.5
  head = 0.5
  height = 10
  module = 1
  pressure_angle = 20
  reverse_pitch = false
  teeth = 9
  version = 0.0.3
FEATURE [Mesh::Feature] Mesh002  label="G-mini_pikovina (Meshed)"
FEATURE [Mesh::Feature] Mesh003  label="G-mini_quikovina (Meshed)"
FEATURE [Mesh::Feature] Mesh004  label="G-mini_outer-gear (Meshed)"
FEATURE [Part::FeaturePython] Tube157  # WARN: FeaturePython — macro-defined, semantics opaque (R4)
  AttacherType = Attacher::AttachEngine3D
  Height = 1
  InnerRadius = 4.5
  OuterRadius = 5
  Placement = pos=(-5.2,-9.00666,54) rot=(0,0,1;4.18879rad)
FEATURE [Part::FeaturePython] Tube158  # WARN: FeaturePython — macro-defined, semantics opaque (R4)
  AttacherType = Attacher::AttachEngine3D
  Height = 1
  InnerRadius = 4.5
  OuterRadius = 5
  Placement = pos=(-5.2,9.00666,54) rot=(0,0,1;2.0944rad)
FEATURE [Part::FeaturePython] Tube159  # WARN: FeaturePython — macro-defined, semantics opaque (R4)
  AttacherType = Attacher::AttachEngine3D
  Height = 1
  InnerRadius = 4.5
  OuterRadius = 5
  Placement = pos=(10.4,0,54) rot=(0,0,1;0rad)
FEATURE [Part::FeaturePython] Tube160  # WARN: FeaturePython — macro-defined, semantics opaque (R4)
  AttacherType = Attacher::AttachEngine3D
  Height = 1
  InnerRadius = 2.5
  OuterRadius = 3
  Placement = pos=(10.4,0,54) rot=(0,0,1;0rad)
FEATURE [Part::FeaturePython] Tube161  # WARN: FeaturePython — macro-defined, semantics opaque (R4)
  AttacherType = Attacher::AttachEngine3D
  Height = 1
  InnerRadius = 2.5
  OuterRadius = 3
  Placement = pos=(-5.2,-9.00666,54) rot=(0,0,1;4.18879rad)
FEATURE [Part::FeaturePython] Tube162  # WARN: FeaturePython — macro-defined, semantics opaque (R4)
  AttacherType = Attacher::AttachEngine3D
  Height = 1
  InnerRadius = 2.5
  OuterRadius = 3
  Placement = pos=(-5.2,9.00666,54) rot=(0,0,1;2.0944rad)
FEATURE [Part::Torus] Torus007  label="Anuloid007"
  Angle1 = -180
  Angle2 = 180
  Angle3 = 360
  AttacherType = Attacher::AttachEngine3D
  Placement = pos=(0,0,17.5) rot=(0,0,1;0rad)
  Radius1 = 19.75
  Radius2 = 2.2
FEATURE [Part::FeaturePython] Tube163  # WARN: FeaturePython — macro-defined, semantics opaque (R4)
  AttacherType = Attacher::AttachEngine3D
  Height = 1
  InnerRadius = 4.5
  OuterRadius = 5
  Placement = pos=(0,0,54) rot=(0,0,1;0rad)
FEATURE [Part::FeaturePython] Tube164  # WARN: FeaturePython — macro-defined, semantics opaque (R4)
  AttacherType = Attacher::AttachEngine3D
  Height = 1
  InnerRadius = 2.5
  OuterRadius = 3
  Placement = pos=(0,0,54) rot=(0,0,1;0rad)
FEATURE [Part::Compound] Compound1286
  Links = -> [Tube159,Tube158,Tube157,Tube160,Tube162,Tube161,Tube163,Tube164]
FEATURE [Part::Cylinder] Cylinder2851  label="Válec2821"
  Angle = 360
  AttacherType = Attacher::AttachEngine3D
  Height = 5
  Placement = pos=(10.4,0,50) rot=(0,0,1;0rad)
  Radius = 5
FEATURE [Part::Cylinder] Cylinder2852  label="Válec2822"
  Angle = 360
  AttacherType = Attacher::AttachEngine3D
  Height = 14
  Placement = pos=(0,0,50) rot=(0,0,1;0rad)
  Radius = 20.5
FEATURE [Part::Cylinder] Cylinder2853  label="Válec2823"
  Angle = 360
  AttacherType = Attacher::AttachEngine3D
  Height = 3
  Placement = pos=(5.25,-9.09327,55) rot=(0,0,-1;1.0472rad)
  Radius = 3
FEATURE [Part::Cylinder] Cylinder2854  label="Válec2824"
  Angle = 360
  AttacherType = Attacher::AttachEngine3D
  Height = 20
  Placement = pos=(5.24839,-9.0942,40) rot=(0,0,-1;1.0472rad)
  Radius = 1.5
FEATURE [Part::Cylinder] Cylinder2855  label="Válec2825"
  Angle = 360
  AttacherType = Attacher::AttachEngine3D
  Height = 5
  Placement = pos=(-5.2,-9.00666,50) rot=(0,0,1;4.18879rad)
  Radius = 5
FEATURE [Part::Cylinder] Cylinder2856  label="Válec2826"
  Angle = 360
  AttacherType = Attacher::AttachEngine3D
  Height = 3
  Placement = pos=(-10.5,3e-15,55) rot=(0,0,1;3.14159rad)
  Radius = 3
FEATURE [Part::Cylinder] Cylinder2857  label="Válec2827"
  Angle = 360
  AttacherType = Attacher::AttachEngine3D
  Height = 5
  Placement = pos=(-5.2,9.00666,50) rot=(0,0,1;2.0944rad)
  Radius = 5
FEATURE [Part::Cylinder] Cylinder2858  label="Válec2828"
  Angle = 360
  AttacherType = Attacher::AttachEngine3D
  Height = 20
  Placement = pos=(-10.5,0.00186,40) rot=(0,0,1;3.14159rad)
  Radius = 1.5
FEATURE [Part::Cylinder] Cylinder2859  label="Válec2829"
  Angle = 360
  AttacherType = Attacher::AttachEngine3D
  Height = 10
  Placement = pos=(-13.08,13.08,26) rot=(0,0,1;0.785398rad)
  Radius = 1
FEATURE [Part::Box] Box1068  label="Krychle1067"
  AttacherType = Attacher::AttachEngine3D
  Height = 1.4
  Length = 4
  Placement = pos=(9.54594,12.3744,26) rot=(0,0,-1;0.785398rad)
  Width = 5
FEATURE [Part::Cylinder] Cylinder2860  label="Válec2830"
  Angle = 360
  AttacherType = Attacher::AttachEngine3D
  Height = 10
  Placement = pos=(-18.5,0,26) rot=(0,0,1;1.5708rad)
  Radius = 1
FEATURE [Part::Box] Box1069  label="Krychle1068"
  AttacherType = Attacher::AttachEngine3D
  Height = 1.4
  Length = 4
  Placement = pos=(2,-15.5,26) rot=(0,0,1;3.14159rad)
  Width = 5
FEATURE [Part::Cylinder] Cylinder2861  label="Válec2831"
  Angle = 360
  AttacherType = Attacher::AttachEngine3D
  Height = 10
  Placement = pos=(6e-15,-18.5,26) rot=(0,0,1;3.14159rad)
  Radius = 1
FEATURE [Part::Cylinder] Cylinder2862  label="Válec2832"
  Angle = 360
  AttacherType = Attacher::AttachEngine3D
  Height = 20
  Placement = pos=(5.25161,9.09234,40) rot=(0,0,1;1.0472rad)
  Radius = 1.5
FEATURE [Part::Compound] Compound1285
  Links = -> [Cylinder2858,Cylinder2854,Cylinder2862]
  Placement = pos=(0,0,4) rot=(0,0,1;0rad)
FEATURE [Part::Cylinder] Cylinder2863  label="Válec2833"
  Angle = 360
  AttacherType = Attacher::AttachEngine3D
  Height = 3
  Placement = pos=(5.25,9.09327,55) rot=(0,0,1;1.0472rad)
  Radius = 3
FEATURE [Part::Compound] Compound1290
  Links = -> [Cylinder2856,Cylinder2853,Cylinder2863]
  Placement = pos=(0,0,6) rot=(0,0,1;0rad)
FEATURE [Part::Box] Box1070  label="Krychle1069"
  AttacherType = Attacher::AttachEngine3D
  Height = 1.4
  Length = 4
  Placement = pos=(-2,15.5,26) rot=(0,0,1;0rad)
  Width = 5
FEATURE [Part::Cylinder] Cylinder2864  label="Válec2834"
  Angle = 360
  AttacherType = Attacher::AttachEngine3D
  Height = 10
  Placement = pos=(-13.08,-13.08,26) rot=(0,0,1;2.35619rad)
  Radius = 1
FEATURE [Part::Cylinder] Cylinder2865  label="Válec2835"
  Angle = 360
  AttacherType = Attacher::AttachEngine3D
  Height = 10
  Placement = pos=(13.08,13.08,26) rot=(0,0,-1;0.785398rad)
  Radius = 1
FEATURE [Part::Cylinder] Cylinder2866  label="Válec2836"
  Angle = 360
  AttacherType = Attacher::AttachEngine3D
  Height = 10
  Placement = pos=(19,8,17.5) rot=(0,0,1;0.392699rad)
  Radius = 2.2
FEATURE [Part::Cylinder] Cylinder2867  label="Válec2837"
  Angle = 360
  AttacherType = Attacher::AttachEngine3D
  Height = 10
  Placement = pos=(18.5,8e-15,26) rot=(0,0,-1;1.5708rad)
  Radius = 1
FEATURE [Part::Cylinder] Cylinder2868  label="Válec2838"
  Angle = 360
  AttacherType = Attacher::AttachEngine3D
  Height = 10
  Placement = pos=(13.08,-13.08,26) rot=(0,0,1;3.92699rad)
  Radius = 1
FEATURE [Part::Box] Box1071  label="Krychle1070"
  AttacherType = Attacher::AttachEngine3D
  Height = 1.4
  Length = 4
  Placement = pos=(-9.54594,-12.3744,26) rot=(0,0,1;2.35619rad)
  Width = 5
FEATURE [Part::Cylinder] Cylinder2869  label="Válec2839"
  Angle = 360
  AttacherType = Attacher::AttachEngine3D
  Height = 10
  Placement = pos=(0,18.5,26) rot=(0,0,1;0rad)
  Radius = 1
FEATURE [Part::Compound] Compound1284
  Links = -> [Cylinder2869,Cylinder2859,Cylinder2860,Cylinder2864,Cylinder2861,Cylinder2868,Cylinder2867,Cylinder2865]
  Placement = pos=(0,0,-6) rot=(0,0,1;0rad)
FEATURE [Part::Box] Box1072  label="Krychle1071"
  AttacherType = Attacher::AttachEngine3D
  Height = 1.4
  Length = 4
  Placement = pos=(-12.3744,9.54594,26) rot=(0,0,1;0.785398rad)
  Width = 5
FEATURE [Part::Box] Box1073  label="Krychle1072"
  AttacherType = Attacher::AttachEngine3D
  Height = 1.4
  Length = 4
  Placement = pos=(-15.5,-2,26) rot=(0,0,1;1.5708rad)
  Width = 5
FEATURE [Part::Box] Box1074  label="Krychle1073"
  AttacherType = Attacher::AttachEngine3D
  Height = 1.4
  Length = 4
  Placement = pos=(12.3744,-9.54594,26) rot=(0,0,1;3.92699rad)
  Width = 5
FEATURE [Part::Box] Box1075  label="Krychle1074"
  AttacherType = Attacher::AttachEngine3D
  Height = 1.4
  Length = 4
  Placement = pos=(15.5,2,26) rot=(0,0,-1;1.5708rad)
  Width = 5
FEATURE [Part::Compound] Compound1288
  Links = -> [Box1070,Box1072,Box1073,Box1071,Box1069,Box1074,Box1075,Box1068]
  Placement = pos=(0,0,-5) rot=(0,0,1;0rad)
FEATURE [Part::Cylinder] Cylinder2870  label="Válec2840"
  Angle = 360
  AttacherType = Attacher::AttachEngine3D
  Height = 5
  Placement = pos=(0,0,50) rot=(0,0,1;0rad)
  Radius = 5
FEATURE [Part::Compound] Compound1287
  Links = -> [Cylinder2851,Cylinder2855,Cylinder2857,Cylinder2870]
FEATURE [Part::Cut] Cut1101
  Base = -> Cylinder2852
  Tool = -> Compound1287
FEATURE [Part::Cut] Cut1104
  Base = -> Cut1101
  Tool = -> Compound1290
FEATURE [Part::Cut] Cut1105
  Base = -> Cut1104
  Tool = -> Compound1285
FEATURE [Part::Compound] Compound1289
  Links = -> [Cut1105,Compound1286]
  Placement = pos=(0,0,-39) rot=(1,0,0;0rad)
FEATURE [Part::Cut] Cut1099
  Base = -> Compound1289
  Tool = -> Torus007
FEATURE [Part::Cut] Cut1103
  Base = -> Cut1099
  Tool = -> Cylinder2866
FEATURE [Part::Cut] Cut1100
  Base = -> Cut1103
  Tool = -> Compound1284
FEATURE [Part::Cut] Cut1102  label="G-mini_quikovina"
  Base = -> Cut1100
  Tool = -> Compound1288
FEATURE [Mesh::Feature] Mesh005  label="G-mini_quikovina (Meshed)001"
FEATURE [Mesh::Feature] Mesh006  label="G-mini_pikovina (Meshed)001"
FEATURE [Mesh::Feature] Mesh007  label="G-mini_bearing-ring (Meshed)001"
FEATURE [Mesh::Feature] Mesh008  label="G-mini_monoblock-m1.2 (Meshed)"
FEATURE [Mesh::Feature] Mesh009  label="G-mini_moto-holder-A (Meshed)"
FEATURE [Mesh::Feature] Mesh010  label="G-mini_monoblock (Meshed)"
FEATURE [Mesh::Feature] Mesh011  label="G-mini_outer-gear (Meshed)001"
FEATURE [Mesh::Feature] Mesh012  label="G-mini_quikovina (Meshed)002"
FEATURE [Mesh::Feature] Mesh013  label="G-mini_quikovina (Meshed)003"
